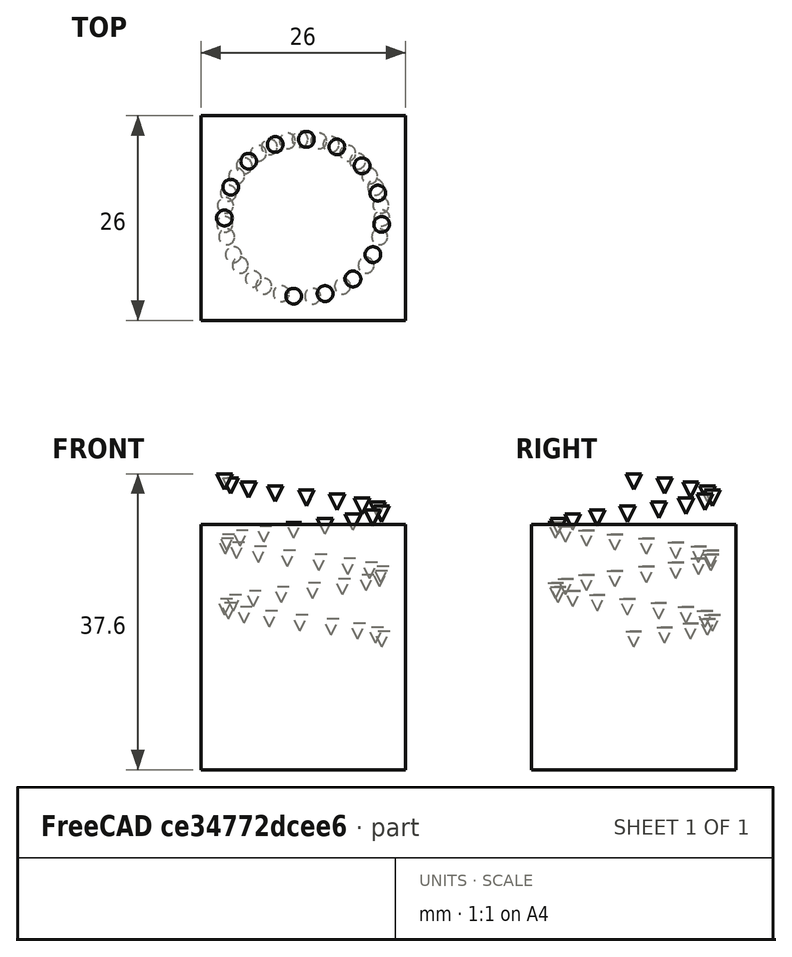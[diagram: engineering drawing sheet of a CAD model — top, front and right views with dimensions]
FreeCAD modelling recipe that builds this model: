
FCSTD DOCUMENT  (FreeCAD 1.0R39109 (Git))
Label: PathArray
License: All rights reserved
objects: App::DocumentObjectGroupPython×1251, Part::FeaturePython×2, App::Part×2, Part::Cone×1, Part::Helix×1
note: 4 computed .brp shape members not serialized (recipe doc carries the construction recipe); baked Part::Feature solids carry a one-line shape summary decoded from their .brp

FEATURE [App::DocumentObjectGroupPython] HALFPI  # scripted group (container) (typed FeaturePython)
  name = HALFPI
  value = pi/2.
FEATURE [App::DocumentObjectGroupPython] PI  # scripted group (container) (typed FeaturePython)
  name = PI
  value = 1.*pi
FEATURE [App::DocumentObjectGroupPython] TWOPI  # scripted group (container) (typed FeaturePython)
  name = TWOPI
  value = 2.*pi
FEATURE [App::DocumentObjectGroupPython] Constants  # scripted group (container) (typed FeaturePython)
  Group = -> [HALFPI,PI,TWOPI]
FEATURE [App::DocumentObjectGroupPython] Variables  # scripted group (container) (typed FeaturePython)
FEATURE [App::DocumentObjectGroupPython] Quantities  # scripted group (container) (typed FeaturePython)
FEATURE [App::DocumentObjectGroupPython] Isotopes  # scripted group (container) (typed FeaturePython)
FEATURE [App::DocumentObjectGroupPython] Elements  # scripted group (container) (typed FeaturePython)
FEATURE [App::DocumentObjectGroupPython] Matrix  # scripted group (container) (typed FeaturePython)
FEATURE [App::DocumentObjectGroupPython] Surfaces  # scripted group (container) (typed FeaturePython)
FEATURE [App::DocumentObjectGroupPython] Opticals  # scripted group (container) (typed FeaturePython)
  Group = -> [Matrix,Surfaces]
FEATURE [App::DocumentObjectGroupPython] G4Isotopes  # scripted group (container) (typed FeaturePython)
FEATURE [App::DocumentObjectGroupPython] H_element  # scripted group (container) (typed FeaturePython)
  Z = 1
  atom_value = 1.008
  formula = H
  name = H_element
FEATURE [App::DocumentObjectGroupPython] He_element  # scripted group (container) (typed FeaturePython)
  Z = 2
  atom_value = 4.0026
  formula = He
  name = He_element
FEATURE [App::DocumentObjectGroupPython] Li_element  # scripted group (container) (typed FeaturePython)
  Z = 3
  atom_value = 6.94
  formula = Li
  name = Li_element
FEATURE [App::DocumentObjectGroupPython] Be_element  # scripted group (container) (typed FeaturePython)
  Z = 4
  atom_value = 9.01218
  formula = Be
  name = Be_element
FEATURE [App::DocumentObjectGroupPython] B_element  # scripted group (container) (typed FeaturePython)
  Z = 5
  atom_value = 10.81
  formula = B
  name = B_element
FEATURE [App::DocumentObjectGroupPython] C_element  # scripted group (container) (typed FeaturePython)
  Z = 6
  atom_value = 12.011
  formula = C
  name = C_element
FEATURE [App::DocumentObjectGroupPython] N_element  # scripted group (container) (typed FeaturePython)
  Z = 7
  atom_value = 14.007
  formula = N
  name = N_element
FEATURE [App::DocumentObjectGroupPython] O_element  # scripted group (container) (typed FeaturePython)
  Z = 8
  atom_value = 15.999
  formula = O
  name = O_element
FEATURE [App::DocumentObjectGroupPython] F_element  # scripted group (container) (typed FeaturePython)
  Z = 9
  atom_value = 18.9984
  formula = F
  name = F_element
FEATURE [App::DocumentObjectGroupPython] Ne_element  # scripted group (container) (typed FeaturePython)
  Z = 10
  atom_value = 20.1797
  formula = Ne
  name = Ne_element
FEATURE [App::DocumentObjectGroupPython] Na_element  # scripted group (container) (typed FeaturePython)
  Z = 11
  atom_value = 22.9898
  formula = Na
  name = Na_element
FEATURE [App::DocumentObjectGroupPython] Mg_element  # scripted group (container) (typed FeaturePython)
  Z = 12
  atom_value = 24.305
  formula = Mg
  name = Mg_element
FEATURE [App::DocumentObjectGroupPython] Al_element  # scripted group (container) (typed FeaturePython)
  Z = 13
  atom_value = 26.9815
  formula = Al
  name = Al_element
FEATURE [App::DocumentObjectGroupPython] Si_element  # scripted group (container) (typed FeaturePython)
  Z = 14
  atom_value = 28.085
  formula = Si
  name = Si_element
FEATURE [App::DocumentObjectGroupPython] P_element  # scripted group (container) (typed FeaturePython)
  Z = 15
  atom_value = 30.9738
  formula = P
  name = P_element
FEATURE [App::DocumentObjectGroupPython] S_element  # scripted group (container) (typed FeaturePython)
  Z = 16
  atom_value = 32.06
  formula = S
  name = S_element
FEATURE [App::DocumentObjectGroupPython] Cl_element  # scripted group (container) (typed FeaturePython)
  Z = 17
  atom_value = 35.45
  formula = Cl
  name = Cl_element
FEATURE [App::DocumentObjectGroupPython] Ar_element  # scripted group (container) (typed FeaturePython)
  Z = 18
  atom_value = 39.95
  formula = Ar
  name = Ar_element
FEATURE [App::DocumentObjectGroupPython] K_element  # scripted group (container) (typed FeaturePython)
  Z = 19
  atom_value = 39.0983
  formula = K
  name = K_element
FEATURE [App::DocumentObjectGroupPython] Ca_element  # scripted group (container) (typed FeaturePython)
  Z = 20
  atom_value = 40.078
  formula = Ca
  name = Ca_element
FEATURE [App::DocumentObjectGroupPython] Sc_element  # scripted group (container) (typed FeaturePython)
  Z = 21
  atom_value = 44.9559
  formula = Sc
  name = Sc_element
FEATURE [App::DocumentObjectGroupPython] Ti_element  # scripted group (container) (typed FeaturePython)
  Z = 22
  atom_value = 47.867
  formula = Ti
  name = Ti_element
FEATURE [App::DocumentObjectGroupPython] V_element  # scripted group (container) (typed FeaturePython)
  Z = 23
  atom_value = 50.9415
  formula = V
  name = V_element
FEATURE [App::DocumentObjectGroupPython] Cr_element  # scripted group (container) (typed FeaturePython)
  Z = 24
  atom_value = 51.9961
  formula = Cr
  name = Cr_element
FEATURE [App::DocumentObjectGroupPython] Mn_element  # scripted group (container) (typed FeaturePython)
  Z = 25
  atom_value = 54.938
  formula = Mn
  name = Mn_element
FEATURE [App::DocumentObjectGroupPython] Fe_element  # scripted group (container) (typed FeaturePython)
  Z = 26
  atom_value = 55.845
  formula = Fe
  name = Fe_element
FEATURE [App::DocumentObjectGroupPython] Co_element  # scripted group (container) (typed FeaturePython)
  Z = 27
  atom_value = 58.9332
  formula = Co
  name = Co_element
FEATURE [App::DocumentObjectGroupPython] Ni_element  # scripted group (container) (typed FeaturePython)
  Z = 28
  atom_value = 58.6934
  formula = Ni
  name = Ni_element
FEATURE [App::DocumentObjectGroupPython] Cu_element  # scripted group (container) (typed FeaturePython)
  Z = 29
  atom_value = 63.546
  formula = Cu
  name = Cu_element
FEATURE [App::DocumentObjectGroupPython] Zn_element  # scripted group (container) (typed FeaturePython)
  Z = 30
  atom_value = 65.38
  formula = Zn
  name = Zn_element
FEATURE [App::DocumentObjectGroupPython] Ga_element  # scripted group (container) (typed FeaturePython)
  Z = 31
  atom_value = 69.723
  formula = Ga
  name = Ga_element
FEATURE [App::DocumentObjectGroupPython] Ge_element  # scripted group (container) (typed FeaturePython)
  Z = 32
  atom_value = 72.63
  formula = Ge
  name = Ge_element
FEATURE [App::DocumentObjectGroupPython] As_element  # scripted group (container) (typed FeaturePython)
  Z = 33
  atom_value = 74.9216
  formula = As
  name = As_element
FEATURE [App::DocumentObjectGroupPython] Se_element  # scripted group (container) (typed FeaturePython)
  Z = 34
  atom_value = 78.971
  formula = Se
  name = Se_element
FEATURE [App::DocumentObjectGroupPython] Br_element  # scripted group (container) (typed FeaturePython)
  Z = 35
  atom_value = 79.904
  formula = Br
  name = Br_element
FEATURE [App::DocumentObjectGroupPython] Kr_element  # scripted group (container) (typed FeaturePython)
  Z = 36
  atom_value = 83.798
  formula = Kr
  name = Kr_element
FEATURE [App::DocumentObjectGroupPython] Rb_element  # scripted group (container) (typed FeaturePython)
  Z = 37
  atom_value = 85.4678
  formula = Rb
  name = Rb_element
FEATURE [App::DocumentObjectGroupPython] Sr_element  # scripted group (container) (typed FeaturePython)
  Z = 38
  atom_value = 87.62
  formula = Sr
  name = Sr_element
FEATURE [App::DocumentObjectGroupPython] Y_element  # scripted group (container) (typed FeaturePython)
  Z = 39
  atom_value = 88.9058
  formula = Y
  name = Y_element
FEATURE [App::DocumentObjectGroupPython] Zr_element  # scripted group (container) (typed FeaturePython)
  Z = 40
  atom_value = 91.224
  formula = Zr
  name = Zr_element
FEATURE [App::DocumentObjectGroupPython] Nb_element  # scripted group (container) (typed FeaturePython)
  Z = 41
  atom_value = 92.9064
  formula = Nb
  name = Nb_element
FEATURE [App::DocumentObjectGroupPython] Mo_element  # scripted group (container) (typed FeaturePython)
  Z = 42
  atom_value = 95.95
  formula = Mo
  name = Mo_element
FEATURE [App::DocumentObjectGroupPython] Tc_element  # scripted group (container) (typed FeaturePython)
  Z = 43
  atom_value = 97
  formula = Tc
  name = Tc_element
FEATURE [App::DocumentObjectGroupPython] Ru_element  # scripted group (container) (typed FeaturePython)
  Z = 44
  atom_value = 101.07
  formula = Ru
  name = Ru_element
FEATURE [App::DocumentObjectGroupPython] Rh_element  # scripted group (container) (typed FeaturePython)
  Z = 45
  atom_value = 102.905
  formula = Rh
  name = Rh_element
FEATURE [App::DocumentObjectGroupPython] Pd_element  # scripted group (container) (typed FeaturePython)
  Z = 46
  atom_value = 106.42
  formula = Pd
  name = Pd_element
FEATURE [App::DocumentObjectGroupPython] Ag_element  # scripted group (container) (typed FeaturePython)
  Z = 47
  atom_value = 107.868
  formula = Ag
  name = Ag_element
FEATURE [App::DocumentObjectGroupPython] Cd_element  # scripted group (container) (typed FeaturePython)
  Z = 48
  atom_value = 112.414
  formula = Cd
  name = Cd_element
FEATURE [App::DocumentObjectGroupPython] In_element  # scripted group (container) (typed FeaturePython)
  Z = 49
  atom_value = 114.818
  formula = In
  name = In_element
FEATURE [App::DocumentObjectGroupPython] Sn_element  # scripted group (container) (typed FeaturePython)
  Z = 50
  atom_value = 118.71
  formula = Sn
  name = Sn_element
FEATURE [App::DocumentObjectGroupPython] Sb_element  # scripted group (container) (typed FeaturePython)
  Z = 51
  atom_value = 121.76
  formula = Sb
  name = Sb_element
FEATURE [App::DocumentObjectGroupPython] Te_element  # scripted group (container) (typed FeaturePython)
  Z = 52
  atom_value = 127.6
  formula = Te
  name = Te_element
FEATURE [App::DocumentObjectGroupPython] I_element  # scripted group (container) (typed FeaturePython)
  Z = 53
  atom_value = 126.904
  formula = I
  name = I_element
FEATURE [App::DocumentObjectGroupPython] Xe_element  # scripted group (container) (typed FeaturePython)
  Z = 54
  atom_value = 131.293
  formula = Xe
  name = Xe_element
FEATURE [App::DocumentObjectGroupPython] Cs_element  # scripted group (container) (typed FeaturePython)
  Z = 55
  atom_value = 132.905
  formula = Cs
  name = Cs_element
FEATURE [App::DocumentObjectGroupPython] Ba_element  # scripted group (container) (typed FeaturePython)
  Z = 56
  atom_value = 137.327
  formula = Ba
  name = Ba_element
FEATURE [App::DocumentObjectGroupPython] La_element  # scripted group (container) (typed FeaturePython)
  Z = 57
  atom_value = 138.905
  formula = La
  name = La_element
FEATURE [App::DocumentObjectGroupPython] Ce_element  # scripted group (container) (typed FeaturePython)
  Z = 58
  atom_value = 140.116
  formula = Ce
  name = Ce_element
FEATURE [App::DocumentObjectGroupPython] Pr_element  # scripted group (container) (typed FeaturePython)
  Z = 59
  atom_value = 140.908
  formula = Pr
  name = Pr_element
FEATURE [App::DocumentObjectGroupPython] Nd_element  # scripted group (container) (typed FeaturePython)
  Z = 60
  atom_value = 144.242
  formula = Nd
  name = Nd_element
FEATURE [App::DocumentObjectGroupPython] Pm_element  # scripted group (container) (typed FeaturePython)
  Z = 61
  atom_value = 145
  formula = Pm
  name = Pm_element
FEATURE [App::DocumentObjectGroupPython] Sm_element  # scripted group (container) (typed FeaturePython)
  Z = 62
  atom_value = 150.36
  formula = Sm
  name = Sm_element
FEATURE [App::DocumentObjectGroupPython] Eu_element  # scripted group (container) (typed FeaturePython)
  Z = 63
  atom_value = 151.964
  formula = Eu
  name = Eu_element
FEATURE [App::DocumentObjectGroupPython] Gd_element  # scripted group (container) (typed FeaturePython)
  Z = 64
  atom_value = 157.25
  formula = Gd
  name = Gd_element
FEATURE [App::DocumentObjectGroupPython] Tb_element  # scripted group (container) (typed FeaturePython)
  Z = 65
  atom_value = 158.925
  formula = Tb
  name = Tb_element
FEATURE [App::DocumentObjectGroupPython] Dy_element  # scripted group (container) (typed FeaturePython)
  Z = 66
  atom_value = 162.5
  formula = Dy
  name = Dy_element
FEATURE [App::DocumentObjectGroupPython] Ho_element  # scripted group (container) (typed FeaturePython)
  Z = 67
  atom_value = 164.93
  formula = Ho
  name = Ho_element
FEATURE [App::DocumentObjectGroupPython] Er_element  # scripted group (container) (typed FeaturePython)
  Z = 68
  atom_value = 167.259
  formula = Er
  name = Er_element
FEATURE [App::DocumentObjectGroupPython] Tm_element  # scripted group (container) (typed FeaturePython)
  Z = 69
  atom_value = 168.934
  formula = Tm
  name = Tm_element
FEATURE [App::DocumentObjectGroupPython] Yb_element  # scripted group (container) (typed FeaturePython)
  Z = 70
  atom_value = 173.045
  formula = Yb
  name = Yb_element
FEATURE [App::DocumentObjectGroupPython] Lu_element  # scripted group (container) (typed FeaturePython)
  Z = 71
  atom_value = 174.967
  formula = Lu
  name = Lu_element
FEATURE [App::DocumentObjectGroupPython] Hf_element  # scripted group (container) (typed FeaturePython)
  Z = 72
  atom_value = 178.49
  formula = Hf
  name = Hf_element
FEATURE [App::DocumentObjectGroupPython] Ta_element  # scripted group (container) (typed FeaturePython)
  Z = 73
  atom_value = 180.948
  formula = Ta
  name = Ta_element
FEATURE [App::DocumentObjectGroupPython] W_element  # scripted group (container) (typed FeaturePython)
  Z = 74
  atom_value = 183.84
  formula = W
  name = W_element
FEATURE [App::DocumentObjectGroupPython] Re_element  # scripted group (container) (typed FeaturePython)
  Z = 75
  atom_value = 186.207
  formula = Re
  name = Re_element
FEATURE [App::DocumentObjectGroupPython] Os_element  # scripted group (container) (typed FeaturePython)
  Z = 76
  atom_value = 190.23
  formula = Os
  name = Os_element
FEATURE [App::DocumentObjectGroupPython] Ir_element  # scripted group (container) (typed FeaturePython)
  Z = 77
  atom_value = 192.217
  formula = Ir
  name = Ir_element
FEATURE [App::DocumentObjectGroupPython] Pt_element  # scripted group (container) (typed FeaturePython)
  Z = 78
  atom_value = 195.084
  formula = Pt
  name = Pt_element
FEATURE [App::DocumentObjectGroupPython] Au_element  # scripted group (container) (typed FeaturePython)
  Z = 79
  atom_value = 196.967
  formula = Au
  name = Au_element
FEATURE [App::DocumentObjectGroupPython] Hg_element  # scripted group (container) (typed FeaturePython)
  Z = 80
  atom_value = 200.592
  formula = Hg
  name = Hg_element
FEATURE [App::DocumentObjectGroupPython] Tl_element  # scripted group (container) (typed FeaturePython)
  Z = 81
  atom_value = 204.38
  formula = Tl
  name = Tl_element
FEATURE [App::DocumentObjectGroupPython] Pb_element  # scripted group (container) (typed FeaturePython)
  Z = 82
  atom_value = 207.2
  formula = Pb
  name = Pb_element
FEATURE [App::DocumentObjectGroupPython] Bi_element  # scripted group (container) (typed FeaturePython)
  Z = 83
  atom_value = 208.98
  formula = Bi
  name = Bi_element
FEATURE [App::DocumentObjectGroupPython] Po_element  # scripted group (container) (typed FeaturePython)
  Z = 84
  atom_value = 209
  formula = Po
  name = Po_element
FEATURE [App::DocumentObjectGroupPython] At_element  # scripted group (container) (typed FeaturePython)
  Z = 85
  atom_value = 210
  formula = At
  name = At_element
FEATURE [App::DocumentObjectGroupPython] Rn_element  # scripted group (container) (typed FeaturePython)
  Z = 86
  atom_value = 222
  formula = Rn
  name = Rn_element
FEATURE [App::DocumentObjectGroupPython] Fr_element  # scripted group (container) (typed FeaturePython)
  Z = 87
  atom_value = 223
  formula = Fr
  name = Fr_element
FEATURE [App::DocumentObjectGroupPython] Ra_element  # scripted group (container) (typed FeaturePython)
  Z = 88
  atom_value = 226
  formula = Ra
  name = Ra_element
FEATURE [App::DocumentObjectGroupPython] Ac_element  # scripted group (container) (typed FeaturePython)
  Z = 89
  atom_value = 227
  formula = Ac
  name = Ac_element
FEATURE [App::DocumentObjectGroupPython] Th_element  # scripted group (container) (typed FeaturePython)
  Z = 90
  atom_value = 232.038
  formula = Th
  name = Th_element
FEATURE [App::DocumentObjectGroupPython] Pa_element  # scripted group (container) (typed FeaturePython)
  Z = 91
  atom_value = 231.036
  formula = Pa
  name = Pa_element
FEATURE [App::DocumentObjectGroupPython] U_element  # scripted group (container) (typed FeaturePython)
  Z = 92
  atom_value = 238.029
  formula = U
  name = U_element
FEATURE [App::DocumentObjectGroupPython] Np_element  # scripted group (container) (typed FeaturePython)
  Z = 93
  atom_value = 237
  formula = Np
  name = Np_element
FEATURE [App::DocumentObjectGroupPython] Pu_element  # scripted group (container) (typed FeaturePython)
  Z = 94
  atom_value = 244
  formula = Pu
  name = Pu_element
FEATURE [App::DocumentObjectGroupPython] Am_element  # scripted group (container) (typed FeaturePython)
  Z = 95
  atom_value = 243
  formula = Am
  name = Am_element
FEATURE [App::DocumentObjectGroupPython] Cm_element  # scripted group (container) (typed FeaturePython)
  Z = 96
  atom_value = 247
  formula = Cm
  name = Cm_element
FEATURE [App::DocumentObjectGroupPython] Bk_element  # scripted group (container) (typed FeaturePython)
  Z = 97
  atom_value = 247
  formula = Bk
  name = Bk_element
FEATURE [App::DocumentObjectGroupPython] Cf_element  # scripted group (container) (typed FeaturePython)
  Z = 98
  atom_value = 251
  formula = Cf
  name = Cf_element
FEATURE [App::DocumentObjectGroupPython] G4Elements  # scripted group (container) (typed FeaturePython)
  Group = -> [H_element,He_element,Li_element,Be_element,B_element,C_element,N_element,O_element,F_element,Ne_element,Na_element,Mg_element,Al_element,Si_element,P_element,S_element,Cl_element,Ar_element,K_element,Ca_element,Sc_element,Ti_element,V_element,Cr_element,Mn_element,Fe_element,Co_element,Ni_element,Cu_element,Zn_element,Ga_element,Ge_element,As_element,Se_element,Br_element,Kr_element,Rb_element,+61 more]
FEATURE [App::DocumentObjectGroupPython] H_element001  label="H_element : 0.101"  # scripted group (container) (typed FeaturePython)
  n = 0.101327
FEATURE [App::DocumentObjectGroupPython] C_element001  label="C_element : 0.775"  # scripted group (container) (typed FeaturePython)
  n = 0.7755
FEATURE [App::DocumentObjectGroupPython] N_element001  label="N_element : 0.035"  # scripted group (container) (typed FeaturePython)
  n = 0.035057
FEATURE [App::DocumentObjectGroupPython] O_element001  label="O_element : 0.052"  # scripted group (container) (typed FeaturePython)
  n = 0.0523159
FEATURE [App::DocumentObjectGroupPython] F_element001  label="F_element : 0.017"  # scripted group (container) (typed FeaturePython)
  n = 0.017422
FEATURE [App::DocumentObjectGroupPython] Ca_element001  label="Ca_element : 0.018"  # scripted group (container) (typed FeaturePython)
  n = 0.018378
FEATURE [App::DocumentObjectGroupPython] G4_A_150_TISSUE  label="G4_A-150_TISSUE"  # scripted group (container) (typed FeaturePython)
  Dunit = g/cm3
  Dvalue = 1.127
  Group = -> [H_element001,C_element001,N_element001,O_element001,F_element001,Ca_element001]
  conduct = 2
  density = 1
  expand = 3
  formula = G4_A-150_TISSUE
  name = G4_A-150_TISSUE
  specific = 4
FEATURE [App::DocumentObjectGroupPython] C_element002  label="C_element : 3"  # scripted group (container) (typed FeaturePython)
  n = 3
  ref = C_element
FEATURE [App::DocumentObjectGroupPython] H_element002  label="H_element : 6"  # scripted group (container) (typed FeaturePython)
  n = 6
  ref = H_element
FEATURE [App::DocumentObjectGroupPython] O_element002  label="O_element : 1"  # scripted group (container) (typed FeaturePython)
  n = 1
  ref = O_element
FEATURE [App::DocumentObjectGroupPython] G4_ACETONE  # scripted group (container) (typed FeaturePython)
  Dunit = g/cm3
  Dvalue = 0.7899
  Group = -> [C_element002,H_element002,O_element002]
  conduct = 2
  density = 1
  expand = 3
  formula = G4_ACETONE
  name = G4_ACETONE
  specific = 4
FEATURE [App::DocumentObjectGroupPython] C_element003  label="C_element : 2"  # scripted group (container) (typed FeaturePython)
  n = 2
  ref = C_element
FEATURE [App::DocumentObjectGroupPython] H_element003  label="H_element : 2"  # scripted group (container) (typed FeaturePython)
  n = 2
  ref = H_element
FEATURE [App::DocumentObjectGroupPython] G4_ACETYLENE  # scripted group (container) (typed FeaturePython)
  Dunit = g/cm3
  Dvalue = 0.0010967
  Group = -> [C_element003,H_element003]
  conduct = 2
  density = 1
  expand = 3
  formula = G4_ACETYLENE
  name = G4_ACETYLENE
  specific = 4
FEATURE [App::DocumentObjectGroupPython] C_element004  label="C_element : 5"  # scripted group (container) (typed FeaturePython)
  n = 5
  ref = C_element
FEATURE [App::DocumentObjectGroupPython] H_element004  label="H_element : 5"  # scripted group (container) (typed FeaturePython)
  n = 5
  ref = H_element
FEATURE [App::DocumentObjectGroupPython] N_element002  label="N_element : 5"  # scripted group (container) (typed FeaturePython)
  n = 5
  ref = N_element
FEATURE [App::DocumentObjectGroupPython] G4_ADENINE  # scripted group (container) (typed FeaturePython)
  Dunit = g/cm3
  Dvalue = 1.6
  Group = -> [C_element004,H_element004,N_element002]
  conduct = 2
  density = 1
  expand = 3
  formula = G4_ADENINE
  name = G4_ADENINE
  specific = 4
FEATURE [App::DocumentObjectGroupPython] H_element005  label="H_element : 0.114"  # scripted group (container) (typed FeaturePython)
  n = 0.114
FEATURE [App::DocumentObjectGroupPython] C_element005  label="C_element : 0.598"  # scripted group (container) (typed FeaturePython)
  n = 0.598
FEATURE [App::DocumentObjectGroupPython] N_element003  label="N_element : 0.007"  # scripted group (container) (typed FeaturePython)
  n = 0.007
FEATURE [App::DocumentObjectGroupPython] O_element003  label="O_element : 0.278"  # scripted group (container) (typed FeaturePython)
  n = 0.278
FEATURE [App::DocumentObjectGroupPython] Na_element001  label="Na_element : 0.001"  # scripted group (container) (typed FeaturePython)
  n = 0.001
FEATURE [App::DocumentObjectGroupPython] S_element001  label="S_element : 0.001"  # scripted group (container) (typed FeaturePython)
  n = 0.001
FEATURE [App::DocumentObjectGroupPython] Cl_element001  label="Cl_element : 0.001"  # scripted group (container) (typed FeaturePython)
  n = 0.001
FEATURE [App::DocumentObjectGroupPython] G4_ADIPOSE_TISSUE_ICRP  # scripted group (container) (typed FeaturePython)
  Dunit = g/cm3
  Dvalue = 0.95
  Group = -> [H_element005,C_element005,N_element003,O_element003,Na_element001,S_element001,Cl_element001]
  conduct = 2
  density = 1
  expand = 3
  formula = G4_ADIPOSE_TISSUE_ICRP
  name = G4_ADIPOSE_TISSUE_ICRP
  specific = 4
FEATURE [App::DocumentObjectGroupPython] C_element006  label="C_element : 0.000"  # scripted group (container) (typed FeaturePython)
  n = 0.000124
FEATURE [App::DocumentObjectGroupPython] N_element004  label="N_element : 0.755"  # scripted group (container) (typed FeaturePython)
  n = 0.755268
FEATURE [App::DocumentObjectGroupPython] O_element004  label="O_element : 0.232"  # scripted group (container) (typed FeaturePython)
  n = 0.231781
FEATURE [App::DocumentObjectGroupPython] Ar_element001  label="Ar_element : 0.013"  # scripted group (container) (typed FeaturePython)
  n = 0.012827
FEATURE [App::DocumentObjectGroupPython] G4_AIR  # scripted group (container) (typed FeaturePython)
  Dunit = g/cm3
  Dvalue = 0.00120479
  Group = -> [C_element006,N_element004,O_element004,Ar_element001]
  conduct = 2
  density = 1
  expand = 3
  formula = G4_AIR
  name = G4_AIR
  specific = 4
FEATURE [App::DocumentObjectGroupPython] C_element007  label="C_element : 006"  # scripted group (container) (typed FeaturePython)
  n = 3
  ref = C_element
FEATURE [App::DocumentObjectGroupPython] H_element006  label="H_element : 7"  # scripted group (container) (typed FeaturePython)
  n = 7
  ref = H_element
FEATURE [App::DocumentObjectGroupPython] N_element005  label="N_element : 1"  # scripted group (container) (typed FeaturePython)
  n = 1
  ref = N_element
FEATURE [App::DocumentObjectGroupPython] O_element005  label="O_element : 2"  # scripted group (container) (typed FeaturePython)
  n = 2
  ref = O_element
FEATURE [App::DocumentObjectGroupPython] G4_ALANINE  # scripted group (container) (typed FeaturePython)
  Dunit = g/cm3
  Dvalue = 1.42
  Group = -> [C_element007,H_element006,N_element005,O_element005]
  conduct = 2
  density = 1
  expand = 3
  formula = G4_ALANINE
  name = G4_ALANINE
  specific = 4
FEATURE [App::DocumentObjectGroupPython] Al_element001  label="Al_element : 2"  # scripted group (container) (typed FeaturePython)
  n = 2
  ref = Al_element
FEATURE [App::DocumentObjectGroupPython] O_element006  label="O_element : 3"  # scripted group (container) (typed FeaturePython)
  n = 3
  ref = O_element
FEATURE [App::DocumentObjectGroupPython] G4_ALUMINUM_OXIDE  # scripted group (container) (typed FeaturePython)
  Dunit = g/cm3
  Dvalue = 3.97
  Group = -> [Al_element001,O_element006]
  conduct = 2
  density = 1
  expand = 3
  formula = G4_ALUMINUM_OXIDE
  name = G4_ALUMINUM_OXIDE
  specific = 4
FEATURE [App::DocumentObjectGroupPython] H_element007  label="H_element : 0.106"  # scripted group (container) (typed FeaturePython)
  n = 0.10593
FEATURE [App::DocumentObjectGroupPython] C_element008  label="C_element : 0.789"  # scripted group (container) (typed FeaturePython)
  n = 0.788974
FEATURE [App::DocumentObjectGroupPython] O_element007  label="O_element : 0.105"  # scripted group (container) (typed FeaturePython)
  n = 0.105096
FEATURE [App::DocumentObjectGroupPython] G4_AMBER  # scripted group (container) (typed FeaturePython)
  Dunit = g/cm3
  Dvalue = 1.1
  Group = -> [H_element007,C_element008,O_element007]
  conduct = 2
  density = 1
  expand = 3
  formula = G4_AMBER
  name = G4_AMBER
  specific = 4
FEATURE [App::DocumentObjectGroupPython] N_element006  label="N_element : 006"  # scripted group (container) (typed FeaturePython)
  n = 1
  ref = N_element
FEATURE [App::DocumentObjectGroupPython] H_element008  label="H_element : 3"  # scripted group (container) (typed FeaturePython)
  n = 3
  ref = H_element
FEATURE [App::DocumentObjectGroupPython] G4_AMMONIA  # scripted group (container) (typed FeaturePython)
  Dunit = g/cm3
  Dvalue = 0.000826019
  Group = -> [N_element006,H_element008]
  conduct = 2
  density = 1
  expand = 3
  formula = G4_AMMONIA
  name = G4_AMMONIA
  specific = 4
FEATURE [App::DocumentObjectGroupPython] C_element009  label="C_element : 6"  # scripted group (container) (typed FeaturePython)
  n = 6
  ref = C_element
FEATURE [App::DocumentObjectGroupPython] H_element009  label="H_element : 008"  # scripted group (container) (typed FeaturePython)
  n = 7
  ref = H_element
FEATURE [App::DocumentObjectGroupPython] N_element007  label="N_element : 007"  # scripted group (container) (typed FeaturePython)
  n = 1
  ref = N_element
FEATURE [App::DocumentObjectGroupPython] G4_ANILINE  # scripted group (container) (typed FeaturePython)
  Dunit = g/cm3
  Dvalue = 1.0235
  Group = -> [C_element009,H_element009,N_element007]
  conduct = 2
  density = 1
  expand = 3
  formula = G4_ANILINE
  name = G4_ANILINE
  specific = 4
FEATURE [App::DocumentObjectGroupPython] C_element010  label="C_element : 14"  # scripted group (container) (typed FeaturePython)
  n = 14
  ref = C_element
FEATURE [App::DocumentObjectGroupPython] H_element010  label="H_element : 10"  # scripted group (container) (typed FeaturePython)
  n = 10
  ref = H_element
FEATURE [App::DocumentObjectGroupPython] G4_ANTHRACENE  # scripted group (container) (typed FeaturePython)
  Dunit = g/cm3
  Dvalue = 1.283
  Group = -> [C_element010,H_element010]
  conduct = 2
  density = 1
  expand = 3
  formula = G4_ANTHRACENE
  name = G4_ANTHRACENE
  specific = 4
FEATURE [App::DocumentObjectGroupPython] H_element011  label="H_element : 0.065"  # scripted group (container) (typed FeaturePython)
  n = 0.0654709
FEATURE [App::DocumentObjectGroupPython] C_element011  label="C_element : 0.537"  # scripted group (container) (typed FeaturePython)
  n = 0.536944
FEATURE [App::DocumentObjectGroupPython] N_element008  label="N_element : 0.021"  # scripted group (container) (typed FeaturePython)
  n = 0.0215
FEATURE [App::DocumentObjectGroupPython] O_element008  label="O_element : 0.032"  # scripted group (container) (typed FeaturePython)
  n = 0.032085
FEATURE [App::DocumentObjectGroupPython] F_element002  label="F_element : 0.167"  # scripted group (container) (typed FeaturePython)
  n = 0.167411
FEATURE [App::DocumentObjectGroupPython] Ca_element002  label="Ca_element : 0.177"  # scripted group (container) (typed FeaturePython)
  n = 0.176589
FEATURE [App::DocumentObjectGroupPython] G4_B_100_BONE  label="G4_B-100_BONE"  # scripted group (container) (typed FeaturePython)
  Dunit = g/cm3
  Dvalue = 1.45
  Group = -> [H_element011,C_element011,N_element008,O_element008,F_element002,Ca_element002]
  conduct = 2
  density = 1
  expand = 3
  formula = G4_B-100_BONE
  name = G4_B-100_BONE
  specific = 4
FEATURE [App::DocumentObjectGroupPython] H_element012  label="H_element : 0.057"  # scripted group (container) (typed FeaturePython)
  n = 0.057441
FEATURE [App::DocumentObjectGroupPython] C_element012  label="C_element : 0.790"  # scripted group (container) (typed FeaturePython)
  n = 0.774591
FEATURE [App::DocumentObjectGroupPython] O_element009  label="O_element : 0.168"  # scripted group (container) (typed FeaturePython)
  n = 0.167968
FEATURE [App::DocumentObjectGroupPython] G4_BAKELITE  # scripted group (container) (typed FeaturePython)
  Dunit = g/cm3
  Dvalue = 1.25
  Group = -> [H_element012,C_element012,O_element009]
  conduct = 2
  density = 1
  expand = 3
  formula = G4_BAKELITE
  name = G4_BAKELITE
  specific = 4
FEATURE [App::DocumentObjectGroupPython] Ba_element001  label="Ba_element : 1"  # scripted group (container) (typed FeaturePython)
  n = 1
  ref = Ba_element
FEATURE [App::DocumentObjectGroupPython] F_element003  label="F_element : 2"  # scripted group (container) (typed FeaturePython)
  n = 2
  ref = F_element
FEATURE [App::DocumentObjectGroupPython] G4_BARIUM_FLUORIDE  # scripted group (container) (typed FeaturePython)
  Dunit = g/cm3
  Dvalue = 4.89
  Group = -> [Ba_element001,F_element003]
  conduct = 2
  density = 1
  expand = 3
  formula = G4_BARIUM_FLUORIDE
  name = G4_BARIUM_FLUORIDE
  specific = 4
FEATURE [App::DocumentObjectGroupPython] Ba_element002  label="Ba_element : 002"  # scripted group (container) (typed FeaturePython)
  n = 1
  ref = Ba_element
FEATURE [App::DocumentObjectGroupPython] S_element002  label="S_element : 1"  # scripted group (container) (typed FeaturePython)
  n = 1
  ref = S_element
FEATURE [App::DocumentObjectGroupPython] O_element010  label="O_element : 4"  # scripted group (container) (typed FeaturePython)
  n = 4
  ref = O_element
FEATURE [App::DocumentObjectGroupPython] G4_BARIUM_SULFATE  # scripted group (container) (typed FeaturePython)
  Dunit = g/cm3
  Dvalue = 4.5
  Group = -> [Ba_element002,S_element002,O_element010]
  conduct = 2
  density = 1
  expand = 3
  formula = G4_BARIUM_SULFATE
  name = G4_BARIUM_SULFATE
  specific = 4
FEATURE [App::DocumentObjectGroupPython] C_element013  label="C_element : 007"  # scripted group (container) (typed FeaturePython)
  n = 6
  ref = C_element
FEATURE [App::DocumentObjectGroupPython] H_element013  label="H_element : 009"  # scripted group (container) (typed FeaturePython)
  n = 6
  ref = H_element
FEATURE [App::DocumentObjectGroupPython] G4_BENZENE  # scripted group (container) (typed FeaturePython)
  Dunit = g/cm3
  Dvalue = 0.87865
  Group = -> [C_element013,H_element013]
  conduct = 2
  density = 1
  expand = 3
  formula = G4_BENZENE
  name = G4_BENZENE
  specific = 4
FEATURE [App::DocumentObjectGroupPython] Be_element001  label="Be_element : 1"  # scripted group (container) (typed FeaturePython)
  n = 1
  ref = Be_element
FEATURE [App::DocumentObjectGroupPython] O_element011  label="O_element : 005"  # scripted group (container) (typed FeaturePython)
  n = 1
  ref = O_element
FEATURE [App::DocumentObjectGroupPython] G4_BERYLLIUM_OXIDE  # scripted group (container) (typed FeaturePython)
  Dunit = g/cm3
  Dvalue = 3.01
  Group = -> [Be_element001,O_element011]
  conduct = 2
  density = 1
  expand = 3
  formula = G4_BERYLLIUM_OXIDE
  name = G4_BERYLLIUM_OXIDE
  specific = 4
FEATURE [App::DocumentObjectGroupPython] Bi_element001  label="Bi_element : 4"  # scripted group (container) (typed FeaturePython)
  n = 4
  ref = Bi_element
FEATURE [App::DocumentObjectGroupPython] Ge_element001  label="Ge_element : 3"  # scripted group (container) (typed FeaturePython)
  n = 3
  ref = Ge_element
FEATURE [App::DocumentObjectGroupPython] O_element012  label="O_element : 12"  # scripted group (container) (typed FeaturePython)
  n = 12
  ref = O_element
FEATURE [App::DocumentObjectGroupPython] G4_BGO  # scripted group (container) (typed FeaturePython)
  Dunit = g/cm3
  Dvalue = 7.13
  Group = -> [Bi_element001,Ge_element001,O_element012]
  conduct = 2
  density = 1
  expand = 3
  formula = G4_BGO
  name = G4_BGO
  specific = 4
FEATURE [App::DocumentObjectGroupPython] H_element014  label="H_element : 0.102"  # scripted group (container) (typed FeaturePython)
  n = 0.102
FEATURE [App::DocumentObjectGroupPython] C_element014  label="C_element : 0.110"  # scripted group (container) (typed FeaturePython)
  n = 0.11
FEATURE [App::DocumentObjectGroupPython] N_element009  label="N_element : 0.033"  # scripted group (container) (typed FeaturePython)
  n = 0.033
FEATURE [App::DocumentObjectGroupPython] O_element013  label="O_element : 0.745"  # scripted group (container) (typed FeaturePython)
  n = 0.745
FEATURE [App::DocumentObjectGroupPython] Na_element002  label="Na_element : 0.002"  # scripted group (container) (typed FeaturePython)
  n = 0.001
FEATURE [App::DocumentObjectGroupPython] P_element001  label="P_element : 0.001"  # scripted group (container) (typed FeaturePython)
  n = 0.001
FEATURE [App::DocumentObjectGroupPython] S_element003  label="S_element : 0.002"  # scripted group (container) (typed FeaturePython)
  n = 0.002
FEATURE [App::DocumentObjectGroupPython] Cl_element002  label="Cl_element : 0.003"  # scripted group (container) (typed FeaturePython)
  n = 0.003
FEATURE [App::DocumentObjectGroupPython] K_element001  label="K_element : 0.002"  # scripted group (container) (typed FeaturePython)
  n = 0.002
FEATURE [App::DocumentObjectGroupPython] Fe_element001  label="Fe_element : 0.001"  # scripted group (container) (typed FeaturePython)
  n = 0.001
FEATURE [App::DocumentObjectGroupPython] G4_BLOOD_ICRP  # scripted group (container) (typed FeaturePython)
  Dunit = g/cm3
  Dvalue = 1.06
  Group = -> [H_element014,C_element014,N_element009,O_element013,Na_element002,P_element001,S_element003,Cl_element002,K_element001,Fe_element001]
  conduct = 2
  density = 1
  expand = 3
  formula = G4_BLOOD_ICRP
  name = G4_BLOOD_ICRP
  specific = 4
FEATURE [App::DocumentObjectGroupPython] H_element015  label="H_element : 0.064"  # scripted group (container) (typed FeaturePython)
  n = 0.064
FEATURE [App::DocumentObjectGroupPython] C_element015  label="C_element : 0.278"  # scripted group (container) (typed FeaturePython)
  n = 0.278
FEATURE [App::DocumentObjectGroupPython] N_element010  label="N_element : 0.027"  # scripted group (container) (typed FeaturePython)
  n = 0.027
FEATURE [App::DocumentObjectGroupPython] O_element014  label="O_element : 0.410"  # scripted group (container) (typed FeaturePython)
  n = 0.41
FEATURE [App::DocumentObjectGroupPython] Mg_element001  label="Mg_element : 0.002"  # scripted group (container) (typed FeaturePython)
  n = 0.002
FEATURE [App::DocumentObjectGroupPython] P_element002  label="P_element : 0.070"  # scripted group (container) (typed FeaturePython)
  n = 0.07
FEATURE [App::DocumentObjectGroupPython] S_element004  label="S_element : 0.003"  # scripted group (container) (typed FeaturePython)
  n = 0.002
FEATURE [App::DocumentObjectGroupPython] Ca_element003  label="Ca_element : 0.147"  # scripted group (container) (typed FeaturePython)
  n = 0.147
FEATURE [App::DocumentObjectGroupPython] G4_BONE_COMPACT_ICRU  # scripted group (container) (typed FeaturePython)
  Dunit = g/cm3
  Dvalue = 1.85
  Group = -> [H_element015,C_element015,N_element010,O_element014,Mg_element001,P_element002,S_element004,Ca_element003]
  conduct = 2
  density = 1
  expand = 3
  formula = G4_BONE_COMPACT_ICRU
  name = G4_BONE_COMPACT_ICRU
  specific = 4
FEATURE [App::DocumentObjectGroupPython] H_element016  label="H_element : 0.034"  # scripted group (container) (typed FeaturePython)
  n = 0.034
FEATURE [App::DocumentObjectGroupPython] C_element016  label="C_element : 0.155"  # scripted group (container) (typed FeaturePython)
  n = 0.155
FEATURE [App::DocumentObjectGroupPython] N_element011  label="N_element : 0.042"  # scripted group (container) (typed FeaturePython)
  n = 0.042
FEATURE [App::DocumentObjectGroupPython] O_element015  label="O_element : 0.435"  # scripted group (container) (typed FeaturePython)
  n = 0.435
FEATURE [App::DocumentObjectGroupPython] Na_element003  label="Na_element : 0.003"  # scripted group (container) (typed FeaturePython)
  n = 0.001
FEATURE [App::DocumentObjectGroupPython] Mg_element002  label="Mg_element : 0.003"  # scripted group (container) (typed FeaturePython)
  n = 0.002
FEATURE [App::DocumentObjectGroupPython] P_element003  label="P_element : 0.103"  # scripted group (container) (typed FeaturePython)
  n = 0.103
FEATURE [App::DocumentObjectGroupPython] S_element005  label="S_element : 0.004"  # scripted group (container) (typed FeaturePython)
  n = 0.003
FEATURE [App::DocumentObjectGroupPython] Ca_element004  label="Ca_element : 0.225"  # scripted group (container) (typed FeaturePython)
  n = 0.225
FEATURE [App::DocumentObjectGroupPython] G4_BONE_CORTICAL_ICRP  # scripted group (container) (typed FeaturePython)
  Dunit = g/cm3
  Dvalue = 1.92
  Group = -> [H_element016,C_element016,N_element011,O_element015,Na_element003,Mg_element002,P_element003,S_element005,Ca_element004]
  conduct = 2
  density = 1
  expand = 3
  formula = G4_BONE_CORTICAL_ICRP
  name = G4_BONE_CORTICAL_ICRP
  specific = 4
FEATURE [App::DocumentObjectGroupPython] B_element001  label="B_element : 4"  # scripted group (container) (typed FeaturePython)
  n = 4
  ref = B_element
FEATURE [App::DocumentObjectGroupPython] C_element017  label="C_element : 1"  # scripted group (container) (typed FeaturePython)
  n = 1
  ref = C_element
FEATURE [App::DocumentObjectGroupPython] G4_BORON_CARBIDE  # scripted group (container) (typed FeaturePython)
  Dunit = g/cm3
  Dvalue = 2.52
  Group = -> [B_element001,C_element017]
  conduct = 2
  density = 1
  expand = 3
  formula = G4_BORON_CARBIDE
  name = G4_BORON_CARBIDE
  specific = 4
FEATURE [App::DocumentObjectGroupPython] B_element002  label="B_element : 2"  # scripted group (container) (typed FeaturePython)
  n = 2
  ref = B_element
FEATURE [App::DocumentObjectGroupPython] O_element016  label="O_element : 006"  # scripted group (container) (typed FeaturePython)
  n = 3
  ref = O_element
FEATURE [App::DocumentObjectGroupPython] G4_BORON_OXIDE  # scripted group (container) (typed FeaturePython)
  Dunit = g/cm3
  Dvalue = 1.812
  Group = -> [B_element002,O_element016]
  conduct = 2
  density = 1
  expand = 3
  formula = G4_BORON_OXIDE
  name = G4_BORON_OXIDE
  specific = 4
FEATURE [App::DocumentObjectGroupPython] H_element017  label="H_element : 0.107"  # scripted group (container) (typed FeaturePython)
  n = 0.107
FEATURE [App::DocumentObjectGroupPython] C_element018  label="C_element : 0.145"  # scripted group (container) (typed FeaturePython)
  n = 0.145
FEATURE [App::DocumentObjectGroupPython] N_element012  label="N_element : 0.022"  # scripted group (container) (typed FeaturePython)
  n = 0.022
FEATURE [App::DocumentObjectGroupPython] O_element017  label="O_element : 0.712"  # scripted group (container) (typed FeaturePython)
  n = 0.712
FEATURE [App::DocumentObjectGroupPython] Na_element004  label="Na_element : 0.004"  # scripted group (container) (typed FeaturePython)
  n = 0.002
FEATURE [App::DocumentObjectGroupPython] P_element004  label="P_element : 0.004"  # scripted group (container) (typed FeaturePython)
  n = 0.004
FEATURE [App::DocumentObjectGroupPython] S_element006  label="S_element : 0.005"  # scripted group (container) (typed FeaturePython)
  n = 0.002
FEATURE [App::DocumentObjectGroupPython] Cl_element003  label="Cl_element : 0.004"  # scripted group (container) (typed FeaturePython)
  n = 0.003
FEATURE [App::DocumentObjectGroupPython] K_element002  label="K_element : 0.003"  # scripted group (container) (typed FeaturePython)
  n = 0.003
FEATURE [App::DocumentObjectGroupPython] G4_BRAIN_ICRP  # scripted group (container) (typed FeaturePython)
  Dunit = g/cm3
  Dvalue = 1.04
  Group = -> [H_element017,C_element018,N_element012,O_element017,Na_element004,P_element004,S_element006,Cl_element003,K_element002]
  conduct = 2
  density = 1
  expand = 3
  formula = G4_BRAIN_ICRP
  name = G4_BRAIN_ICRP
  specific = 4
FEATURE [App::DocumentObjectGroupPython] C_element019  label="C_element : 4"  # scripted group (container) (typed FeaturePython)
  n = 4
  ref = C_element
FEATURE [App::DocumentObjectGroupPython] H_element018  label="H_element : 010"  # scripted group (container) (typed FeaturePython)
  n = 10
  ref = H_element
FEATURE [App::DocumentObjectGroupPython] G4_BUTANE  # scripted group (container) (typed FeaturePython)
  Dunit = g/cm3
  Dvalue = 0.00249343
  Group = -> [C_element019,H_element018]
  conduct = 2
  density = 1
  expand = 3
  formula = G4_BUTANE
  name = G4_BUTANE
  specific = 4
FEATURE [App::DocumentObjectGroupPython] C_element020  label="C_element : 008"  # scripted group (container) (typed FeaturePython)
  n = 4
  ref = C_element
FEATURE [App::DocumentObjectGroupPython] H_element019  label="H_element : 011"  # scripted group (container) (typed FeaturePython)
  n = 10
  ref = H_element
FEATURE [App::DocumentObjectGroupPython] O_element018  label="O_element : 007"  # scripted group (container) (typed FeaturePython)
  n = 1
  ref = O_element
FEATURE [App::DocumentObjectGroupPython] G4_N_BUTYL_ALCOHOL  label="G4_N-BUTYL_ALCOHOL"  # scripted group (container) (typed FeaturePython)
  Dunit = g/cm3
  Dvalue = 0.8098
  Group = -> [C_element020,H_element019,O_element018]
  conduct = 2
  density = 1
  expand = 3
  formula = G4_N-BUTYL_ALCOHOL
  name = G4_N-BUTYL_ALCOHOL
  specific = 4
FEATURE [App::DocumentObjectGroupPython] H_element020  label="H_element : 0.025"  # scripted group (container) (typed FeaturePython)
  n = 0.02468
FEATURE [App::DocumentObjectGroupPython] C_element021  label="C_element : 0.502"  # scripted group (container) (typed FeaturePython)
  n = 0.501611
FEATURE [App::DocumentObjectGroupPython] O_element019  label="O_element : 0.005"  # scripted group (container) (typed FeaturePython)
  n = 0.004527
FEATURE [App::DocumentObjectGroupPython] F_element004  label="F_element : 0.465"  # scripted group (container) (typed FeaturePython)
  n = 0.465209
FEATURE [App::DocumentObjectGroupPython] Si_element001  label="Si_element : 0.004"  # scripted group (container) (typed FeaturePython)
  n = 0.003973
FEATURE [App::DocumentObjectGroupPython] G4_C_552  label="G4_C-552"  # scripted group (container) (typed FeaturePython)
  Dunit = g/cm3
  Dvalue = 1.76
  Group = -> [H_element020,C_element021,O_element019,F_element004,Si_element001]
  conduct = 2
  density = 1
  expand = 3
  formula = G4_C-552
  name = G4_C-552
  specific = 4
FEATURE [App::DocumentObjectGroupPython] Cd_element001  label="Cd_element : 1"  # scripted group (container) (typed FeaturePython)
  n = 1
  ref = Cd_element
FEATURE [App::DocumentObjectGroupPython] Te_element001  label="Te_element : 1"  # scripted group (container) (typed FeaturePython)
  n = 1
  ref = Te_element
FEATURE [App::DocumentObjectGroupPython] G4_CADMIUM_TELLURIDE  # scripted group (container) (typed FeaturePython)
  Dunit = g/cm3
  Dvalue = 6.2
  Group = -> [Cd_element001,Te_element001]
  conduct = 2
  density = 1
  expand = 3
  formula = G4_CADMIUM_TELLURIDE
  name = G4_CADMIUM_TELLURIDE
  specific = 4
FEATURE [App::DocumentObjectGroupPython] Cd_element002  label="Cd_element : 002"  # scripted group (container) (typed FeaturePython)
  n = 1
  ref = Cd_element
FEATURE [App::DocumentObjectGroupPython] W_element001  label="W_element : 1"  # scripted group (container) (typed FeaturePython)
  n = 1
  ref = W_element
FEATURE [App::DocumentObjectGroupPython] O_element020  label="O_element : 008"  # scripted group (container) (typed FeaturePython)
  n = 4
  ref = O_element
FEATURE [App::DocumentObjectGroupPython] G4_CADMIUM_TUNGSTATE  # scripted group (container) (typed FeaturePython)
  Dunit = g/cm3
  Dvalue = 7.9
  Group = -> [Cd_element002,W_element001,O_element020]
  conduct = 2
  density = 1
  expand = 3
  formula = G4_CADMIUM_TUNGSTATE
  name = G4_CADMIUM_TUNGSTATE
  specific = 4
FEATURE [App::DocumentObjectGroupPython] Ca_element005  label="Ca_element : 1"  # scripted group (container) (typed FeaturePython)
  n = 1
  ref = Ca_element
FEATURE [App::DocumentObjectGroupPython] C_element022  label="C_element : 009"  # scripted group (container) (typed FeaturePython)
  n = 1
  ref = C_element
FEATURE [App::DocumentObjectGroupPython] O_element021  label="O_element : 009"  # scripted group (container) (typed FeaturePython)
  n = 3
  ref = O_element
FEATURE [App::DocumentObjectGroupPython] G4_CALCIUM_CARBONATE  # scripted group (container) (typed FeaturePython)
  Dunit = g/cm3
  Dvalue = 2.8
  Group = -> [Ca_element005,C_element022,O_element021]
  conduct = 2
  density = 1
  expand = 3
  formula = G4_CALCIUM_CARBONATE
  name = G4_CALCIUM_CARBONATE
  specific = 4
FEATURE [App::DocumentObjectGroupPython] Ca_element006  label="Ca_element : 002"  # scripted group (container) (typed FeaturePython)
  n = 1
  ref = Ca_element
FEATURE [App::DocumentObjectGroupPython] F_element005  label="F_element : 003"  # scripted group (container) (typed FeaturePython)
  n = 2
  ref = F_element
FEATURE [App::DocumentObjectGroupPython] G4_CALCIUM_FLUORIDE  # scripted group (container) (typed FeaturePython)
  Dunit = g/cm3
  Dvalue = 3.18
  Group = -> [Ca_element006,F_element005]
  conduct = 2
  density = 1
  expand = 3
  formula = G4_CALCIUM_FLUORIDE
  name = G4_CALCIUM_FLUORIDE
  specific = 4
FEATURE [App::DocumentObjectGroupPython] Ca_element007  label="Ca_element : 003"  # scripted group (container) (typed FeaturePython)
  n = 1
  ref = Ca_element
FEATURE [App::DocumentObjectGroupPython] O_element022  label="O_element : 010"  # scripted group (container) (typed FeaturePython)
  n = 1
  ref = O_element
FEATURE [App::DocumentObjectGroupPython] G4_CALCIUM_OXIDE  # scripted group (container) (typed FeaturePython)
  Dunit = g/cm3
  Dvalue = 3.3
  Group = -> [Ca_element007,O_element022]
  conduct = 2
  density = 1
  expand = 3
  formula = G4_CALCIUM_OXIDE
  name = G4_CALCIUM_OXIDE
  specific = 4
FEATURE [App::DocumentObjectGroupPython] Ca_element008  label="Ca_element : 004"  # scripted group (container) (typed FeaturePython)
  n = 1
  ref = Ca_element
FEATURE [App::DocumentObjectGroupPython] S_element007  label="S_element : 002"  # scripted group (container) (typed FeaturePython)
  n = 1
  ref = S_element
FEATURE [App::DocumentObjectGroupPython] O_element023  label="O_element : 011"  # scripted group (container) (typed FeaturePython)
  n = 4
  ref = O_element
FEATURE [App::DocumentObjectGroupPython] G4_CALCIUM_SULFATE  # scripted group (container) (typed FeaturePython)
  Dunit = g/cm3
  Dvalue = 2.96
  Group = -> [Ca_element008,S_element007,O_element023]
  conduct = 2
  density = 1
  expand = 3
  formula = G4_CALCIUM_SULFATE
  name = G4_CALCIUM_SULFATE
  specific = 4
FEATURE [App::DocumentObjectGroupPython] Ca_element009  label="Ca_element : 005"  # scripted group (container) (typed FeaturePython)
  n = 1
  ref = Ca_element
FEATURE [App::DocumentObjectGroupPython] W_element002  label="W_element : 002"  # scripted group (container) (typed FeaturePython)
  n = 1
  ref = W_element
FEATURE [App::DocumentObjectGroupPython] O_element024  label="O_element : 012"  # scripted group (container) (typed FeaturePython)
  n = 4
  ref = O_element
FEATURE [App::DocumentObjectGroupPython] G4_CALCIUM_TUNGSTATE  # scripted group (container) (typed FeaturePython)
  Dunit = g/cm3
  Dvalue = 6.062
  Group = -> [Ca_element009,W_element002,O_element024]
  conduct = 2
  density = 1
  expand = 3
  formula = G4_CALCIUM_TUNGSTATE
  name = G4_CALCIUM_TUNGSTATE
  specific = 4
FEATURE [App::DocumentObjectGroupPython] C_element023  label="C_element : 010"  # scripted group (container) (typed FeaturePython)
  n = 1
  ref = C_element
FEATURE [App::DocumentObjectGroupPython] O_element025  label="O_element : 013"  # scripted group (container) (typed FeaturePython)
  n = 2
  ref = O_element
FEATURE [App::DocumentObjectGroupPython] G4_CARBON_DIOXIDE  # scripted group (container) (typed FeaturePython)
  Dunit = g/cm3
  Dvalue = 0.00184212
  Group = -> [C_element023,O_element025]
  conduct = 2
  density = 1
  expand = 3
  formula = G4_CARBON_DIOXIDE
  name = G4_CARBON_DIOXIDE
  specific = 4
FEATURE [App::DocumentObjectGroupPython] C_element024  label="C_element : 011"  # scripted group (container) (typed FeaturePython)
  n = 1
  ref = C_element
FEATURE [App::DocumentObjectGroupPython] Cl_element004  label="Cl_element : 4"  # scripted group (container) (typed FeaturePython)
  n = 4
  ref = Cl_element
FEATURE [App::DocumentObjectGroupPython] G4_CARBON_TETRACHLORIDE  # scripted group (container) (typed FeaturePython)
  Dunit = g/cm3
  Dvalue = 1.594
  Group = -> [C_element024,Cl_element004]
  conduct = 2
  density = 1
  expand = 3
  formula = G4_CARBON_TETRACHLORIDE
  name = G4_CARBON_TETRACHLORIDE
  specific = 4
FEATURE [App::DocumentObjectGroupPython] C_element025  label="C_element : 012"  # scripted group (container) (typed FeaturePython)
  n = 6
  ref = C_element
FEATURE [App::DocumentObjectGroupPython] H_element021  label="H_element : 012"  # scripted group (container) (typed FeaturePython)
  n = 10
  ref = H_element
FEATURE [App::DocumentObjectGroupPython] O_element026  label="O_element : 5"  # scripted group (container) (typed FeaturePython)
  n = 5
  ref = O_element
FEATURE [App::DocumentObjectGroupPython] G4_CELLULOSE_CELLOPHANE  # scripted group (container) (typed FeaturePython)
  Dunit = g/cm3
  Dvalue = 1.42
  Group = -> [C_element025,H_element021,O_element026]
  conduct = 2
  density = 1
  expand = 3
  formula = G4_CELLULOSE_CELLOPHANE
  name = G4_CELLULOSE_CELLOPHANE
  specific = 4
FEATURE [App::DocumentObjectGroupPython] H_element022  label="H_element : 0.067"  # scripted group (container) (typed FeaturePython)
  n = 0.067125
FEATURE [App::DocumentObjectGroupPython] C_element026  label="C_element : 0.545"  # scripted group (container) (typed FeaturePython)
  n = 0.545403
FEATURE [App::DocumentObjectGroupPython] O_element027  label="O_element : 0.387"  # scripted group (container) (typed FeaturePython)
  n = 0.387472
FEATURE [App::DocumentObjectGroupPython] G4_CELLULOSE_BUTYRATE  # scripted group (container) (typed FeaturePython)
  Dunit = g/cm3
  Dvalue = 1.2
  Group = -> [H_element022,C_element026,O_element027]
  conduct = 2
  density = 1
  expand = 3
  formula = G4_CELLULOSE_BUTYRATE
  name = G4_CELLULOSE_BUTYRATE
  specific = 4
FEATURE [App::DocumentObjectGroupPython] H_element023  label="H_element : 0.029"  # scripted group (container) (typed FeaturePython)
  n = 0.029216
FEATURE [App::DocumentObjectGroupPython] C_element027  label="C_element : 0.271"  # scripted group (container) (typed FeaturePython)
  n = 0.271296
FEATURE [App::DocumentObjectGroupPython] N_element013  label="N_element : 0.121"  # scripted group (container) (typed FeaturePython)
  n = 0.121276
FEATURE [App::DocumentObjectGroupPython] O_element028  label="O_element : 0.578"  # scripted group (container) (typed FeaturePython)
  n = 0.578212
FEATURE [App::DocumentObjectGroupPython] G4_CELLULOSE_NITRATE  # scripted group (container) (typed FeaturePython)
  Dunit = g/cm3
  Dvalue = 1.49
  Group = -> [H_element023,C_element027,N_element013,O_element028]
  conduct = 2
  density = 1
  expand = 3
  formula = G4_CELLULOSE_NITRATE
  name = G4_CELLULOSE_NITRATE
  specific = 4
FEATURE [App::DocumentObjectGroupPython] H_element024  label="H_element : 0.108"  # scripted group (container) (typed FeaturePython)
  n = 0.107596
FEATURE [App::DocumentObjectGroupPython] N_element014  label="N_element : 0.001"  # scripted group (container) (typed FeaturePython)
  n = 0.0008
FEATURE [App::DocumentObjectGroupPython] O_element029  label="O_element : 0.875"  # scripted group (container) (typed FeaturePython)
  n = 0.874976
FEATURE [App::DocumentObjectGroupPython] S_element008  label="S_element : 0.015"  # scripted group (container) (typed FeaturePython)
  n = 0.014627
FEATURE [App::DocumentObjectGroupPython] Ce_element001  label="Ce_element : 0.002"  # scripted group (container) (typed FeaturePython)
  n = 0.002001
FEATURE [App::DocumentObjectGroupPython] G4_CERIC_SULFATE  # scripted group (container) (typed FeaturePython)
  Dunit = g/cm3
  Dvalue = 1.03
  Group = -> [H_element024,N_element014,O_element029,S_element008,Ce_element001]
  conduct = 2
  density = 1
  expand = 3
  formula = G4_CERIC_SULFATE
  name = G4_CERIC_SULFATE
  specific = 4
FEATURE [App::DocumentObjectGroupPython] Cs_element001  label="Cs_element : 1"  # scripted group (container) (typed FeaturePython)
  n = 1
  ref = Cs_element
FEATURE [App::DocumentObjectGroupPython] F_element006  label="F_element : 1"  # scripted group (container) (typed FeaturePython)
  n = 1
  ref = F_element
FEATURE [App::DocumentObjectGroupPython] G4_CESIUM_FLUORIDE  # scripted group (container) (typed FeaturePython)
  Dunit = g/cm3
  Dvalue = 4.115
  Group = -> [Cs_element001,F_element006]
  conduct = 2
  density = 1
  expand = 3
  formula = G4_CESIUM_FLUORIDE
  name = G4_CESIUM_FLUORIDE
  specific = 4
FEATURE [App::DocumentObjectGroupPython] Cs_element002  label="Cs_element : 002"  # scripted group (container) (typed FeaturePython)
  n = 1
  ref = Cs_element
FEATURE [App::DocumentObjectGroupPython] I_element001  label="I_element : 1"  # scripted group (container) (typed FeaturePython)
  n = 1
  ref = I_element
FEATURE [App::DocumentObjectGroupPython] G4_CESIUM_IODIDE  # scripted group (container) (typed FeaturePython)
  Dunit = g/cm3
  Dvalue = 4.51
  Group = -> [Cs_element002,I_element001]
  conduct = 2
  density = 1
  expand = 3
  formula = G4_CESIUM_IODIDE
  name = G4_CESIUM_IODIDE
  specific = 4
FEATURE [App::DocumentObjectGroupPython] C_element028  label="C_element : 013"  # scripted group (container) (typed FeaturePython)
  n = 6
  ref = C_element
FEATURE [App::DocumentObjectGroupPython] H_element025  label="H_element : 013"  # scripted group (container) (typed FeaturePython)
  n = 5
  ref = H_element
FEATURE [App::DocumentObjectGroupPython] Cl_element005  label="Cl_element : 1"  # scripted group (container) (typed FeaturePython)
  n = 1
  ref = Cl_element
FEATURE [App::DocumentObjectGroupPython] G4_CHLOROBENZENE  # scripted group (container) (typed FeaturePython)
  Dunit = g/cm3
  Dvalue = 1.1058
  Group = -> [C_element028,H_element025,Cl_element005]
  conduct = 2
  density = 1
  expand = 3
  formula = G4_CHLOROBENZENE
  name = G4_CHLOROBENZENE
  specific = 4
FEATURE [App::DocumentObjectGroupPython] C_element029  label="C_element : 014"  # scripted group (container) (typed FeaturePython)
  n = 1
  ref = C_element
FEATURE [App::DocumentObjectGroupPython] H_element026  label="H_element : 1"  # scripted group (container) (typed FeaturePython)
  n = 1
  ref = H_element
FEATURE [App::DocumentObjectGroupPython] Cl_element006  label="Cl_element : 3"  # scripted group (container) (typed FeaturePython)
  n = 3
  ref = Cl_element
FEATURE [App::DocumentObjectGroupPython] G4_CHLOROFORM  # scripted group (container) (typed FeaturePython)
  Dunit = g/cm3
  Dvalue = 1.4832
  Group = -> [C_element029,H_element026,Cl_element006]
  conduct = 2
  density = 1
  expand = 3
  formula = G4_CHLOROFORM
  name = G4_CHLOROFORM
  specific = 4
FEATURE [App::DocumentObjectGroupPython] H_element027  label="H_element : 0.010"  # scripted group (container) (typed FeaturePython)
  n = 0.01
FEATURE [App::DocumentObjectGroupPython] C_element030  label="C_element : 0.001"  # scripted group (container) (typed FeaturePython)
  n = 0.001
FEATURE [App::DocumentObjectGroupPython] O_element030  label="O_element : 0.529"  # scripted group (container) (typed FeaturePython)
  n = 0.529107
FEATURE [App::DocumentObjectGroupPython] Na_element005  label="Na_element : 0.016"  # scripted group (container) (typed FeaturePython)
  n = 0.016
FEATURE [App::DocumentObjectGroupPython] Mg_element003  label="Mg_element : 0.004"  # scripted group (container) (typed FeaturePython)
  n = 0.002
FEATURE [App::DocumentObjectGroupPython] Al_element002  label="Al_element : 0.034"  # scripted group (container) (typed FeaturePython)
  n = 0.033872
FEATURE [App::DocumentObjectGroupPython] Si_element002  label="Si_element : 0.337"  # scripted group (container) (typed FeaturePython)
  n = 0.337021
FEATURE [App::DocumentObjectGroupPython] K_element003  label="K_element : 0.013"  # scripted group (container) (typed FeaturePython)
  n = 0.013
FEATURE [App::DocumentObjectGroupPython] Ca_element010  label="Ca_element : 0.044"  # scripted group (container) (typed FeaturePython)
  n = 0.044
FEATURE [App::DocumentObjectGroupPython] Fe_element002  label="Fe_element : 0.014"  # scripted group (container) (typed FeaturePython)
  n = 0.014
FEATURE [App::DocumentObjectGroupPython] G4_CONCRETE  # scripted group (container) (typed FeaturePython)
  Dunit = g/cm3
  Dvalue = 2.3
  Group = -> [H_element027,C_element030,O_element030,Na_element005,Mg_element003,Al_element002,Si_element002,K_element003,Ca_element010,Fe_element002]
  conduct = 2
  density = 1
  expand = 3
  formula = G4_CONCRETE
  name = G4_CONCRETE
  specific = 4
FEATURE [App::DocumentObjectGroupPython] C_element031  label="C_element : 015"  # scripted group (container) (typed FeaturePython)
  n = 6
  ref = C_element
FEATURE [App::DocumentObjectGroupPython] H_element028  label="H_element : 12"  # scripted group (container) (typed FeaturePython)
  n = 12
  ref = H_element
FEATURE [App::DocumentObjectGroupPython] G4_CYCLOHEXANE  # scripted group (container) (typed FeaturePython)
  Dunit = g/cm3
  Dvalue = 0.779
  Group = -> [C_element031,H_element028]
  conduct = 2
  density = 1
  expand = 3
  formula = G4_CYCLOHEXANE
  name = G4_CYCLOHEXANE
  specific = 4
FEATURE [App::DocumentObjectGroupPython] C_element032  label="C_element : 016"  # scripted group (container) (typed FeaturePython)
  n = 6
  ref = C_element
FEATURE [App::DocumentObjectGroupPython] H_element029  label="H_element : 4"  # scripted group (container) (typed FeaturePython)
  n = 4
  ref = H_element
FEATURE [App::DocumentObjectGroupPython] Cl_element007  label="Cl_element : 2"  # scripted group (container) (typed FeaturePython)
  n = 2
  ref = Cl_element
FEATURE [App::DocumentObjectGroupPython] G4_1_2_DICHLOROBENZENE  label="G4_1.2-DICHLOROBENZENE"  # scripted group (container) (typed FeaturePython)
  Dunit = g/cm3
  Dvalue = 1.3048
  Group = -> [C_element032,H_element029,Cl_element007]
  conduct = 2
  density = 1
  expand = 3
  formula = G4_1.2-DICHLOROBENZENE
  name = G4_1.2-DICHLOROBENZENE
  specific = 4
FEATURE [App::DocumentObjectGroupPython] C_element033  label="C_element : 017"  # scripted group (container) (typed FeaturePython)
  n = 4
  ref = C_element
FEATURE [App::DocumentObjectGroupPython] H_element030  label="H_element : 8"  # scripted group (container) (typed FeaturePython)
  n = 8
  ref = H_element
FEATURE [App::DocumentObjectGroupPython] O_element031  label="O_element : 014"  # scripted group (container) (typed FeaturePython)
  n = 1
  ref = O_element
FEATURE [App::DocumentObjectGroupPython] Cl_element008  label="Cl_element : 005"  # scripted group (container) (typed FeaturePython)
  n = 2
  ref = Cl_element
FEATURE [App::DocumentObjectGroupPython] G4_DICHLORODIETHYL_ETHER  # scripted group (container) (typed FeaturePython)
  Dunit = g/cm3
  Dvalue = 1.2199
  Group = -> [C_element033,H_element030,O_element031,Cl_element008]
  conduct = 2
  density = 1
  expand = 3
  formula = G4_DICHLORODIETHYL_ETHER
  name = G4_DICHLORODIETHYL_ETHER
  specific = 4
FEATURE [App::DocumentObjectGroupPython] C_element034  label="C_element : 018"  # scripted group (container) (typed FeaturePython)
  n = 2
  ref = C_element
FEATURE [App::DocumentObjectGroupPython] H_element031  label="H_element : 014"  # scripted group (container) (typed FeaturePython)
  n = 4
  ref = H_element
FEATURE [App::DocumentObjectGroupPython] Cl_element009  label="Cl_element : 006"  # scripted group (container) (typed FeaturePython)
  n = 2
  ref = Cl_element
FEATURE [App::DocumentObjectGroupPython] G4_1_2_DICHLOROETHANE  label="G4_1.2-DICHLOROETHANE"  # scripted group (container) (typed FeaturePython)
  Dunit = g/cm3
  Dvalue = 1.2351
  Group = -> [C_element034,H_element031,Cl_element009]
  conduct = 2
  density = 1
  expand = 3
  formula = G4_1.2-DICHLOROETHANE
  name = G4_1.2-DICHLOROETHANE
  specific = 4
FEATURE [App::DocumentObjectGroupPython] C_element035  label="C_element : 019"  # scripted group (container) (typed FeaturePython)
  n = 4
  ref = C_element
FEATURE [App::DocumentObjectGroupPython] H_element032  label="H_element : 015"  # scripted group (container) (typed FeaturePython)
  n = 10
  ref = H_element
FEATURE [App::DocumentObjectGroupPython] O_element032  label="O_element : 015"  # scripted group (container) (typed FeaturePython)
  n = 1
  ref = O_element
FEATURE [App::DocumentObjectGroupPython] G4_DIETHYL_ETHER  # scripted group (container) (typed FeaturePython)
  Dunit = g/cm3
  Dvalue = 0.71378
  Group = -> [C_element035,H_element032,O_element032]
  conduct = 2
  density = 1
  expand = 3
  formula = G4_DIETHYL_ETHER
  name = G4_DIETHYL_ETHER
  specific = 4
FEATURE [App::DocumentObjectGroupPython] C_element036  label="C_element : 020"  # scripted group (container) (typed FeaturePython)
  n = 3
  ref = C_element
FEATURE [App::DocumentObjectGroupPython] H_element033  label="H_element : 016"  # scripted group (container) (typed FeaturePython)
  n = 7
  ref = H_element
FEATURE [App::DocumentObjectGroupPython] N_element015  label="N_element : 008"  # scripted group (container) (typed FeaturePython)
  n = 1
  ref = N_element
FEATURE [App::DocumentObjectGroupPython] O_element033  label="O_element : 016"  # scripted group (container) (typed FeaturePython)
  n = 1
  ref = O_element
FEATURE [App::DocumentObjectGroupPython] G4_N_N_DIMETHYL_FORMAMIDE  label="G4_N.N-DIMETHYL_FORMAMIDE"  # scripted group (container) (typed FeaturePython)
  Dunit = g/cm3
  Dvalue = 0.9487
  Group = -> [C_element036,H_element033,N_element015,O_element033]
  conduct = 2
  density = 1
  expand = 3
  formula = G4_N.N-DIMETHYL_FORMAMIDE
  name = G4_N.N-DIMETHYL_FORMAMIDE
  specific = 4
FEATURE [App::DocumentObjectGroupPython] C_element037  label="C_element : 021"  # scripted group (container) (typed FeaturePython)
  n = 2
  ref = C_element
FEATURE [App::DocumentObjectGroupPython] H_element034  label="H_element : 017"  # scripted group (container) (typed FeaturePython)
  n = 6
  ref = H_element
FEATURE [App::DocumentObjectGroupPython] O_element034  label="O_element : 017"  # scripted group (container) (typed FeaturePython)
  n = 1
  ref = O_element
FEATURE [App::DocumentObjectGroupPython] S_element009  label="S_element : 003"  # scripted group (container) (typed FeaturePython)
  n = 1
  ref = S_element
FEATURE [App::DocumentObjectGroupPython] G4_DIMETHYL_SULFOXIDE  # scripted group (container) (typed FeaturePython)
  Dunit = g/cm3
  Dvalue = 1.1014
  Group = -> [C_element037,H_element034,O_element034,S_element009]
  conduct = 2
  density = 1
  expand = 3
  formula = G4_DIMETHYL_SULFOXIDE
  name = G4_DIMETHYL_SULFOXIDE
  specific = 4
FEATURE [App::DocumentObjectGroupPython] C_element038  label="C_element : 022"  # scripted group (container) (typed FeaturePython)
  n = 2
  ref = C_element
FEATURE [App::DocumentObjectGroupPython] H_element035  label="H_element : 018"  # scripted group (container) (typed FeaturePython)
  n = 6
  ref = H_element
FEATURE [App::DocumentObjectGroupPython] G4_ETHANE  # scripted group (container) (typed FeaturePython)
  Dunit = g/cm3
  Dvalue = 0.00125324
  Group = -> [C_element038,H_element035]
  conduct = 2
  density = 1
  expand = 3
  formula = G4_ETHANE
  name = G4_ETHANE
  specific = 4
FEATURE [App::DocumentObjectGroupPython] C_element039  label="C_element : 023"  # scripted group (container) (typed FeaturePython)
  n = 2
  ref = C_element
FEATURE [App::DocumentObjectGroupPython] H_element036  label="H_element : 019"  # scripted group (container) (typed FeaturePython)
  n = 6
  ref = H_element
FEATURE [App::DocumentObjectGroupPython] O_element035  label="O_element : 018"  # scripted group (container) (typed FeaturePython)
  n = 1
  ref = O_element
FEATURE [App::DocumentObjectGroupPython] G4_ETHYL_ALCOHOL  # scripted group (container) (typed FeaturePython)
  Dunit = g/cm3
  Dvalue = 0.7893
  Group = -> [C_element039,H_element036,O_element035]
  conduct = 2
  density = 1
  expand = 3
  formula = G4_ETHYL_ALCOHOL
  name = G4_ETHYL_ALCOHOL
  specific = 4
FEATURE [App::DocumentObjectGroupPython] H_element037  label="H_element : 0.090"  # scripted group (container) (typed FeaturePython)
  n = 0.090027
FEATURE [App::DocumentObjectGroupPython] C_element040  label="C_element : 0.585"  # scripted group (container) (typed FeaturePython)
  n = 0.585182
FEATURE [App::DocumentObjectGroupPython] O_element036  label="O_element : 0.325"  # scripted group (container) (typed FeaturePython)
  n = 0.324791
FEATURE [App::DocumentObjectGroupPython] G4_ETHYL_CELLULOSE  # scripted group (container) (typed FeaturePython)
  Dunit = g/cm3
  Dvalue = 1.13
  Group = -> [H_element037,C_element040,O_element036]
  conduct = 2
  density = 1
  expand = 3
  formula = G4_ETHYL_CELLULOSE
  name = G4_ETHYL_CELLULOSE
  specific = 4
FEATURE [App::DocumentObjectGroupPython] C_element041  label="C_element : 024"  # scripted group (container) (typed FeaturePython)
  n = 2
  ref = C_element
FEATURE [App::DocumentObjectGroupPython] H_element038  label="H_element : 020"  # scripted group (container) (typed FeaturePython)
  n = 4
  ref = H_element
FEATURE [App::DocumentObjectGroupPython] G4_ETHYLENE  # scripted group (container) (typed FeaturePython)
  Dunit = g/cm3
  Dvalue = 0.00117497
  Group = -> [C_element041,H_element038]
  conduct = 2
  density = 1
  expand = 3
  formula = G4_ETHYLENE
  name = G4_ETHYLENE
  specific = 4
FEATURE [App::DocumentObjectGroupPython] H_element039  label="H_element : 0.096"  # scripted group (container) (typed FeaturePython)
  n = 0.096
FEATURE [App::DocumentObjectGroupPython] C_element042  label="C_element : 0.195"  # scripted group (container) (typed FeaturePython)
  n = 0.195
FEATURE [App::DocumentObjectGroupPython] N_element016  label="N_element : 0.057"  # scripted group (container) (typed FeaturePython)
  n = 0.057
FEATURE [App::DocumentObjectGroupPython] O_element037  label="O_element : 0.646"  # scripted group (container) (typed FeaturePython)
  n = 0.646
FEATURE [App::DocumentObjectGroupPython] Na_element006  label="Na_element : 0.017"  # scripted group (container) (typed FeaturePython)
  n = 0.001
FEATURE [App::DocumentObjectGroupPython] P_element005  label="P_element : 0.104"  # scripted group (container) (typed FeaturePython)
  n = 0.001
FEATURE [App::DocumentObjectGroupPython] S_element010  label="S_element : 0.016"  # scripted group (container) (typed FeaturePython)
  n = 0.003
FEATURE [App::DocumentObjectGroupPython] Cl_element010  label="Cl_element : 0.005"  # scripted group (container) (typed FeaturePython)
  n = 0.001
FEATURE [App::DocumentObjectGroupPython] G4_EYE_LENS_ICRP  # scripted group (container) (typed FeaturePython)
  Dunit = g/cm3
  Dvalue = 1.07
  Group = -> [H_element039,C_element042,N_element016,O_element037,Na_element006,P_element005,S_element010,Cl_element010]
  conduct = 2
  density = 1
  expand = 3
  formula = G4_EYE_LENS_ICRP
  name = G4_EYE_LENS_ICRP
  specific = 4
FEATURE [App::DocumentObjectGroupPython] Fe_element003  label="Fe_element : 2"  # scripted group (container) (typed FeaturePython)
  n = 2
  ref = Fe_element
FEATURE [App::DocumentObjectGroupPython] O_element038  label="O_element : 019"  # scripted group (container) (typed FeaturePython)
  n = 3
  ref = O_element
FEATURE [App::DocumentObjectGroupPython] G4_FERRIC_OXIDE  # scripted group (container) (typed FeaturePython)
  Dunit = g/cm3
  Dvalue = 5.2
  Group = -> [Fe_element003,O_element038]
  conduct = 2
  density = 1
  expand = 3
  formula = G4_FERRIC_OXIDE
  name = G4_FERRIC_OXIDE
  specific = 4
FEATURE [App::DocumentObjectGroupPython] Fe_element004  label="Fe_element : 1"  # scripted group (container) (typed FeaturePython)
  n = 1
  ref = Fe_element
FEATURE [App::DocumentObjectGroupPython] B_element003  label="B_element : 1"  # scripted group (container) (typed FeaturePython)
  n = 1
  ref = B_element
FEATURE [App::DocumentObjectGroupPython] G4_FERROBORIDE  # scripted group (container) (typed FeaturePython)
  Dunit = g/cm3
  Dvalue = 7.15
  Group = -> [Fe_element004,B_element003]
  conduct = 2
  density = 1
  expand = 3
  formula = G4_FERROBORIDE
  name = G4_FERROBORIDE
  specific = 4
FEATURE [App::DocumentObjectGroupPython] Fe_element005  label="Fe_element : 003"  # scripted group (container) (typed FeaturePython)
  n = 1
  ref = Fe_element
FEATURE [App::DocumentObjectGroupPython] O_element039  label="O_element : 020"  # scripted group (container) (typed FeaturePython)
  n = 1
  ref = O_element
FEATURE [App::DocumentObjectGroupPython] G4_FERROUS_OXIDE  # scripted group (container) (typed FeaturePython)
  Dunit = g/cm3
  Dvalue = 5.7
  Group = -> [Fe_element005,O_element039]
  conduct = 2
  density = 1
  expand = 3
  formula = G4_FERROUS_OXIDE
  name = G4_FERROUS_OXIDE
  specific = 4
FEATURE [App::DocumentObjectGroupPython] H_element040  label="H_element : 0.115"  # scripted group (container) (typed FeaturePython)
  n = 0.108259
FEATURE [App::DocumentObjectGroupPython] N_element017  label="N_element : 0.000"  # scripted group (container) (typed FeaturePython)
  n = 2.7e-05
FEATURE [App::DocumentObjectGroupPython] O_element040  label="O_element : 0.879"  # scripted group (container) (typed FeaturePython)
  n = 0.878636
FEATURE [App::DocumentObjectGroupPython] Na_element007  label="Na_element : 0.000"  # scripted group (container) (typed FeaturePython)
  n = 2.2e-05
FEATURE [App::DocumentObjectGroupPython] S_element011  label="S_element : 0.013"  # scripted group (container) (typed FeaturePython)
  n = 0.012968
FEATURE [App::DocumentObjectGroupPython] Cl_element011  label="Cl_element : 0.000"  # scripted group (container) (typed FeaturePython)
  n = 3.4e-05
FEATURE [App::DocumentObjectGroupPython] Fe_element006  label="Fe_element : 0.000"  # scripted group (container) (typed FeaturePython)
  n = 5.4e-05
FEATURE [App::DocumentObjectGroupPython] G4_FERROUS_SULFATE  # scripted group (container) (typed FeaturePython)
  Dunit = g/cm3
  Dvalue = 1.024
  Group = -> [H_element040,N_element017,O_element040,Na_element007,S_element011,Cl_element011,Fe_element006]
  conduct = 2
  density = 1
  expand = 3
  formula = G4_FERROUS_SULFATE
  name = G4_FERROUS_SULFATE
  specific = 4
FEATURE [App::DocumentObjectGroupPython] C_element043  label="C_element : 0.099"  # scripted group (container) (typed FeaturePython)
  n = 0.099335
FEATURE [App::DocumentObjectGroupPython] F_element007  label="F_element : 0.314"  # scripted group (container) (typed FeaturePython)
  n = 0.314247
FEATURE [App::DocumentObjectGroupPython] Cl_element012  label="Cl_element : 0.586"  # scripted group (container) (typed FeaturePython)
  n = 0.586418
FEATURE [App::DocumentObjectGroupPython] G4_FREON_12  label="G4_FREON-12"  # scripted group (container) (typed FeaturePython)
  Dunit = g/cm3
  Dvalue = 1.12
  Group = -> [C_element043,F_element007,Cl_element012]
  conduct = 2
  density = 1
  expand = 3
  formula = G4_FREON-12
  name = G4_FREON-12
  specific = 4
FEATURE [App::DocumentObjectGroupPython] C_element044  label="C_element : 0.057"  # scripted group (container) (typed FeaturePython)
  n = 0.057245
FEATURE [App::DocumentObjectGroupPython] F_element008  label="F_element : 0.181"  # scripted group (container) (typed FeaturePython)
  n = 0.181096
FEATURE [App::DocumentObjectGroupPython] Br_element001  label="Br_element : 0.762"  # scripted group (container) (typed FeaturePython)
  n = 0.761659
FEATURE [App::DocumentObjectGroupPython] G4_FREON_12B2  label="G4_FREON-12B2"  # scripted group (container) (typed FeaturePython)
  Dunit = g/cm3
  Dvalue = 1.8
  Group = -> [C_element044,F_element008,Br_element001]
  conduct = 2
  density = 1
  expand = 3
  formula = G4_FREON-12B2
  name = G4_FREON-12B2
  specific = 4
FEATURE [App::DocumentObjectGroupPython] C_element045  label="C_element : 0.115"  # scripted group (container) (typed FeaturePython)
  n = 0.114983
FEATURE [App::DocumentObjectGroupPython] F_element009  label="F_element : 0.546"  # scripted group (container) (typed FeaturePython)
  n = 0.545621
FEATURE [App::DocumentObjectGroupPython] Cl_element013  label="Cl_element : 0.339"  # scripted group (container) (typed FeaturePython)
  n = 0.339396
FEATURE [App::DocumentObjectGroupPython] G4_FREON_13  label="G4_FREON-13"  # scripted group (container) (typed FeaturePython)
  Dunit = g/cm3
  Dvalue = 0.95
  Group = -> [C_element045,F_element009,Cl_element013]
  conduct = 2
  density = 1
  expand = 3
  formula = G4_FREON-13
  name = G4_FREON-13
  specific = 4
FEATURE [App::DocumentObjectGroupPython] C_element046  label="C_element : 025"  # scripted group (container) (typed FeaturePython)
  n = 1
  ref = C_element
FEATURE [App::DocumentObjectGroupPython] F_element010  label="F_element : 3"  # scripted group (container) (typed FeaturePython)
  n = 3
  ref = F_element
FEATURE [App::DocumentObjectGroupPython] Br_element002  label="Br_element : 1"  # scripted group (container) (typed FeaturePython)
  n = 1
  ref = Br_element
FEATURE [App::DocumentObjectGroupPython] G4_FREON_13B1  label="G4_FREON-13B1"  # scripted group (container) (typed FeaturePython)
  Dunit = g/cm3
  Dvalue = 1.5
  Group = -> [C_element046,F_element010,Br_element002]
  conduct = 2
  density = 1
  expand = 3
  formula = G4_FREON-13B1
  name = G4_FREON-13B1
  specific = 4
FEATURE [App::DocumentObjectGroupPython] C_element047  label="C_element : 0.061"  # scripted group (container) (typed FeaturePython)
  n = 0.061309
FEATURE [App::DocumentObjectGroupPython] F_element011  label="F_element : 0.291"  # scripted group (container) (typed FeaturePython)
  n = 0.290924
FEATURE [App::DocumentObjectGroupPython] I_element002  label="I_element : 0.648"  # scripted group (container) (typed FeaturePython)
  n = 0.647767
FEATURE [App::DocumentObjectGroupPython] G4_FREON_13I1  label="G4_FREON-13I1"  # scripted group (container) (typed FeaturePython)
  Dunit = g/cm3
  Dvalue = 1.8
  Group = -> [C_element047,F_element011,I_element002]
  conduct = 2
  density = 1
  expand = 3
  formula = G4_FREON-13I1
  name = G4_FREON-13I1
  specific = 4
FEATURE [App::DocumentObjectGroupPython] Gd_element001  label="Gd_element : 2"  # scripted group (container) (typed FeaturePython)
  n = 2
  ref = Gd_element
FEATURE [App::DocumentObjectGroupPython] O_element041  label="O_element : 021"  # scripted group (container) (typed FeaturePython)
  n = 2
  ref = O_element
FEATURE [App::DocumentObjectGroupPython] S_element012  label="S_element : 004"  # scripted group (container) (typed FeaturePython)
  n = 1
  ref = S_element
FEATURE [App::DocumentObjectGroupPython] G4_GADOLINIUM_OXYSULFIDE  # scripted group (container) (typed FeaturePython)
  Dunit = g/cm3
  Dvalue = 7.44
  Group = -> [Gd_element001,O_element041,S_element012]
  conduct = 2
  density = 1
  expand = 3
  formula = G4_GADOLINIUM_OXYSULFIDE
  name = G4_GADOLINIUM_OXYSULFIDE
  specific = 4
FEATURE [App::DocumentObjectGroupPython] Ga_element001  label="Ga_element : 1"  # scripted group (container) (typed FeaturePython)
  n = 1
  ref = Ga_element
FEATURE [App::DocumentObjectGroupPython] As_element001  label="As_element : 1"  # scripted group (container) (typed FeaturePython)
  n = 1
  ref = As_element
FEATURE [App::DocumentObjectGroupPython] G4_GALLIUM_ARSENIDE  # scripted group (container) (typed FeaturePython)
  Dunit = g/cm3
  Dvalue = 5.31
  Group = -> [Ga_element001,As_element001]
  conduct = 2
  density = 1
  expand = 3
  formula = G4_GALLIUM_ARSENIDE
  name = G4_GALLIUM_ARSENIDE
  specific = 4
FEATURE [App::DocumentObjectGroupPython] H_element041  label="H_element : 0.081"  # scripted group (container) (typed FeaturePython)
  n = 0.08118
FEATURE [App::DocumentObjectGroupPython] C_element048  label="C_element : 0.416"  # scripted group (container) (typed FeaturePython)
  n = 0.41606
FEATURE [App::DocumentObjectGroupPython] N_element018  label="N_element : 0.111"  # scripted group (container) (typed FeaturePython)
  n = 0.11124
FEATURE [App::DocumentObjectGroupPython] O_element042  label="O_element : 0.381"  # scripted group (container) (typed FeaturePython)
  n = 0.38064
FEATURE [App::DocumentObjectGroupPython] S_element013  label="S_element : 0.011"  # scripted group (container) (typed FeaturePython)
  n = 0.01088
FEATURE [App::DocumentObjectGroupPython] G4_GEL_PHOTO_EMULSION  # scripted group (container) (typed FeaturePython)
  Dunit = g/cm3
  Dvalue = 1.2914
  Group = -> [H_element041,C_element048,N_element018,O_element042,S_element013]
  conduct = 2
  density = 1
  expand = 3
  formula = G4_GEL_PHOTO_EMULSION
  name = G4_GEL_PHOTO_EMULSION
  specific = 4
FEATURE [App::DocumentObjectGroupPython] B_element004  label="B_element : 0.040"  # scripted group (container) (typed FeaturePython)
  n = 0.0400639
FEATURE [App::DocumentObjectGroupPython] O_element043  label="O_element : 0.540"  # scripted group (container) (typed FeaturePython)
  n = 0.539561
FEATURE [App::DocumentObjectGroupPython] Na_element008  label="Na_element : 0.028"  # scripted group (container) (typed FeaturePython)
  n = 0.0281909
FEATURE [App::DocumentObjectGroupPython] Al_element003  label="Al_element : 0.012"  # scripted group (container) (typed FeaturePython)
  n = 0.011644
FEATURE [App::DocumentObjectGroupPython] Si_element003  label="Si_element : 0.377"  # scripted group (container) (typed FeaturePython)
  n = 0.377219
FEATURE [App::DocumentObjectGroupPython] K_element004  label="K_element : 0.014"  # scripted group (container) (typed FeaturePython)
  n = 0.00332099
FEATURE [App::DocumentObjectGroupPython] G4_Pyrex_Glass  # scripted group (container) (typed FeaturePython)
  Dunit = g/cm3
  Dvalue = 2.23
  Group = -> [B_element004,O_element043,Na_element008,Al_element003,Si_element003,K_element004]
  conduct = 2
  density = 1
  expand = 3
  formula = G4_Pyrex_Glass
  name = G4_Pyrex_Glass
  specific = 4
FEATURE [App::DocumentObjectGroupPython] O_element044  label="O_element : 0.156"  # scripted group (container) (typed FeaturePython)
  n = 0.156453
FEATURE [App::DocumentObjectGroupPython] Si_element004  label="Si_element : 0.081"  # scripted group (container) (typed FeaturePython)
  n = 0.080866
FEATURE [App::DocumentObjectGroupPython] Ti_element001  label="Ti_element : 0.008"  # scripted group (container) (typed FeaturePython)
  n = 0.008092
FEATURE [App::DocumentObjectGroupPython] As_element002  label="As_element : 0.003"  # scripted group (container) (typed FeaturePython)
  n = 0.002651
FEATURE [App::DocumentObjectGroupPython] Pb_element001  label="Pb_element : 0.752"  # scripted group (container) (typed FeaturePython)
  n = 0.751938
FEATURE [App::DocumentObjectGroupPython] G4_GLASS_LEAD  # scripted group (container) (typed FeaturePython)
  Dunit = g/cm3
  Dvalue = 6.22
  Group = -> [O_element044,Si_element004,Ti_element001,As_element002,Pb_element001]
  conduct = 2
  density = 1
  expand = 3
  formula = G4_GLASS_LEAD
  name = G4_GLASS_LEAD
  specific = 4
FEATURE [App::DocumentObjectGroupPython] O_element045  label="O_element : 0.460"  # scripted group (container) (typed FeaturePython)
  n = 0.4598
FEATURE [App::DocumentObjectGroupPython] Na_element009  label="Na_element : 0.096"  # scripted group (container) (typed FeaturePython)
  n = 0.0964411
FEATURE [App::DocumentObjectGroupPython] Si_element005  label="Si_element : 0.378"  # scripted group (container) (typed FeaturePython)
  n = 0.336553
FEATURE [App::DocumentObjectGroupPython] Ca_element011  label="Ca_element : 0.107"  # scripted group (container) (typed FeaturePython)
  n = 0.107205
FEATURE [App::DocumentObjectGroupPython] G4_GLASS_PLATE  # scripted group (container) (typed FeaturePython)
  Dunit = g/cm3
  Dvalue = 2.4
  Group = -> [O_element045,Na_element009,Si_element005,Ca_element011]
  conduct = 2
  density = 1
  expand = 3
  formula = G4_GLASS_PLATE
  name = G4_GLASS_PLATE
  specific = 4
FEATURE [App::DocumentObjectGroupPython] C_element049  label="C_element : 026"  # scripted group (container) (typed FeaturePython)
  n = 5
  ref = C_element
FEATURE [App::DocumentObjectGroupPython] H_element042  label="H_element : 021"  # scripted group (container) (typed FeaturePython)
  n = 10
  ref = H_element
FEATURE [App::DocumentObjectGroupPython] N_element019  label="N_element : 2"  # scripted group (container) (typed FeaturePython)
  n = 2
  ref = N_element
FEATURE [App::DocumentObjectGroupPython] O_element046  label="O_element : 022"  # scripted group (container) (typed FeaturePython)
  n = 3
  ref = O_element
FEATURE [App::DocumentObjectGroupPython] G4_GLUTAMINE  # scripted group (container) (typed FeaturePython)
  Dunit = g/cm3
  Dvalue = 1.46
  Group = -> [C_element049,H_element042,N_element019,O_element046]
  conduct = 2
  density = 1
  expand = 3
  formula = G4_GLUTAMINE
  name = G4_GLUTAMINE
  specific = 4
FEATURE [App::DocumentObjectGroupPython] C_element050  label="C_element : 027"  # scripted group (container) (typed FeaturePython)
  n = 3
  ref = C_element
FEATURE [App::DocumentObjectGroupPython] H_element043  label="H_element : 022"  # scripted group (container) (typed FeaturePython)
  n = 8
  ref = H_element
FEATURE [App::DocumentObjectGroupPython] O_element047  label="O_element : 023"  # scripted group (container) (typed FeaturePython)
  n = 3
  ref = O_element
FEATURE [App::DocumentObjectGroupPython] G4_GLYCEROL  # scripted group (container) (typed FeaturePython)
  Dunit = g/cm3
  Dvalue = 1.2613
  Group = -> [C_element050,H_element043,O_element047]
  conduct = 2
  density = 1
  expand = 3
  formula = G4_GLYCEROL
  name = G4_GLYCEROL
  specific = 4
FEATURE [App::DocumentObjectGroupPython] C_element051  label="C_element : 028"  # scripted group (container) (typed FeaturePython)
  n = 5
  ref = C_element
FEATURE [App::DocumentObjectGroupPython] H_element044  label="H_element : 023"  # scripted group (container) (typed FeaturePython)
  n = 5
  ref = H_element
FEATURE [App::DocumentObjectGroupPython] N_element020  label="N_element : 009"  # scripted group (container) (typed FeaturePython)
  n = 5
  ref = N_element
FEATURE [App::DocumentObjectGroupPython] O_element048  label="O_element : 024"  # scripted group (container) (typed FeaturePython)
  n = 1
  ref = O_element
FEATURE [App::DocumentObjectGroupPython] G4_GUANINE  # scripted group (container) (typed FeaturePython)
  Dunit = g/cm3
  Dvalue = 2.2
  Group = -> [C_element051,H_element044,N_element020,O_element048]
  conduct = 2
  density = 1
  expand = 3
  formula = G4_GUANINE
  name = G4_GUANINE
  specific = 4
FEATURE [App::DocumentObjectGroupPython] Ca_element012  label="Ca_element : 006"  # scripted group (container) (typed FeaturePython)
  n = 1
  ref = Ca_element
FEATURE [App::DocumentObjectGroupPython] S_element014  label="S_element : 005"  # scripted group (container) (typed FeaturePython)
  n = 1
  ref = S_element
FEATURE [App::DocumentObjectGroupPython] O_element049  label="O_element : 6"  # scripted group (container) (typed FeaturePython)
  n = 6
  ref = O_element
FEATURE [App::DocumentObjectGroupPython] H_element045  label="H_element : 024"  # scripted group (container) (typed FeaturePython)
  n = 4
  ref = H_element
FEATURE [App::DocumentObjectGroupPython] G4_GYPSUM  # scripted group (container) (typed FeaturePython)
  Dunit = g/cm3
  Dvalue = 2.32
  Group = -> [Ca_element012,S_element014,O_element049,H_element045]
  conduct = 2
  density = 1
  expand = 3
  formula = G4_GYPSUM
  name = G4_GYPSUM
  specific = 4
FEATURE [App::DocumentObjectGroupPython] C_element052  label="C_element : 7"  # scripted group (container) (typed FeaturePython)
  n = 7
  ref = C_element
FEATURE [App::DocumentObjectGroupPython] H_element046  label="H_element : 16"  # scripted group (container) (typed FeaturePython)
  n = 16
  ref = H_element
FEATURE [App::DocumentObjectGroupPython] G4_N_HEPTANE  label="G4_N-HEPTANE"  # scripted group (container) (typed FeaturePython)
  Dunit = g/cm3
  Dvalue = 0.68376
  Group = -> [C_element052,H_element046]
  conduct = 2
  density = 1
  expand = 3
  formula = G4_N-HEPTANE
  name = G4_N-HEPTANE
  specific = 4
FEATURE [App::DocumentObjectGroupPython] C_element053  label="C_element : 029"  # scripted group (container) (typed FeaturePython)
  n = 6
  ref = C_element
FEATURE [App::DocumentObjectGroupPython] H_element047  label="H_element : 14"  # scripted group (container) (typed FeaturePython)
  n = 14
  ref = H_element
FEATURE [App::DocumentObjectGroupPython] G4_N_HEXANE  label="G4_N-HEXANE"  # scripted group (container) (typed FeaturePython)
  Dunit = g/cm3
  Dvalue = 0.6603
  Group = -> [C_element053,H_element047]
  conduct = 2
  density = 1
  expand = 3
  formula = G4_N-HEXANE
  name = G4_N-HEXANE
  specific = 4
FEATURE [App::DocumentObjectGroupPython] C_element054  label="C_element : 22"  # scripted group (container) (typed FeaturePython)
  n = 22
  ref = C_element
FEATURE [App::DocumentObjectGroupPython] H_element048  label="H_element : 025"  # scripted group (container) (typed FeaturePython)
  n = 10
  ref = H_element
FEATURE [App::DocumentObjectGroupPython] N_element021  label="N_element : 010"  # scripted group (container) (typed FeaturePython)
  n = 2
  ref = N_element
FEATURE [App::DocumentObjectGroupPython] O_element050  label="O_element : 025"  # scripted group (container) (typed FeaturePython)
  n = 5
  ref = O_element
FEATURE [App::DocumentObjectGroupPython] G4_KAPTON  # scripted group (container) (typed FeaturePython)
  Dunit = g/cm3
  Dvalue = 1.42
  Group = -> [C_element054,H_element048,N_element021,O_element050]
  conduct = 2
  density = 1
  expand = 3
  formula = G4_KAPTON
  name = G4_KAPTON
  specific = 4
FEATURE [App::DocumentObjectGroupPython] La_element001  label="La_element : 1"  # scripted group (container) (typed FeaturePython)
  n = 1
  ref = La_element
FEATURE [App::DocumentObjectGroupPython] Br_element003  label="Br_element : 002"  # scripted group (container) (typed FeaturePython)
  n = 1
  ref = Br_element
FEATURE [App::DocumentObjectGroupPython] O_element051  label="O_element : 026"  # scripted group (container) (typed FeaturePython)
  n = 1
  ref = O_element
FEATURE [App::DocumentObjectGroupPython] G4_LANTHANUM_OXYBROMIDE  # scripted group (container) (typed FeaturePython)
  Dunit = g/cm3
  Dvalue = 6.28
  Group = -> [La_element001,Br_element003,O_element051]
  conduct = 2
  density = 1
  expand = 3
  formula = G4_LANTHANUM_OXYBROMIDE
  name = G4_LANTHANUM_OXYBROMIDE
  specific = 4
FEATURE [App::DocumentObjectGroupPython] La_element002  label="La_element : 2"  # scripted group (container) (typed FeaturePython)
  n = 2
  ref = La_element
FEATURE [App::DocumentObjectGroupPython] O_element052  label="O_element : 027"  # scripted group (container) (typed FeaturePython)
  n = 2
  ref = O_element
FEATURE [App::DocumentObjectGroupPython] S_element015  label="S_element : 006"  # scripted group (container) (typed FeaturePython)
  n = 1
  ref = S_element
FEATURE [App::DocumentObjectGroupPython] G4_LANTHANUM_OXYSULFIDE  # scripted group (container) (typed FeaturePython)
  Dunit = g/cm3
  Dvalue = 5.86
  Group = -> [La_element002,O_element052,S_element015]
  conduct = 2
  density = 1
  expand = 3
  formula = G4_LANTHANUM_OXYSULFIDE
  name = G4_LANTHANUM_OXYSULFIDE
  specific = 4
FEATURE [App::DocumentObjectGroupPython] O_element053  label="O_element : 0.072"  # scripted group (container) (typed FeaturePython)
  n = 0.071682
FEATURE [App::DocumentObjectGroupPython] Pb_element002  label="Pb_element : 0.928"  # scripted group (container) (typed FeaturePython)
  n = 0.928318
FEATURE [App::DocumentObjectGroupPython] G4_LEAD_OXIDE  # scripted group (container) (typed FeaturePython)
  Dunit = g/cm3
  Dvalue = 9.53
  Group = -> [O_element053,Pb_element002]
  conduct = 2
  density = 1
  expand = 3
  formula = G4_LEAD_OXIDE
  name = G4_LEAD_OXIDE
  specific = 4
FEATURE [App::DocumentObjectGroupPython] Li_element001  label="Li_element : 1"  # scripted group (container) (typed FeaturePython)
  n = 1
  ref = Li_element
FEATURE [App::DocumentObjectGroupPython] N_element022  label="N_element : 011"  # scripted group (container) (typed FeaturePython)
  n = 1
  ref = N_element
FEATURE [App::DocumentObjectGroupPython] H_element049  label="H_element : 026"  # scripted group (container) (typed FeaturePython)
  n = 2
  ref = H_element
FEATURE [App::DocumentObjectGroupPython] G4_LITHIUM_AMIDE  # scripted group (container) (typed FeaturePython)
  Dunit = g/cm3
  Dvalue = 1.178
  Group = -> [Li_element001,N_element022,H_element049]
  conduct = 2
  density = 1
  expand = 3
  formula = G4_LITHIUM_AMIDE
  name = G4_LITHIUM_AMIDE
  specific = 4
FEATURE [App::DocumentObjectGroupPython] Li_element002  label="Li_element : 2"  # scripted group (container) (typed FeaturePython)
  n = 2
  ref = Li_element
FEATURE [App::DocumentObjectGroupPython] C_element055  label="C_element : 030"  # scripted group (container) (typed FeaturePython)
  n = 1
  ref = C_element
FEATURE [App::DocumentObjectGroupPython] O_element054  label="O_element : 028"  # scripted group (container) (typed FeaturePython)
  n = 3
  ref = O_element
FEATURE [App::DocumentObjectGroupPython] G4_LITHIUM_CARBONATE  # scripted group (container) (typed FeaturePython)
  Dunit = g/cm3
  Dvalue = 2.11
  Group = -> [Li_element002,C_element055,O_element054]
  conduct = 2
  density = 1
  expand = 3
  formula = G4_LITHIUM_CARBONATE
  name = G4_LITHIUM_CARBONATE
  specific = 4
FEATURE [App::DocumentObjectGroupPython] Li_element003  label="Li_element : 003"  # scripted group (container) (typed FeaturePython)
  n = 1
  ref = Li_element
FEATURE [App::DocumentObjectGroupPython] F_element012  label="F_element : 004"  # scripted group (container) (typed FeaturePython)
  n = 1
  ref = F_element
FEATURE [App::DocumentObjectGroupPython] G4_LITHIUM_FLUORIDE  # scripted group (container) (typed FeaturePython)
  Dunit = g/cm3
  Dvalue = 2.635
  Group = -> [Li_element003,F_element012]
  conduct = 2
  density = 1
  expand = 3
  formula = G4_LITHIUM_FLUORIDE
  name = G4_LITHIUM_FLUORIDE
  specific = 4
FEATURE [App::DocumentObjectGroupPython] Li_element004  label="Li_element : 004"  # scripted group (container) (typed FeaturePython)
  n = 1
  ref = Li_element
FEATURE [App::DocumentObjectGroupPython] H_element050  label="H_element : 027"  # scripted group (container) (typed FeaturePython)
  n = 1
  ref = H_element
FEATURE [App::DocumentObjectGroupPython] G4_LITHIUM_HYDRIDE  # scripted group (container) (typed FeaturePython)
  Dunit = g/cm3
  Dvalue = 0.82
  Group = -> [Li_element004,H_element050]
  conduct = 2
  density = 1
  expand = 3
  formula = G4_LITHIUM_HYDRIDE
  name = G4_LITHIUM_HYDRIDE
  specific = 4
FEATURE [App::DocumentObjectGroupPython] Li_element005  label="Li_element : 005"  # scripted group (container) (typed FeaturePython)
  n = 1
  ref = Li_element
FEATURE [App::DocumentObjectGroupPython] I_element003  label="I_element : 002"  # scripted group (container) (typed FeaturePython)
  n = 1
  ref = I_element
FEATURE [App::DocumentObjectGroupPython] G4_LITHIUM_IODIDE  # scripted group (container) (typed FeaturePython)
  Dunit = g/cm3
  Dvalue = 3.494
  Group = -> [Li_element005,I_element003]
  conduct = 2
  density = 1
  expand = 3
  formula = G4_LITHIUM_IODIDE
  name = G4_LITHIUM_IODIDE
  specific = 4
FEATURE [App::DocumentObjectGroupPython] Li_element006  label="Li_element : 006"  # scripted group (container) (typed FeaturePython)
  n = 2
  ref = Li_element
FEATURE [App::DocumentObjectGroupPython] O_element055  label="O_element : 029"  # scripted group (container) (typed FeaturePython)
  n = 1
  ref = O_element
FEATURE [App::DocumentObjectGroupPython] G4_LITHIUM_OXIDE  # scripted group (container) (typed FeaturePython)
  Dunit = g/cm3
  Dvalue = 2.013
  Group = -> [Li_element006,O_element055]
  conduct = 2
  density = 1
  expand = 3
  formula = G4_LITHIUM_OXIDE
  name = G4_LITHIUM_OXIDE
  specific = 4
FEATURE [App::DocumentObjectGroupPython] Li_element007  label="Li_element : 007"  # scripted group (container) (typed FeaturePython)
  n = 2
  ref = Li_element
FEATURE [App::DocumentObjectGroupPython] B_element005  label="B_element : 005"  # scripted group (container) (typed FeaturePython)
  n = 4
  ref = B_element
FEATURE [App::DocumentObjectGroupPython] O_element056  label="O_element : 7"  # scripted group (container) (typed FeaturePython)
  n = 7
  ref = O_element
FEATURE [App::DocumentObjectGroupPython] G4_LITHIUM_TETRABORATE  # scripted group (container) (typed FeaturePython)
  Dunit = g/cm3
  Dvalue = 2.44
  Group = -> [Li_element007,B_element005,O_element056]
  conduct = 2
  density = 1
  expand = 3
  formula = G4_LITHIUM_TETRABORATE
  name = G4_LITHIUM_TETRABORATE
  specific = 4
FEATURE [App::DocumentObjectGroupPython] H_element051  label="H_element : 0.105"  # scripted group (container) (typed FeaturePython)
  n = 0.105
FEATURE [App::DocumentObjectGroupPython] C_element056  label="C_element : 0.083"  # scripted group (container) (typed FeaturePython)
  n = 0.083
FEATURE [App::DocumentObjectGroupPython] N_element023  label="N_element : 0.023"  # scripted group (container) (typed FeaturePython)
  n = 0.023
FEATURE [App::DocumentObjectGroupPython] O_element057  label="O_element : 0.779"  # scripted group (container) (typed FeaturePython)
  n = 0.779
FEATURE [App::DocumentObjectGroupPython] Na_element010  label="Na_element : 0.097"  # scripted group (container) (typed FeaturePython)
  n = 0.002
FEATURE [App::DocumentObjectGroupPython] P_element006  label="P_element : 0.105"  # scripted group (container) (typed FeaturePython)
  n = 0.001
FEATURE [App::DocumentObjectGroupPython] S_element016  label="S_element : 0.017"  # scripted group (container) (typed FeaturePython)
  n = 0.002
FEATURE [App::DocumentObjectGroupPython] Cl_element014  label="Cl_element : 0.587"  # scripted group (container) (typed FeaturePython)
  n = 0.003
FEATURE [App::DocumentObjectGroupPython] K_element005  label="K_element : 0.015"  # scripted group (container) (typed FeaturePython)
  n = 0.002
FEATURE [App::DocumentObjectGroupPython] G4_LUNG_ICRP  # scripted group (container) (typed FeaturePython)
  Dunit = g/cm3
  Dvalue = 1.04
  Group = -> [H_element051,C_element056,N_element023,O_element057,Na_element010,P_element006,S_element016,Cl_element014,K_element005]
  conduct = 2
  density = 1
  expand = 3
  formula = G4_LUNG_ICRP
  name = G4_LUNG_ICRP
  specific = 4
FEATURE [App::DocumentObjectGroupPython] H_element052  label="H_element : 0.116"  # scripted group (container) (typed FeaturePython)
  n = 0.114318
FEATURE [App::DocumentObjectGroupPython] C_element057  label="C_element : 0.656"  # scripted group (container) (typed FeaturePython)
  n = 0.655824
FEATURE [App::DocumentObjectGroupPython] O_element058  label="O_element : 0.092"  # scripted group (container) (typed FeaturePython)
  n = 0.0921831
FEATURE [App::DocumentObjectGroupPython] Mg_element004  label="Mg_element : 0.135"  # scripted group (container) (typed FeaturePython)
  n = 0.134792
FEATURE [App::DocumentObjectGroupPython] Ca_element013  label="Ca_element : 0.003"  # scripted group (container) (typed FeaturePython)
  n = 0.002883
FEATURE [App::DocumentObjectGroupPython] G4_M3_WAX  # scripted group (container) (typed FeaturePython)
  Dunit = g/cm3
  Dvalue = 1.05
  Group = -> [H_element052,C_element057,O_element058,Mg_element004,Ca_element013]
  conduct = 2
  density = 1
  expand = 3
  formula = G4_M3_WAX
  name = G4_M3_WAX
  specific = 4
FEATURE [App::DocumentObjectGroupPython] Mg_element005  label="Mg_element : 1"  # scripted group (container) (typed FeaturePython)
  n = 1
  ref = Mg_element
FEATURE [App::DocumentObjectGroupPython] C_element058  label="C_element : 031"  # scripted group (container) (typed FeaturePython)
  n = 1
  ref = C_element
FEATURE [App::DocumentObjectGroupPython] O_element059  label="O_element : 030"  # scripted group (container) (typed FeaturePython)
  n = 3
  ref = O_element
FEATURE [App::DocumentObjectGroupPython] G4_MAGNESIUM_CARBONATE  # scripted group (container) (typed FeaturePython)
  Dunit = g/cm3
  Dvalue = 2.958
  Group = -> [Mg_element005,C_element058,O_element059]
  conduct = 2
  density = 1
  expand = 3
  formula = G4_MAGNESIUM_CARBONATE
  name = G4_MAGNESIUM_CARBONATE
  specific = 4
FEATURE [App::DocumentObjectGroupPython] Mg_element006  label="Mg_element : 002"  # scripted group (container) (typed FeaturePython)
  n = 1
  ref = Mg_element
FEATURE [App::DocumentObjectGroupPython] F_element013  label="F_element : 005"  # scripted group (container) (typed FeaturePython)
  n = 2
  ref = F_element
FEATURE [App::DocumentObjectGroupPython] G4_MAGNESIUM_FLUORIDE  # scripted group (container) (typed FeaturePython)
  Dunit = g/cm3
  Dvalue = 3
  Group = -> [Mg_element006,F_element013]
  conduct = 2
  density = 1
  expand = 3
  formula = G4_MAGNESIUM_FLUORIDE
  name = G4_MAGNESIUM_FLUORIDE
  specific = 4
FEATURE [App::DocumentObjectGroupPython] Mg_element007  label="Mg_element : 003"  # scripted group (container) (typed FeaturePython)
  n = 1
  ref = Mg_element
FEATURE [App::DocumentObjectGroupPython] O_element060  label="O_element : 031"  # scripted group (container) (typed FeaturePython)
  n = 1
  ref = O_element
FEATURE [App::DocumentObjectGroupPython] G4_MAGNESIUM_OXIDE  # scripted group (container) (typed FeaturePython)
  Dunit = g/cm3
  Dvalue = 3.58
  Group = -> [Mg_element007,O_element060]
  conduct = 2
  density = 1
  expand = 3
  formula = G4_MAGNESIUM_OXIDE
  name = G4_MAGNESIUM_OXIDE
  specific = 4
FEATURE [App::DocumentObjectGroupPython] Mg_element008  label="Mg_element : 004"  # scripted group (container) (typed FeaturePython)
  n = 1
  ref = Mg_element
FEATURE [App::DocumentObjectGroupPython] B_element006  label="B_element : 006"  # scripted group (container) (typed FeaturePython)
  n = 4
  ref = B_element
FEATURE [App::DocumentObjectGroupPython] O_element061  label="O_element : 032"  # scripted group (container) (typed FeaturePython)
  n = 7
  ref = O_element
FEATURE [App::DocumentObjectGroupPython] G4_MAGNESIUM_TETRABORATE  # scripted group (container) (typed FeaturePython)
  Dunit = g/cm3
  Dvalue = 2.53
  Group = -> [Mg_element008,B_element006,O_element061]
  conduct = 2
  density = 1
  expand = 3
  formula = G4_MAGNESIUM_TETRABORATE
  name = G4_MAGNESIUM_TETRABORATE
  specific = 4
FEATURE [App::DocumentObjectGroupPython] Hg_element001  label="Hg_element : 1"  # scripted group (container) (typed FeaturePython)
  n = 1
  ref = Hg_element
FEATURE [App::DocumentObjectGroupPython] I_element004  label="I_element : 2"  # scripted group (container) (typed FeaturePython)
  n = 2
  ref = I_element
FEATURE [App::DocumentObjectGroupPython] G4_MERCURIC_IODIDE  # scripted group (container) (typed FeaturePython)
  Dunit = g/cm3
  Dvalue = 6.36
  Group = -> [Hg_element001,I_element004]
  conduct = 2
  density = 1
  expand = 3
  formula = G4_MERCURIC_IODIDE
  name = G4_MERCURIC_IODIDE
  specific = 4
FEATURE [App::DocumentObjectGroupPython] C_element059  label="C_element : 032"  # scripted group (container) (typed FeaturePython)
  n = 1
  ref = C_element
FEATURE [App::DocumentObjectGroupPython] H_element053  label="H_element : 028"  # scripted group (container) (typed FeaturePython)
  n = 4
  ref = H_element
FEATURE [App::DocumentObjectGroupPython] G4_METHANE  # scripted group (container) (typed FeaturePython)
  Dunit = g/cm3
  Dvalue = 0.000667151
  Group = -> [C_element059,H_element053]
  conduct = 2
  density = 1
  expand = 3
  formula = G4_METHANE
  name = G4_METHANE
  specific = 4
FEATURE [App::DocumentObjectGroupPython] C_element060  label="C_element : 033"  # scripted group (container) (typed FeaturePython)
  n = 1
  ref = C_element
FEATURE [App::DocumentObjectGroupPython] H_element054  label="H_element : 029"  # scripted group (container) (typed FeaturePython)
  n = 4
  ref = H_element
FEATURE [App::DocumentObjectGroupPython] O_element062  label="O_element : 033"  # scripted group (container) (typed FeaturePython)
  n = 1
  ref = O_element
FEATURE [App::DocumentObjectGroupPython] G4_METHANOL  # scripted group (container) (typed FeaturePython)
  Dunit = g/cm3
  Dvalue = 0.7914
  Group = -> [C_element060,H_element054,O_element062]
  conduct = 2
  density = 1
  expand = 3
  formula = G4_METHANOL
  name = G4_METHANOL
  specific = 4
FEATURE [App::DocumentObjectGroupPython] H_element055  label="H_element : 0.134"  # scripted group (container) (typed FeaturePython)
  n = 0.13404
FEATURE [App::DocumentObjectGroupPython] C_element061  label="C_element : 0.778"  # scripted group (container) (typed FeaturePython)
  n = 0.77796
FEATURE [App::DocumentObjectGroupPython] O_element063  label="O_element : 0.035"  # scripted group (container) (typed FeaturePython)
  n = 0.03502
FEATURE [App::DocumentObjectGroupPython] Mg_element009  label="Mg_element : 0.039"  # scripted group (container) (typed FeaturePython)
  n = 0.038594
FEATURE [App::DocumentObjectGroupPython] Ti_element002  label="Ti_element : 0.014"  # scripted group (container) (typed FeaturePython)
  n = 0.014386
FEATURE [App::DocumentObjectGroupPython] G4_MIX_D_WAX  # scripted group (container) (typed FeaturePython)
  Dunit = g/cm3
  Dvalue = 0.99
  Group = -> [H_element055,C_element061,O_element063,Mg_element009,Ti_element002]
  conduct = 2
  density = 1
  expand = 3
  formula = G4_MIX_D_WAX
  name = G4_MIX_D_WAX
  specific = 4
FEATURE [App::DocumentObjectGroupPython] H_element056  label="H_element : 0.135"  # scripted group (container) (typed FeaturePython)
  n = 0.081192
FEATURE [App::DocumentObjectGroupPython] C_element062  label="C_element : 0.583"  # scripted group (container) (typed FeaturePython)
  n = 0.583442
FEATURE [App::DocumentObjectGroupPython] N_element024  label="N_element : 0.018"  # scripted group (container) (typed FeaturePython)
  n = 0.017798
FEATURE [App::DocumentObjectGroupPython] O_element064  label="O_element : 0.186"  # scripted group (container) (typed FeaturePython)
  n = 0.186381
FEATURE [App::DocumentObjectGroupPython] Mg_element010  label="Mg_element : 0.130"  # scripted group (container) (typed FeaturePython)
  n = 0.130287
FEATURE [App::DocumentObjectGroupPython] Cl_element015  label="Cl_element : 0.588"  # scripted group (container) (typed FeaturePython)
  n = 0.0009
FEATURE [App::DocumentObjectGroupPython] G4_MS20_TISSUE  # scripted group (container) (typed FeaturePython)
  Dunit = g/cm3
  Dvalue = 1
  Group = -> [H_element056,C_element062,N_element024,O_element064,Mg_element010,Cl_element015]
  conduct = 2
  density = 1
  expand = 3
  formula = G4_MS20_TISSUE
  name = G4_MS20_TISSUE
  specific = 4
FEATURE [App::DocumentObjectGroupPython] H_element057  label="H_element : 0.136"  # scripted group (container) (typed FeaturePython)
  n = 0.102
FEATURE [App::DocumentObjectGroupPython] C_element063  label="C_element : 0.143"  # scripted group (container) (typed FeaturePython)
  n = 0.143
FEATURE [App::DocumentObjectGroupPython] N_element025  label="N_element : 0.034"  # scripted group (container) (typed FeaturePython)
  n = 0.034
FEATURE [App::DocumentObjectGroupPython] O_element065  label="O_element : 0.710"  # scripted group (container) (typed FeaturePython)
  n = 0.71
FEATURE [App::DocumentObjectGroupPython] Na_element011  label="Na_element : 0.098"  # scripted group (container) (typed FeaturePython)
  n = 0.001
FEATURE [App::DocumentObjectGroupPython] P_element007  label="P_element : 0.002"  # scripted group (container) (typed FeaturePython)
  n = 0.002
FEATURE [App::DocumentObjectGroupPython] S_element017  label="S_element : 0.018"  # scripted group (container) (typed FeaturePython)
  n = 0.003
FEATURE [App::DocumentObjectGroupPython] Cl_element016  label="Cl_element : 0.589"  # scripted group (container) (typed FeaturePython)
  n = 0.001
FEATURE [App::DocumentObjectGroupPython] K_element006  label="K_element : 0.004"  # scripted group (container) (typed FeaturePython)
  n = 0.004
FEATURE [App::DocumentObjectGroupPython] G4_MUSCLE_SKELETAL_ICRP  # scripted group (container) (typed FeaturePython)
  Dunit = g/cm3
  Dvalue = 1.05
  Group = -> [H_element057,C_element063,N_element025,O_element065,Na_element011,P_element007,S_element017,Cl_element016,K_element006]
  conduct = 2
  density = 1
  expand = 3
  formula = G4_MUSCLE_SKELETAL_ICRP
  name = G4_MUSCLE_SKELETAL_ICRP
  specific = 4
FEATURE [App::DocumentObjectGroupPython] H_element058  label="H_element : 0.137"  # scripted group (container) (typed FeaturePython)
  n = 0.102102
FEATURE [App::DocumentObjectGroupPython] C_element064  label="C_element : 0.123"  # scripted group (container) (typed FeaturePython)
  n = 0.123123
FEATURE [App::DocumentObjectGroupPython] N_element026  label="N_element : 0.756"  # scripted group (container) (typed FeaturePython)
  n = 0.035035
FEATURE [App::DocumentObjectGroupPython] O_element066  label="O_element : 0.730"  # scripted group (container) (typed FeaturePython)
  n = 0.72973
FEATURE [App::DocumentObjectGroupPython] Na_element012  label="Na_element : 0.099"  # scripted group (container) (typed FeaturePython)
  n = 0.001001
FEATURE [App::DocumentObjectGroupPython] P_element008  label="P_element : 0.106"  # scripted group (container) (typed FeaturePython)
  n = 0.002002
FEATURE [App::DocumentObjectGroupPython] S_element018  label="S_element : 0.019"  # scripted group (container) (typed FeaturePython)
  n = 0.004004
FEATURE [App::DocumentObjectGroupPython] K_element007  label="K_element : 0.016"  # scripted group (container) (typed FeaturePython)
  n = 0.003003
FEATURE [App::DocumentObjectGroupPython] G4_MUSCLE_STRIATED_ICRU  # scripted group (container) (typed FeaturePython)
  Dunit = g/cm3
  Dvalue = 1.04
  Group = -> [H_element058,C_element064,N_element026,O_element066,Na_element012,P_element008,S_element018,K_element007]
  conduct = 2
  density = 1
  expand = 3
  formula = G4_MUSCLE_STRIATED_ICRU
  name = G4_MUSCLE_STRIATED_ICRU
  specific = 4
FEATURE [App::DocumentObjectGroupPython] H_element059  label="H_element : 0.098"  # scripted group (container) (typed FeaturePython)
  n = 0.0982341
FEATURE [App::DocumentObjectGroupPython] C_element065  label="C_element : 0.156"  # scripted group (container) (typed FeaturePython)
  n = 0.156214
FEATURE [App::DocumentObjectGroupPython] N_element027  label="N_element : 0.757"  # scripted group (container) (typed FeaturePython)
  n = 0.035451
FEATURE [App::DocumentObjectGroupPython] O_element067  label="O_element : 0.880"  # scripted group (container) (typed FeaturePython)
  n = 0.710101
FEATURE [App::DocumentObjectGroupPython] G4_MUSCLE_WITH_SUCROSE  # scripted group (container) (typed FeaturePython)
  Dunit = g/cm3
  Dvalue = 1.11
  Group = -> [H_element059,C_element065,N_element027,O_element067]
  conduct = 2
  density = 1
  expand = 3
  formula = G4_MUSCLE_WITH_SUCROSE
  name = G4_MUSCLE_WITH_SUCROSE
  specific = 4
FEATURE [App::DocumentObjectGroupPython] H_element060  label="H_element : 0.138"  # scripted group (container) (typed FeaturePython)
  n = 0.101969
FEATURE [App::DocumentObjectGroupPython] C_element066  label="C_element : 0.120"  # scripted group (container) (typed FeaturePython)
  n = 0.120058
FEATURE [App::DocumentObjectGroupPython] N_element028  label="N_element : 0.758"  # scripted group (container) (typed FeaturePython)
  n = 0.035451
FEATURE [App::DocumentObjectGroupPython] O_element068  label="O_element : 0.743"  # scripted group (container) (typed FeaturePython)
  n = 0.742522
FEATURE [App::DocumentObjectGroupPython] G4_MUSCLE_WITHOUT_SUCROSE  # scripted group (container) (typed FeaturePython)
  Dunit = g/cm3
  Dvalue = 1.07
  Group = -> [H_element060,C_element066,N_element028,O_element068]
  conduct = 2
  density = 1
  expand = 3
  formula = G4_MUSCLE_WITHOUT_SUCROSE
  name = G4_MUSCLE_WITHOUT_SUCROSE
  specific = 4
FEATURE [App::DocumentObjectGroupPython] C_element067  label="C_element : 10"  # scripted group (container) (typed FeaturePython)
  n = 10
  ref = C_element
FEATURE [App::DocumentObjectGroupPython] H_element061  label="H_element : 030"  # scripted group (container) (typed FeaturePython)
  n = 8
  ref = H_element
FEATURE [App::DocumentObjectGroupPython] G4_NAPHTHALENE  # scripted group (container) (typed FeaturePython)
  Dunit = g/cm3
  Dvalue = 1.145
  Group = -> [C_element067,H_element061]
  conduct = 2
  density = 1
  expand = 3
  formula = G4_NAPHTHALENE
  name = G4_NAPHTHALENE
  specific = 4
FEATURE [App::DocumentObjectGroupPython] C_element068  label="C_element : 034"  # scripted group (container) (typed FeaturePython)
  n = 6
  ref = C_element
FEATURE [App::DocumentObjectGroupPython] H_element062  label="H_element : 031"  # scripted group (container) (typed FeaturePython)
  n = 5
  ref = H_element
FEATURE [App::DocumentObjectGroupPython] N_element029  label="N_element : 012"  # scripted group (container) (typed FeaturePython)
  n = 1
  ref = N_element
FEATURE [App::DocumentObjectGroupPython] O_element069  label="O_element : 034"  # scripted group (container) (typed FeaturePython)
  n = 2
  ref = O_element
FEATURE [App::DocumentObjectGroupPython] G4_NITROBENZENE  # scripted group (container) (typed FeaturePython)
  Dunit = g/cm3
  Dvalue = 1.19867
  Group = -> [C_element068,H_element062,N_element029,O_element069]
  conduct = 2
  density = 1
  expand = 3
  formula = G4_NITROBENZENE
  name = G4_NITROBENZENE
  specific = 4
FEATURE [App::DocumentObjectGroupPython] N_element030  label="N_element : 013"  # scripted group (container) (typed FeaturePython)
  n = 2
  ref = N_element
FEATURE [App::DocumentObjectGroupPython] O_element070  label="O_element : 035"  # scripted group (container) (typed FeaturePython)
  n = 1
  ref = O_element
FEATURE [App::DocumentObjectGroupPython] G4_NITROUS_OXIDE  # scripted group (container) (typed FeaturePython)
  Dunit = g/cm3
  Dvalue = 0.00183094
  Group = -> [N_element030,O_element070]
  conduct = 2
  density = 1
  expand = 3
  formula = G4_NITROUS_OXIDE
  name = G4_NITROUS_OXIDE
  specific = 4
FEATURE [App::DocumentObjectGroupPython] H_element063  label="H_element : 0.104"  # scripted group (container) (typed FeaturePython)
  n = 0.103509
FEATURE [App::DocumentObjectGroupPython] C_element069  label="C_element : 0.648"  # scripted group (container) (typed FeaturePython)
  n = 0.648416
FEATURE [App::DocumentObjectGroupPython] N_element031  label="N_element : 0.100"  # scripted group (container) (typed FeaturePython)
  n = 0.0995361
FEATURE [App::DocumentObjectGroupPython] O_element071  label="O_element : 0.149"  # scripted group (container) (typed FeaturePython)
  n = 0.148539
FEATURE [App::DocumentObjectGroupPython] G4_NYLON_8062  label="G4_NYLON-8062"  # scripted group (container) (typed FeaturePython)
  Dunit = g/cm3
  Dvalue = 1.08
  Group = -> [H_element063,C_element069,N_element031,O_element071]
  conduct = 2
  density = 1
  expand = 3
  formula = G4_NYLON-8062
  name = G4_NYLON-8062
  specific = 4
FEATURE [App::DocumentObjectGroupPython] C_element070  label="C_element : 035"  # scripted group (container) (typed FeaturePython)
  n = 6
  ref = C_element
FEATURE [App::DocumentObjectGroupPython] H_element064  label="H_element : 11"  # scripted group (container) (typed FeaturePython)
  n = 11
  ref = H_element
FEATURE [App::DocumentObjectGroupPython] N_element032  label="N_element : 014"  # scripted group (container) (typed FeaturePython)
  n = 1
  ref = N_element
FEATURE [App::DocumentObjectGroupPython] O_element072  label="O_element : 036"  # scripted group (container) (typed FeaturePython)
  n = 1
  ref = O_element
FEATURE [App::DocumentObjectGroupPython] G4_NYLON_6_6  label="G4_NYLON-6-6"  # scripted group (container) (typed FeaturePython)
  Dunit = g/cm3
  Dvalue = 1.14
  Group = -> [C_element070,H_element064,N_element032,O_element072]
  conduct = 2
  density = 1
  expand = 3
  formula = G4_NYLON-6-6
  name = G4_NYLON-6-6
  specific = 4
FEATURE [App::DocumentObjectGroupPython] H_element065  label="H_element : 0.139"  # scripted group (container) (typed FeaturePython)
  n = 0.107062
FEATURE [App::DocumentObjectGroupPython] C_element071  label="C_element : 0.680"  # scripted group (container) (typed FeaturePython)
  n = 0.680449
FEATURE [App::DocumentObjectGroupPython] N_element033  label="N_element : 0.099"  # scripted group (container) (typed FeaturePython)
  n = 0.099189
FEATURE [App::DocumentObjectGroupPython] O_element073  label="O_element : 0.113"  # scripted group (container) (typed FeaturePython)
  n = 0.1133
FEATURE [App::DocumentObjectGroupPython] G4_NYLON_6_10  label="G4_NYLON-6-10"  # scripted group (container) (typed FeaturePython)
  Dunit = g/cm3
  Dvalue = 1.14
  Group = -> [H_element065,C_element071,N_element033,O_element073]
  conduct = 2
  density = 1
  expand = 3
  formula = G4_NYLON-6-10
  name = G4_NYLON-6-10
  specific = 4
FEATURE [App::DocumentObjectGroupPython] H_element066  label="H_element : 0.140"  # scripted group (container) (typed FeaturePython)
  n = 0.115476
FEATURE [App::DocumentObjectGroupPython] C_element072  label="C_element : 0.721"  # scripted group (container) (typed FeaturePython)
  n = 0.720818
FEATURE [App::DocumentObjectGroupPython] N_element034  label="N_element : 0.076"  # scripted group (container) (typed FeaturePython)
  n = 0.0764169
FEATURE [App::DocumentObjectGroupPython] O_element074  label="O_element : 0.087"  # scripted group (container) (typed FeaturePython)
  n = 0.0872889
FEATURE [App::DocumentObjectGroupPython] G4_NYLON_11_RILSAN  label="G4_NYLON-11_RILSAN"  # scripted group (container) (typed FeaturePython)
  Dunit = g/cm3
  Dvalue = 1.425
  Group = -> [H_element066,C_element072,N_element034,O_element074]
  conduct = 2
  density = 1
  expand = 3
  formula = G4_NYLON-11_RILSAN
  name = G4_NYLON-11_RILSAN
  specific = 4
FEATURE [App::DocumentObjectGroupPython] C_element073  label="C_element : 8"  # scripted group (container) (typed FeaturePython)
  n = 8
  ref = C_element
FEATURE [App::DocumentObjectGroupPython] H_element067  label="H_element : 18"  # scripted group (container) (typed FeaturePython)
  n = 18
  ref = H_element
FEATURE [App::DocumentObjectGroupPython] G4_OCTANE  # scripted group (container) (typed FeaturePython)
  Dunit = g/cm3
  Dvalue = 0.7026
  Group = -> [C_element073,H_element067]
  conduct = 2
  density = 1
  expand = 3
  formula = G4_OCTANE
  name = G4_OCTANE
  specific = 4
FEATURE [App::DocumentObjectGroupPython] C_element074  label="C_element : 25"  # scripted group (container) (typed FeaturePython)
  n = 25
  ref = C_element
FEATURE [App::DocumentObjectGroupPython] H_element068  label="H_element : 52"  # scripted group (container) (typed FeaturePython)
  n = 52
  ref = H_element
FEATURE [App::DocumentObjectGroupPython] G4_PARAFFIN  # scripted group (container) (typed FeaturePython)
  Dunit = g/cm3
  Dvalue = 0.93
  Group = -> [C_element074,H_element068]
  conduct = 2
  density = 1
  expand = 3
  formula = G4_PARAFFIN
  name = G4_PARAFFIN
  specific = 4
FEATURE [App::DocumentObjectGroupPython] C_element075  label="C_element : 036"  # scripted group (container) (typed FeaturePython)
  n = 5
  ref = C_element
FEATURE [App::DocumentObjectGroupPython] H_element069  label="H_element : 032"  # scripted group (container) (typed FeaturePython)
  n = 12
  ref = H_element
FEATURE [App::DocumentObjectGroupPython] G4_N_PENTANE  label="G4_N-PENTANE"  # scripted group (container) (typed FeaturePython)
  Dunit = g/cm3
  Dvalue = 0.6262
  Group = -> [C_element075,H_element069]
  conduct = 2
  density = 1
  expand = 3
  formula = G4_N-PENTANE
  name = G4_N-PENTANE
  specific = 4
FEATURE [App::DocumentObjectGroupPython] H_element070  label="H_element : 0.014"  # scripted group (container) (typed FeaturePython)
  n = 0.0141
FEATURE [App::DocumentObjectGroupPython] C_element076  label="C_element : 0.072"  # scripted group (container) (typed FeaturePython)
  n = 0.072261
FEATURE [App::DocumentObjectGroupPython] N_element035  label="N_element : 0.019"  # scripted group (container) (typed FeaturePython)
  n = 0.01932
FEATURE [App::DocumentObjectGroupPython] O_element075  label="O_element : 0.066"  # scripted group (container) (typed FeaturePython)
  n = 0.066101
FEATURE [App::DocumentObjectGroupPython] S_element019  label="S_element : 0.020"  # scripted group (container) (typed FeaturePython)
  n = 0.00189
FEATURE [App::DocumentObjectGroupPython] Br_element004  label="Br_element : 0.349"  # scripted group (container) (typed FeaturePython)
  n = 0.349103
FEATURE [App::DocumentObjectGroupPython] Ag_element001  label="Ag_element : 0.474"  # scripted group (container) (typed FeaturePython)
  n = 0.474105
FEATURE [App::DocumentObjectGroupPython] I_element005  label="I_element : 0.003"  # scripted group (container) (typed FeaturePython)
  n = 0.00312
FEATURE [App::DocumentObjectGroupPython] G4_PHOTO_EMULSION  # scripted group (container) (typed FeaturePython)
  Dunit = g/cm3
  Dvalue = 3.815
  Group = -> [H_element070,C_element076,N_element035,O_element075,S_element019,Br_element004,Ag_element001,I_element005]
  conduct = 2
  density = 1
  expand = 3
  formula = G4_PHOTO_EMULSION
  name = G4_PHOTO_EMULSION
  specific = 4
FEATURE [App::DocumentObjectGroupPython] C_element077  label="C_element : 9"  # scripted group (container) (typed FeaturePython)
  n = 9
  ref = C_element
FEATURE [App::DocumentObjectGroupPython] H_element071  label="H_element : 033"  # scripted group (container) (typed FeaturePython)
  n = 10
  ref = H_element
FEATURE [App::DocumentObjectGroupPython] G4_PLASTIC_SC_VINYLTOLUENE  # scripted group (container) (typed FeaturePython)
  Dunit = g/cm3
  Dvalue = 1.032
  Group = -> [C_element077,H_element071]
  conduct = 2
  density = 1
  expand = 3
  formula = G4_PLASTIC_SC_VINYLTOLUENE
  name = G4_PLASTIC_SC_VINYLTOLUENE
  specific = 4
FEATURE [App::DocumentObjectGroupPython] Pu_element001  label="Pu_element : 1"  # scripted group (container) (typed FeaturePython)
  n = 1
  ref = Pu_element
FEATURE [App::DocumentObjectGroupPython] O_element076  label="O_element : 037"  # scripted group (container) (typed FeaturePython)
  n = 2
  ref = O_element
FEATURE [App::DocumentObjectGroupPython] G4_PLUTONIUM_DIOXIDE  # scripted group (container) (typed FeaturePython)
  Dunit = g/cm3
  Dvalue = 11.46
  Group = -> [Pu_element001,O_element076]
  conduct = 2
  density = 1
  expand = 3
  formula = G4_PLUTONIUM_DIOXIDE
  name = G4_PLUTONIUM_DIOXIDE
  specific = 4
FEATURE [App::DocumentObjectGroupPython] C_element078  label="C_element : 037"  # scripted group (container) (typed FeaturePython)
  n = 3
  ref = C_element
FEATURE [App::DocumentObjectGroupPython] H_element072  label="H_element : 034"  # scripted group (container) (typed FeaturePython)
  n = 3
  ref = H_element
FEATURE [App::DocumentObjectGroupPython] N_element036  label="N_element : 015"  # scripted group (container) (typed FeaturePython)
  n = 1
  ref = N_element
FEATURE [App::DocumentObjectGroupPython] G4_POLYACRYLONITRILE  # scripted group (container) (typed FeaturePython)
  Dunit = g/cm3
  Dvalue = 1.17
  Group = -> [C_element078,H_element072,N_element036]
  conduct = 2
  density = 1
  expand = 3
  formula = G4_POLYACRYLONITRILE
  name = G4_POLYACRYLONITRILE
  specific = 4
FEATURE [App::DocumentObjectGroupPython] C_element079  label="C_element : 16"  # scripted group (container) (typed FeaturePython)
  n = 16
  ref = C_element
FEATURE [App::DocumentObjectGroupPython] H_element073  label="H_element : 035"  # scripted group (container) (typed FeaturePython)
  n = 14
  ref = H_element
FEATURE [App::DocumentObjectGroupPython] O_element077  label="O_element : 038"  # scripted group (container) (typed FeaturePython)
  n = 3
  ref = O_element
FEATURE [App::DocumentObjectGroupPython] G4_POLYCARBONATE  # scripted group (container) (typed FeaturePython)
  Dunit = g/cm3
  Dvalue = 1.2
  Group = -> [C_element079,H_element073,O_element077]
  conduct = 2
  density = 1
  expand = 3
  formula = G4_POLYCARBONATE
  name = G4_POLYCARBONATE
  specific = 4
FEATURE [App::DocumentObjectGroupPython] C_element080  label="C_element : 038"  # scripted group (container) (typed FeaturePython)
  n = 8
  ref = C_element
FEATURE [App::DocumentObjectGroupPython] H_element074  label="H_element : 036"  # scripted group (container) (typed FeaturePython)
  n = 7
  ref = H_element
FEATURE [App::DocumentObjectGroupPython] Cl_element017  label="Cl_element : 007"  # scripted group (container) (typed FeaturePython)
  n = 1
  ref = Cl_element
FEATURE [App::DocumentObjectGroupPython] G4_POLYCHLOROSTYRENE  # scripted group (container) (typed FeaturePython)
  Dunit = g/cm3
  Dvalue = 1.3
  Group = -> [C_element080,H_element074,Cl_element017]
  conduct = 2
  density = 1
  expand = 3
  formula = G4_POLYCHLOROSTYRENE
  name = G4_POLYCHLOROSTYRENE
  specific = 4
FEATURE [App::DocumentObjectGroupPython] C_element081  label="C_element : 039"  # scripted group (container) (typed FeaturePython)
  n = 1
  ref = C_element
FEATURE [App::DocumentObjectGroupPython] H_element075  label="H_element : 037"  # scripted group (container) (typed FeaturePython)
  n = 2
  ref = H_element
FEATURE [App::DocumentObjectGroupPython] G4_POLYETHYLENE  # scripted group (container) (typed FeaturePython)
  Dunit = g/cm3
  Dvalue = 0.94
  Group = -> [C_element081,H_element075]
  conduct = 2
  density = 1
  expand = 3
  formula = G4_POLYETHYLENE
  name = G4_POLYETHYLENE
  specific = 4
FEATURE [App::DocumentObjectGroupPython] C_element082  label="C_element : 040"  # scripted group (container) (typed FeaturePython)
  n = 10
  ref = C_element
FEATURE [App::DocumentObjectGroupPython] H_element076  label="H_element : 038"  # scripted group (container) (typed FeaturePython)
  n = 8
  ref = H_element
FEATURE [App::DocumentObjectGroupPython] O_element078  label="O_element : 039"  # scripted group (container) (typed FeaturePython)
  n = 4
  ref = O_element
FEATURE [App::DocumentObjectGroupPython] G4_MYLAR  # scripted group (container) (typed FeaturePython)
  Dunit = g/cm3
  Dvalue = 1.4
  Group = -> [C_element082,H_element076,O_element078]
  conduct = 2
  density = 1
  expand = 3
  formula = G4_MYLAR
  name = G4_MYLAR
  specific = 4
FEATURE [App::DocumentObjectGroupPython] C_element083  label="C_element : 041"  # scripted group (container) (typed FeaturePython)
  n = 5
  ref = C_element
FEATURE [App::DocumentObjectGroupPython] H_element077  label="H_element : 039"  # scripted group (container) (typed FeaturePython)
  n = 8
  ref = H_element
FEATURE [App::DocumentObjectGroupPython] O_element079  label="O_element : 040"  # scripted group (container) (typed FeaturePython)
  n = 2
  ref = O_element
FEATURE [App::DocumentObjectGroupPython] G4_PLEXIGLASS  # scripted group (container) (typed FeaturePython)
  Dunit = g/cm3
  Dvalue = 1.19
  Group = -> [C_element083,H_element077,O_element079]
  conduct = 2
  density = 1
  expand = 3
  formula = G4_PLEXIGLASS
  name = G4_PLEXIGLASS
  specific = 4
FEATURE [App::DocumentObjectGroupPython] C_element084  label="C_element : 042"  # scripted group (container) (typed FeaturePython)
  n = 1
  ref = C_element
FEATURE [App::DocumentObjectGroupPython] H_element078  label="H_element : 040"  # scripted group (container) (typed FeaturePython)
  n = 2
  ref = H_element
FEATURE [App::DocumentObjectGroupPython] O_element080  label="O_element : 041"  # scripted group (container) (typed FeaturePython)
  n = 1
  ref = O_element
FEATURE [App::DocumentObjectGroupPython] G4_POLYOXYMETHYLENE  # scripted group (container) (typed FeaturePython)
  Dunit = g/cm3
  Dvalue = 1.425
  Group = -> [C_element084,H_element078,O_element080]
  conduct = 2
  density = 1
  expand = 3
  formula = G4_POLYOXYMETHYLENE
  name = G4_POLYOXYMETHYLENE
  specific = 4
FEATURE [App::DocumentObjectGroupPython] C_element085  label="C_element : 043"  # scripted group (container) (typed FeaturePython)
  n = 2
  ref = C_element
FEATURE [App::DocumentObjectGroupPython] H_element079  label="H_element : 041"  # scripted group (container) (typed FeaturePython)
  n = 4
  ref = H_element
FEATURE [App::DocumentObjectGroupPython] G4_POLYPROPYLENE  # scripted group (container) (typed FeaturePython)
  Dunit = g/cm3
  Dvalue = 0.9
  Group = -> [C_element085,H_element079]
  conduct = 2
  density = 1
  expand = 3
  formula = G4_POLYPROPYLENE
  name = G4_POLYPROPYLENE
  specific = 4
FEATURE [App::DocumentObjectGroupPython] C_element086  label="C_element : 044"  # scripted group (container) (typed FeaturePython)
  n = 8
  ref = C_element
FEATURE [App::DocumentObjectGroupPython] H_element080  label="H_element : 042"  # scripted group (container) (typed FeaturePython)
  n = 8
  ref = H_element
FEATURE [App::DocumentObjectGroupPython] G4_POLYSTYRENE  # scripted group (container) (typed FeaturePython)
  Dunit = g/cm3
  Dvalue = 1.06
  Group = -> [C_element086,H_element080]
  conduct = 2
  density = 1
  expand = 3
  formula = G4_POLYSTYRENE
  name = G4_POLYSTYRENE
  specific = 4
FEATURE [App::DocumentObjectGroupPython] C_element087  label="C_element : 045"  # scripted group (container) (typed FeaturePython)
  n = 2
  ref = C_element
FEATURE [App::DocumentObjectGroupPython] F_element014  label="F_element : 4"  # scripted group (container) (typed FeaturePython)
  n = 4
  ref = F_element
FEATURE [App::DocumentObjectGroupPython] G4_TEFLON  # scripted group (container) (typed FeaturePython)
  Dunit = g/cm3
  Dvalue = 2.2
  Group = -> [C_element087,F_element014]
  conduct = 2
  density = 1
  expand = 3
  formula = G4_TEFLON
  name = G4_TEFLON
  specific = 4
FEATURE [App::DocumentObjectGroupPython] C_element088  label="C_element : 046"  # scripted group (container) (typed FeaturePython)
  n = 2
  ref = C_element
FEATURE [App::DocumentObjectGroupPython] F_element015  label="F_element : 006"  # scripted group (container) (typed FeaturePython)
  n = 3
  ref = F_element
FEATURE [App::DocumentObjectGroupPython] Cl_element018  label="Cl_element : 008"  # scripted group (container) (typed FeaturePython)
  n = 1
  ref = Cl_element
FEATURE [App::DocumentObjectGroupPython] G4_POLYTRIFLUOROCHLOROETHYLENE  # scripted group (container) (typed FeaturePython)
  Dunit = g/cm3
  Dvalue = 2.1
  Group = -> [C_element088,F_element015,Cl_element018]
  conduct = 2
  density = 1
  expand = 3
  formula = G4_POLYTRIFLUOROCHLOROETHYLENE
  name = G4_POLYTRIFLUOROCHLOROETHYLENE
  specific = 4
FEATURE [App::DocumentObjectGroupPython] C_element089  label="C_element : 047"  # scripted group (container) (typed FeaturePython)
  n = 4
  ref = C_element
FEATURE [App::DocumentObjectGroupPython] H_element081  label="H_element : 043"  # scripted group (container) (typed FeaturePython)
  n = 6
  ref = H_element
FEATURE [App::DocumentObjectGroupPython] O_element081  label="O_element : 042"  # scripted group (container) (typed FeaturePython)
  n = 2
  ref = O_element
FEATURE [App::DocumentObjectGroupPython] G4_POLYVINYL_ACETATE  # scripted group (container) (typed FeaturePython)
  Dunit = g/cm3
  Dvalue = 1.19
  Group = -> [C_element089,H_element081,O_element081]
  conduct = 2
  density = 1
  expand = 3
  formula = G4_POLYVINYL_ACETATE
  name = G4_POLYVINYL_ACETATE
  specific = 4
FEATURE [App::DocumentObjectGroupPython] C_element090  label="C_element : 048"  # scripted group (container) (typed FeaturePython)
  n = 2
  ref = C_element
FEATURE [App::DocumentObjectGroupPython] H_element082  label="H_element : 044"  # scripted group (container) (typed FeaturePython)
  n = 4
  ref = H_element
FEATURE [App::DocumentObjectGroupPython] O_element082  label="O_element : 043"  # scripted group (container) (typed FeaturePython)
  n = 1
  ref = O_element
FEATURE [App::DocumentObjectGroupPython] G4_POLYVINYL_ALCOHOL  # scripted group (container) (typed FeaturePython)
  Dunit = g/cm3
  Dvalue = 1.3
  Group = -> [C_element090,H_element082,O_element082]
  conduct = 2
  density = 1
  expand = 3
  formula = G4_POLYVINYL_ALCOHOL
  name = G4_POLYVINYL_ALCOHOL
  specific = 4
FEATURE [App::DocumentObjectGroupPython] C_element091  label="C_element : 049"  # scripted group (container) (typed FeaturePython)
  n = 8
  ref = C_element
FEATURE [App::DocumentObjectGroupPython] H_element083  label="H_element : 045"  # scripted group (container) (typed FeaturePython)
  n = 14
  ref = H_element
FEATURE [App::DocumentObjectGroupPython] O_element083  label="O_element : 044"  # scripted group (container) (typed FeaturePython)
  n = 2
  ref = O_element
FEATURE [App::DocumentObjectGroupPython] G4_POLYVINYL_BUTYRAL  # scripted group (container) (typed FeaturePython)
  Dunit = g/cm3
  Dvalue = 1.12
  Group = -> [C_element091,H_element083,O_element083]
  conduct = 2
  density = 1
  expand = 3
  formula = G4_POLYVINYL_BUTYRAL
  name = G4_POLYVINYL_BUTYRAL
  specific = 4
FEATURE [App::DocumentObjectGroupPython] C_element092  label="C_element : 050"  # scripted group (container) (typed FeaturePython)
  n = 2
  ref = C_element
FEATURE [App::DocumentObjectGroupPython] H_element084  label="H_element : 046"  # scripted group (container) (typed FeaturePython)
  n = 3
  ref = H_element
FEATURE [App::DocumentObjectGroupPython] Cl_element019  label="Cl_element : 009"  # scripted group (container) (typed FeaturePython)
  n = 1
  ref = Cl_element
FEATURE [App::DocumentObjectGroupPython] G4_POLYVINYL_CHLORIDE  # scripted group (container) (typed FeaturePython)
  Dunit = g/cm3
  Dvalue = 1.3
  Group = -> [C_element092,H_element084,Cl_element019]
  conduct = 2
  density = 1
  expand = 3
  formula = G4_POLYVINYL_CHLORIDE
  name = G4_POLYVINYL_CHLORIDE
  specific = 4
FEATURE [App::DocumentObjectGroupPython] C_element093  label="C_element : 051"  # scripted group (container) (typed FeaturePython)
  n = 2
  ref = C_element
FEATURE [App::DocumentObjectGroupPython] H_element085  label="H_element : 047"  # scripted group (container) (typed FeaturePython)
  n = 2
  ref = H_element
FEATURE [App::DocumentObjectGroupPython] Cl_element020  label="Cl_element : 010"  # scripted group (container) (typed FeaturePython)
  n = 2
  ref = Cl_element
FEATURE [App::DocumentObjectGroupPython] G4_POLYVINYLIDENE_CHLORIDE  # scripted group (container) (typed FeaturePython)
  Dunit = g/cm3
  Dvalue = 1.7
  Group = -> [C_element093,H_element085,Cl_element020]
  conduct = 2
  density = 1
  expand = 3
  formula = G4_POLYVINYLIDENE_CHLORIDE
  name = G4_POLYVINYLIDENE_CHLORIDE
  specific = 4
FEATURE [App::DocumentObjectGroupPython] C_element094  label="C_element : 052"  # scripted group (container) (typed FeaturePython)
  n = 2
  ref = C_element
FEATURE [App::DocumentObjectGroupPython] H_element086  label="H_element : 048"  # scripted group (container) (typed FeaturePython)
  n = 2
  ref = H_element
FEATURE [App::DocumentObjectGroupPython] F_element016  label="F_element : 007"  # scripted group (container) (typed FeaturePython)
  n = 2
  ref = F_element
FEATURE [App::DocumentObjectGroupPython] G4_POLYVINYLIDENE_FLUORIDE  # scripted group (container) (typed FeaturePython)
  Dunit = g/cm3
  Dvalue = 1.76
  Group = -> [C_element094,H_element086,F_element016]
  conduct = 2
  density = 1
  expand = 3
  formula = G4_POLYVINYLIDENE_FLUORIDE
  name = G4_POLYVINYLIDENE_FLUORIDE
  specific = 4
FEATURE [App::DocumentObjectGroupPython] C_element095  label="C_element : 053"  # scripted group (container) (typed FeaturePython)
  n = 6
  ref = C_element
FEATURE [App::DocumentObjectGroupPython] H_element087  label="H_element : 9"  # scripted group (container) (typed FeaturePython)
  n = 9
  ref = H_element
FEATURE [App::DocumentObjectGroupPython] N_element037  label="N_element : 016"  # scripted group (container) (typed FeaturePython)
  n = 1
  ref = N_element
FEATURE [App::DocumentObjectGroupPython] O_element084  label="O_element : 045"  # scripted group (container) (typed FeaturePython)
  n = 1
  ref = O_element
FEATURE [App::DocumentObjectGroupPython] G4_POLYVINYL_PYRROLIDONE  # scripted group (container) (typed FeaturePython)
  Dunit = g/cm3
  Dvalue = 1.25
  Group = -> [C_element095,H_element087,N_element037,O_element084]
  conduct = 2
  density = 1
  expand = 3
  formula = G4_POLYVINYL_PYRROLIDONE
  name = G4_POLYVINYL_PYRROLIDONE
  specific = 4
FEATURE [App::DocumentObjectGroupPython] K_element008  label="K_element : 1"  # scripted group (container) (typed FeaturePython)
  n = 1
  ref = K_element
FEATURE [App::DocumentObjectGroupPython] I_element006  label="I_element : 003"  # scripted group (container) (typed FeaturePython)
  n = 1
  ref = I_element
FEATURE [App::DocumentObjectGroupPython] G4_POTASSIUM_IODIDE  # scripted group (container) (typed FeaturePython)
  Dunit = g/cm3
  Dvalue = 3.13
  Group = -> [K_element008,I_element006]
  conduct = 2
  density = 1
  expand = 3
  formula = G4_POTASSIUM_IODIDE
  name = G4_POTASSIUM_IODIDE
  specific = 4
FEATURE [App::DocumentObjectGroupPython] K_element009  label="K_element : 2"  # scripted group (container) (typed FeaturePython)
  n = 2
  ref = K_element
FEATURE [App::DocumentObjectGroupPython] O_element085  label="O_element : 046"  # scripted group (container) (typed FeaturePython)
  n = 1
  ref = O_element
FEATURE [App::DocumentObjectGroupPython] G4_POTASSIUM_OXIDE  # scripted group (container) (typed FeaturePython)
  Dunit = g/cm3
  Dvalue = 2.32
  Group = -> [K_element009,O_element085]
  conduct = 2
  density = 1
  expand = 3
  formula = G4_POTASSIUM_OXIDE
  name = G4_POTASSIUM_OXIDE
  specific = 4
FEATURE [App::DocumentObjectGroupPython] C_element096  label="C_element : 054"  # scripted group (container) (typed FeaturePython)
  n = 3
  ref = C_element
FEATURE [App::DocumentObjectGroupPython] H_element088  label="H_element : 049"  # scripted group (container) (typed FeaturePython)
  n = 8
  ref = H_element
FEATURE [App::DocumentObjectGroupPython] G4_PROPANE  # scripted group (container) (typed FeaturePython)
  Dunit = g/cm3
  Dvalue = 0.00187939
  Group = -> [C_element096,H_element088]
  conduct = 2
  density = 1
  expand = 3
  formula = G4_PROPANE
  name = G4_PROPANE
  specific = 4
FEATURE [App::DocumentObjectGroupPython] C_element097  label="C_element : 055"  # scripted group (container) (typed FeaturePython)
  n = 3
  ref = C_element
FEATURE [App::DocumentObjectGroupPython] H_element089  label="H_element : 050"  # scripted group (container) (typed FeaturePython)
  n = 8
  ref = H_element
FEATURE [App::DocumentObjectGroupPython] G4_lPROPANE  # scripted group (container) (typed FeaturePython)
  Dunit = g/cm3
  Dvalue = 0.43
  Group = -> [C_element097,H_element089]
  conduct = 2
  density = 1
  expand = 3
  formula = G4_lPROPANE
  name = G4_lPROPANE
  specific = 4
FEATURE [App::DocumentObjectGroupPython] C_element098  label="C_element : 056"  # scripted group (container) (typed FeaturePython)
  n = 3
  ref = C_element
FEATURE [App::DocumentObjectGroupPython] H_element090  label="H_element : 051"  # scripted group (container) (typed FeaturePython)
  n = 8
  ref = H_element
FEATURE [App::DocumentObjectGroupPython] O_element086  label="O_element : 047"  # scripted group (container) (typed FeaturePython)
  n = 1
  ref = O_element
FEATURE [App::DocumentObjectGroupPython] G4_N_PROPYL_ALCOHOL  label="G4_N-PROPYL_ALCOHOL"  # scripted group (container) (typed FeaturePython)
  Dunit = g/cm3
  Dvalue = 0.8035
  Group = -> [C_element098,H_element090,O_element086]
  conduct = 2
  density = 1
  expand = 3
  formula = G4_N-PROPYL_ALCOHOL
  name = G4_N-PROPYL_ALCOHOL
  specific = 4
FEATURE [App::DocumentObjectGroupPython] C_element099  label="C_element : 057"  # scripted group (container) (typed FeaturePython)
  n = 5
  ref = C_element
FEATURE [App::DocumentObjectGroupPython] H_element091  label="H_element : 052"  # scripted group (container) (typed FeaturePython)
  n = 5
  ref = H_element
FEATURE [App::DocumentObjectGroupPython] N_element038  label="N_element : 017"  # scripted group (container) (typed FeaturePython)
  n = 1
  ref = N_element
FEATURE [App::DocumentObjectGroupPython] G4_PYRIDINE  # scripted group (container) (typed FeaturePython)
  Dunit = g/cm3
  Dvalue = 0.9819
  Group = -> [C_element099,H_element091,N_element038]
  conduct = 2
  density = 1
  expand = 3
  formula = G4_PYRIDINE
  name = G4_PYRIDINE
  specific = 4
FEATURE [App::DocumentObjectGroupPython] H_element092  label="H_element : 0.144"  # scripted group (container) (typed FeaturePython)
  n = 0.143711
FEATURE [App::DocumentObjectGroupPython] C_element100  label="C_element : 0.856"  # scripted group (container) (typed FeaturePython)
  n = 0.856289
FEATURE [App::DocumentObjectGroupPython] G4_RUBBER_BUTYL  # scripted group (container) (typed FeaturePython)
  Dunit = g/cm3
  Dvalue = 0.92
  Group = -> [H_element092,C_element100]
  conduct = 2
  density = 1
  expand = 3
  formula = G4_RUBBER_BUTYL
  name = G4_RUBBER_BUTYL
  specific = 4
FEATURE [App::DocumentObjectGroupPython] H_element093  label="H_element : 0.118"  # scripted group (container) (typed FeaturePython)
  n = 0.118371
FEATURE [App::DocumentObjectGroupPython] C_element101  label="C_element : 0.882"  # scripted group (container) (typed FeaturePython)
  n = 0.881629
FEATURE [App::DocumentObjectGroupPython] G4_RUBBER_NATURAL  # scripted group (container) (typed FeaturePython)
  Dunit = g/cm3
  Dvalue = 0.92
  Group = -> [H_element093,C_element101]
  conduct = 2
  density = 1
  expand = 3
  formula = G4_RUBBER_NATURAL
  name = G4_RUBBER_NATURAL
  specific = 4
FEATURE [App::DocumentObjectGroupPython] H_element094  label="H_element : 0.145"  # scripted group (container) (typed FeaturePython)
  n = 0.05692
FEATURE [App::DocumentObjectGroupPython] C_element102  label="C_element : 0.543"  # scripted group (container) (typed FeaturePython)
  n = 0.542646
FEATURE [App::DocumentObjectGroupPython] Cl_element021  label="Cl_element : 0.400"  # scripted group (container) (typed FeaturePython)
  n = 0.400434
FEATURE [App::DocumentObjectGroupPython] G4_RUBBER_NEOPRENE  # scripted group (container) (typed FeaturePython)
  Dunit = g/cm3
  Dvalue = 1.23
  Group = -> [H_element094,C_element102,Cl_element021]
  conduct = 2
  density = 1
  expand = 3
  formula = G4_RUBBER_NEOPRENE
  name = G4_RUBBER_NEOPRENE
  specific = 4
FEATURE [App::DocumentObjectGroupPython] Si_element006  label="Si_element : 1"  # scripted group (container) (typed FeaturePython)
  n = 1
  ref = Si_element
FEATURE [App::DocumentObjectGroupPython] O_element087  label="O_element : 048"  # scripted group (container) (typed FeaturePython)
  n = 2
  ref = O_element
FEATURE [App::DocumentObjectGroupPython] G4_SILICON_DIOXIDE  # scripted group (container) (typed FeaturePython)
  Dunit = g/cm3
  Dvalue = 2.32
  Group = -> [Si_element006,O_element087]
  conduct = 2
  density = 1
  expand = 3
  formula = G4_SILICON_DIOXIDE
  name = G4_SILICON_DIOXIDE
  specific = 4
FEATURE [App::DocumentObjectGroupPython] Ag_element002  label="Ag_element : 1"  # scripted group (container) (typed FeaturePython)
  n = 1
  ref = Ag_element
FEATURE [App::DocumentObjectGroupPython] Br_element005  label="Br_element : 003"  # scripted group (container) (typed FeaturePython)
  n = 1
  ref = Br_element
FEATURE [App::DocumentObjectGroupPython] G4_SILVER_BROMIDE  # scripted group (container) (typed FeaturePython)
  Dunit = g/cm3
  Dvalue = 6.473
  Group = -> [Ag_element002,Br_element005]
  conduct = 2
  density = 1
  expand = 3
  formula = G4_SILVER_BROMIDE
  name = G4_SILVER_BROMIDE
  specific = 4
FEATURE [App::DocumentObjectGroupPython] Ag_element003  label="Ag_element : 002"  # scripted group (container) (typed FeaturePython)
  n = 1
  ref = Ag_element
FEATURE [App::DocumentObjectGroupPython] Cl_element022  label="Cl_element : 011"  # scripted group (container) (typed FeaturePython)
  n = 1
  ref = Cl_element
FEATURE [App::DocumentObjectGroupPython] G4_SILVER_CHLORIDE  # scripted group (container) (typed FeaturePython)
  Dunit = g/cm3
  Dvalue = 5.56
  Group = -> [Ag_element003,Cl_element022]
  conduct = 2
  density = 1
  expand = 3
  formula = G4_SILVER_CHLORIDE
  name = G4_SILVER_CHLORIDE
  specific = 4
FEATURE [App::DocumentObjectGroupPython] Br_element006  label="Br_element : 0.423"  # scripted group (container) (typed FeaturePython)
  n = 0.422895
FEATURE [App::DocumentObjectGroupPython] Ag_element004  label="Ag_element : 0.574"  # scripted group (container) (typed FeaturePython)
  n = 0.573748
FEATURE [App::DocumentObjectGroupPython] I_element007  label="I_element : 0.649"  # scripted group (container) (typed FeaturePython)
  n = 0.003357
FEATURE [App::DocumentObjectGroupPython] G4_SILVER_HALIDES  # scripted group (container) (typed FeaturePython)
  Dunit = g/cm3
  Dvalue = 6.47
  Group = -> [Br_element006,Ag_element004,I_element007]
  conduct = 2
  density = 1
  expand = 3
  formula = G4_SILVER_HALIDES
  name = G4_SILVER_HALIDES
  specific = 4
FEATURE [App::DocumentObjectGroupPython] Ag_element005  label="Ag_element : 003"  # scripted group (container) (typed FeaturePython)
  n = 1
  ref = Ag_element
FEATURE [App::DocumentObjectGroupPython] I_element008  label="I_element : 004"  # scripted group (container) (typed FeaturePython)
  n = 1
  ref = I_element
FEATURE [App::DocumentObjectGroupPython] G4_SILVER_IODIDE  # scripted group (container) (typed FeaturePython)
  Dunit = g/cm3
  Dvalue = 6.01
  Group = -> [Ag_element005,I_element008]
  conduct = 2
  density = 1
  expand = 3
  formula = G4_SILVER_IODIDE
  name = G4_SILVER_IODIDE
  specific = 4
FEATURE [App::DocumentObjectGroupPython] H_element095  label="H_element : 0.100"  # scripted group (container) (typed FeaturePython)
  n = 0.1
FEATURE [App::DocumentObjectGroupPython] C_element103  label="C_element : 0.204"  # scripted group (container) (typed FeaturePython)
  n = 0.204
FEATURE [App::DocumentObjectGroupPython] N_element039  label="N_element : 0.759"  # scripted group (container) (typed FeaturePython)
  n = 0.042
FEATURE [App::DocumentObjectGroupPython] O_element088  label="O_element : 0.645"  # scripted group (container) (typed FeaturePython)
  n = 0.645
FEATURE [App::DocumentObjectGroupPython] Na_element013  label="Na_element : 0.100"  # scripted group (container) (typed FeaturePython)
  n = 0.002
FEATURE [App::DocumentObjectGroupPython] P_element009  label="P_element : 0.107"  # scripted group (container) (typed FeaturePython)
  n = 0.001
FEATURE [App::DocumentObjectGroupPython] S_element020  label="S_element : 0.021"  # scripted group (container) (typed FeaturePython)
  n = 0.002
FEATURE [App::DocumentObjectGroupPython] Cl_element023  label="Cl_element : 0.590"  # scripted group (container) (typed FeaturePython)
  n = 0.003
FEATURE [App::DocumentObjectGroupPython] K_element010  label="K_element : 0.001"  # scripted group (container) (typed FeaturePython)
  n = 0.001
FEATURE [App::DocumentObjectGroupPython] G4_SKIN_ICRP  # scripted group (container) (typed FeaturePython)
  Dunit = g/cm3
  Dvalue = 1.09
  Group = -> [H_element095,C_element103,N_element039,O_element088,Na_element013,P_element009,S_element020,Cl_element023,K_element010]
  conduct = 2
  density = 1
  expand = 3
  formula = G4_SKIN_ICRP
  name = G4_SKIN_ICRP
  specific = 4
FEATURE [App::DocumentObjectGroupPython] Na_element014  label="Na_element : 2"  # scripted group (container) (typed FeaturePython)
  n = 2
  ref = Na_element
FEATURE [App::DocumentObjectGroupPython] C_element104  label="C_element : 058"  # scripted group (container) (typed FeaturePython)
  n = 1
  ref = C_element
FEATURE [App::DocumentObjectGroupPython] O_element089  label="O_element : 049"  # scripted group (container) (typed FeaturePython)
  n = 3
  ref = O_element
FEATURE [App::DocumentObjectGroupPython] G4_SODIUM_CARBONATE  # scripted group (container) (typed FeaturePython)
  Dunit = g/cm3
  Dvalue = 2.532
  Group = -> [Na_element014,C_element104,O_element089]
  conduct = 2
  density = 1
  expand = 3
  formula = G4_SODIUM_CARBONATE
  name = G4_SODIUM_CARBONATE
  specific = 4
FEATURE [App::DocumentObjectGroupPython] Na_element015  label="Na_element : 1"  # scripted group (container) (typed FeaturePython)
  n = 1
  ref = Na_element
FEATURE [App::DocumentObjectGroupPython] I_element009  label="I_element : 005"  # scripted group (container) (typed FeaturePython)
  n = 1
  ref = I_element
FEATURE [App::DocumentObjectGroupPython] G4_SODIUM_IODIDE  # scripted group (container) (typed FeaturePython)
  Dunit = g/cm3
  Dvalue = 3.667
  Group = -> [Na_element015,I_element009]
  conduct = 2
  density = 1
  expand = 3
  formula = G4_SODIUM_IODIDE
  name = G4_SODIUM_IODIDE
  specific = 4
FEATURE [App::DocumentObjectGroupPython] Na_element016  label="Na_element : 003"  # scripted group (container) (typed FeaturePython)
  n = 2
  ref = Na_element
FEATURE [App::DocumentObjectGroupPython] O_element090  label="O_element : 050"  # scripted group (container) (typed FeaturePython)
  n = 1
  ref = O_element
FEATURE [App::DocumentObjectGroupPython] G4_SODIUM_MONOXIDE  # scripted group (container) (typed FeaturePython)
  Dunit = g/cm3
  Dvalue = 2.27
  Group = -> [Na_element016,O_element090]
  conduct = 2
  density = 1
  expand = 3
  formula = G4_SODIUM_MONOXIDE
  name = G4_SODIUM_MONOXIDE
  specific = 4
FEATURE [App::DocumentObjectGroupPython] Na_element017  label="Na_element : 004"  # scripted group (container) (typed FeaturePython)
  n = 1
  ref = Na_element
FEATURE [App::DocumentObjectGroupPython] N_element040  label="N_element : 018"  # scripted group (container) (typed FeaturePython)
  n = 1
  ref = N_element
FEATURE [App::DocumentObjectGroupPython] O_element091  label="O_element : 051"  # scripted group (container) (typed FeaturePython)
  n = 3
  ref = O_element
FEATURE [App::DocumentObjectGroupPython] G4_SODIUM_NITRATE  # scripted group (container) (typed FeaturePython)
  Dunit = g/cm3
  Dvalue = 2.261
  Group = -> [Na_element017,N_element040,O_element091]
  conduct = 2
  density = 1
  expand = 3
  formula = G4_SODIUM_NITRATE
  name = G4_SODIUM_NITRATE
  specific = 4
FEATURE [App::DocumentObjectGroupPython] C_element105  label="C_element : 059"  # scripted group (container) (typed FeaturePython)
  n = 14
  ref = C_element
FEATURE [App::DocumentObjectGroupPython] H_element096  label="H_element : 053"  # scripted group (container) (typed FeaturePython)
  n = 12
  ref = H_element
FEATURE [App::DocumentObjectGroupPython] G4_STILBENE  # scripted group (container) (typed FeaturePython)
  Dunit = g/cm3
  Dvalue = 0.9707
  Group = -> [C_element105,H_element096]
  conduct = 2
  density = 1
  expand = 3
  formula = G4_STILBENE
  name = G4_STILBENE
  specific = 4
FEATURE [App::DocumentObjectGroupPython] C_element106  label="C_element : 12"  # scripted group (container) (typed FeaturePython)
  n = 12
  ref = C_element
FEATURE [App::DocumentObjectGroupPython] H_element097  label="H_element : 22"  # scripted group (container) (typed FeaturePython)
  n = 22
  ref = H_element
FEATURE [App::DocumentObjectGroupPython] O_element092  label="O_element : 11"  # scripted group (container) (typed FeaturePython)
  n = 11
  ref = O_element
FEATURE [App::DocumentObjectGroupPython] G4_SUCROSE  # scripted group (container) (typed FeaturePython)
  Dunit = g/cm3
  Dvalue = 1.5805
  Group = -> [C_element106,H_element097,O_element092]
  conduct = 2
  density = 1
  expand = 3
  formula = G4_SUCROSE
  name = G4_SUCROSE
  specific = 4
FEATURE [App::DocumentObjectGroupPython] C_element107  label="C_element : 18"  # scripted group (container) (typed FeaturePython)
  n = 18
  ref = C_element
FEATURE [App::DocumentObjectGroupPython] H_element098  label="H_element : 054"  # scripted group (container) (typed FeaturePython)
  n = 14
  ref = H_element
FEATURE [App::DocumentObjectGroupPython] G4_TERPHENYL  # scripted group (container) (typed FeaturePython)
  Dunit = g/cm3
  Dvalue = 1.24
  Group = -> [C_element107,H_element098]
  conduct = 2
  density = 1
  expand = 3
  formula = G4_TERPHENYL
  name = G4_TERPHENYL
  specific = 4
FEATURE [App::DocumentObjectGroupPython] H_element099  label="H_element : 0.146"  # scripted group (container) (typed FeaturePython)
  n = 0.106
FEATURE [App::DocumentObjectGroupPython] C_element108  label="C_element : 0.883"  # scripted group (container) (typed FeaturePython)
  n = 0.099
FEATURE [App::DocumentObjectGroupPython] N_element041  label="N_element : 0.020"  # scripted group (container) (typed FeaturePython)
  n = 0.02
FEATURE [App::DocumentObjectGroupPython] O_element093  label="O_element : 0.766"  # scripted group (container) (typed FeaturePython)
  n = 0.766
FEATURE [App::DocumentObjectGroupPython] Na_element018  label="Na_element : 0.101"  # scripted group (container) (typed FeaturePython)
  n = 0.002
FEATURE [App::DocumentObjectGroupPython] P_element010  label="P_element : 0.108"  # scripted group (container) (typed FeaturePython)
  n = 0.001
FEATURE [App::DocumentObjectGroupPython] S_element021  label="S_element : 0.022"  # scripted group (container) (typed FeaturePython)
  n = 0.002
FEATURE [App::DocumentObjectGroupPython] Cl_element024  label="Cl_element : 0.002"  # scripted group (container) (typed FeaturePython)
  n = 0.002
FEATURE [App::DocumentObjectGroupPython] K_element011  label="K_element : 0.017"  # scripted group (container) (typed FeaturePython)
  n = 0.002
FEATURE [App::DocumentObjectGroupPython] G4_TESTIS_ICRP  # scripted group (container) (typed FeaturePython)
  Dunit = g/cm3
  Dvalue = 1.04
  Group = -> [H_element099,C_element108,N_element041,O_element093,Na_element018,P_element010,S_element021,Cl_element024,K_element011]
  conduct = 2
  density = 1
  expand = 3
  formula = G4_TESTIS_ICRP
  name = G4_TESTIS_ICRP
  specific = 4
FEATURE [App::DocumentObjectGroupPython] C_element109  label="C_element : 060"  # scripted group (container) (typed FeaturePython)
  n = 2
  ref = C_element
FEATURE [App::DocumentObjectGroupPython] Cl_element025  label="Cl_element : 012"  # scripted group (container) (typed FeaturePython)
  n = 4
  ref = Cl_element
FEATURE [App::DocumentObjectGroupPython] G4_TETRACHLOROETHYLENE  # scripted group (container) (typed FeaturePython)
  Dunit = g/cm3
  Dvalue = 1.625
  Group = -> [C_element109,Cl_element025]
  conduct = 2
  density = 1
  expand = 3
  formula = G4_TETRACHLOROETHYLENE
  name = G4_TETRACHLOROETHYLENE
  specific = 4
FEATURE [App::DocumentObjectGroupPython] Tl_element001  label="Tl_element : 1"  # scripted group (container) (typed FeaturePython)
  n = 1
  ref = Tl_element
FEATURE [App::DocumentObjectGroupPython] Cl_element026  label="Cl_element : 013"  # scripted group (container) (typed FeaturePython)
  n = 1
  ref = Cl_element
FEATURE [App::DocumentObjectGroupPython] G4_THALLIUM_CHLORIDE  # scripted group (container) (typed FeaturePython)
  Dunit = g/cm3
  Dvalue = 7.004
  Group = -> [Tl_element001,Cl_element026]
  conduct = 2
  density = 1
  expand = 3
  formula = G4_THALLIUM_CHLORIDE
  name = G4_THALLIUM_CHLORIDE
  specific = 4
FEATURE [App::DocumentObjectGroupPython] H_element100  label="H_element : 0.147"  # scripted group (container) (typed FeaturePython)
  n = 0.105
FEATURE [App::DocumentObjectGroupPython] C_element110  label="C_element : 0.256"  # scripted group (container) (typed FeaturePython)
  n = 0.256
FEATURE [App::DocumentObjectGroupPython] N_element042  label="N_element : 0.760"  # scripted group (container) (typed FeaturePython)
  n = 0.027
FEATURE [App::DocumentObjectGroupPython] O_element094  label="O_element : 0.602"  # scripted group (container) (typed FeaturePython)
  n = 0.602
FEATURE [App::DocumentObjectGroupPython] Na_element019  label="Na_element : 0.102"  # scripted group (container) (typed FeaturePython)
  n = 0.001
FEATURE [App::DocumentObjectGroupPython] P_element011  label="P_element : 0.109"  # scripted group (container) (typed FeaturePython)
  n = 0.002
FEATURE [App::DocumentObjectGroupPython] S_element022  label="S_element : 0.023"  # scripted group (container) (typed FeaturePython)
  n = 0.003
FEATURE [App::DocumentObjectGroupPython] Cl_element027  label="Cl_element : 0.591"  # scripted group (container) (typed FeaturePython)
  n = 0.002
FEATURE [App::DocumentObjectGroupPython] K_element012  label="K_element : 0.018"  # scripted group (container) (typed FeaturePython)
  n = 0.002
FEATURE [App::DocumentObjectGroupPython] G4_TISSUE_SOFT_ICRP  # scripted group (container) (typed FeaturePython)
  Dunit = g/cm3
  Dvalue = 1.03
  Group = -> [H_element100,C_element110,N_element042,O_element094,Na_element019,P_element011,S_element022,Cl_element027,K_element012]
  conduct = 2
  density = 1
  expand = 3
  formula = G4_TISSUE_SOFT_ICRP
  name = G4_TISSUE_SOFT_ICRP
  specific = 4
FEATURE [App::DocumentObjectGroupPython] H_element101  label="H_element : 0.148"  # scripted group (container) (typed FeaturePython)
  n = 0.101
FEATURE [App::DocumentObjectGroupPython] C_element111  label="C_element : 0.111"  # scripted group (container) (typed FeaturePython)
  n = 0.111
FEATURE [App::DocumentObjectGroupPython] N_element043  label="N_element : 0.026"  # scripted group (container) (typed FeaturePython)
  n = 0.026
FEATURE [App::DocumentObjectGroupPython] O_element095  label="O_element : 0.762"  # scripted group (container) (typed FeaturePython)
  n = 0.762
FEATURE [App::DocumentObjectGroupPython] G4_TISSUE_SOFT_ICRU_4  label="G4_TISSUE_SOFT_ICRU-4"  # scripted group (container) (typed FeaturePython)
  Dunit = g/cm3
  Dvalue = 1
  Group = -> [H_element101,C_element111,N_element043,O_element095]
  conduct = 2
  density = 1
  expand = 3
  formula = G4_TISSUE_SOFT_ICRU-4
  name = G4_TISSUE_SOFT_ICRU-4
  specific = 4
FEATURE [App::DocumentObjectGroupPython] H_element102  label="H_element : 0.149"  # scripted group (container) (typed FeaturePython)
  n = 0.101869
FEATURE [App::DocumentObjectGroupPython] C_element112  label="C_element : 0.456"  # scripted group (container) (typed FeaturePython)
  n = 0.456179
FEATURE [App::DocumentObjectGroupPython] N_element044  label="N_element : 0.761"  # scripted group (container) (typed FeaturePython)
  n = 0.035172
FEATURE [App::DocumentObjectGroupPython] O_element096  label="O_element : 0.407"  # scripted group (container) (typed FeaturePython)
  n = 0.40678
FEATURE [App::DocumentObjectGroupPython] G4_TISSUE_METHANE  label="G4_TISSUE-METHANE"  # scripted group (container) (typed FeaturePython)
  Dunit = g/cm3
  Dvalue = 0.00106409
  Group = -> [H_element102,C_element112,N_element044,O_element096]
  conduct = 2
  density = 1
  expand = 3
  formula = G4_TISSUE-METHANE
  name = G4_TISSUE-METHANE
  specific = 4
FEATURE [App::DocumentObjectGroupPython] H_element103  label="H_element : 0.103"  # scripted group (container) (typed FeaturePython)
  n = 0.102672
FEATURE [App::DocumentObjectGroupPython] C_element113  label="C_element : 0.569"  # scripted group (container) (typed FeaturePython)
  n = 0.56894
FEATURE [App::DocumentObjectGroupPython] N_element045  label="N_element : 0.762"  # scripted group (container) (typed FeaturePython)
  n = 0.035022
FEATURE [App::DocumentObjectGroupPython] O_element097  label="O_element : 0.293"  # scripted group (container) (typed FeaturePython)
  n = 0.293366
FEATURE [App::DocumentObjectGroupPython] G4_TISSUE_PROPANE  label="G4_TISSUE-PROPANE"  # scripted group (container) (typed FeaturePython)
  Dunit = g/cm3
  Dvalue = 0.00182628
  Group = -> [H_element103,C_element113,N_element045,O_element097]
  conduct = 2
  density = 1
  expand = 3
  formula = G4_TISSUE-PROPANE
  name = G4_TISSUE-PROPANE
  specific = 4
FEATURE [App::DocumentObjectGroupPython] Ti_element003  label="Ti_element : 1"  # scripted group (container) (typed FeaturePython)
  n = 1
  ref = Ti_element
FEATURE [App::DocumentObjectGroupPython] O_element098  label="O_element : 052"  # scripted group (container) (typed FeaturePython)
  n = 2
  ref = O_element
FEATURE [App::DocumentObjectGroupPython] G4_TITANIUM_DIOXIDE  # scripted group (container) (typed FeaturePython)
  Dunit = g/cm3
  Dvalue = 4.26
  Group = -> [Ti_element003,O_element098]
  conduct = 2
  density = 1
  expand = 3
  formula = G4_TITANIUM_DIOXIDE
  name = G4_TITANIUM_DIOXIDE
  specific = 4
FEATURE [App::DocumentObjectGroupPython] C_element114  label="C_element : 061"  # scripted group (container) (typed FeaturePython)
  n = 7
  ref = C_element
FEATURE [App::DocumentObjectGroupPython] H_element104  label="H_element : 055"  # scripted group (container) (typed FeaturePython)
  n = 8
  ref = H_element
FEATURE [App::DocumentObjectGroupPython] G4_TOLUENE  # scripted group (container) (typed FeaturePython)
  Dunit = g/cm3
  Dvalue = 0.8669
  Group = -> [C_element114,H_element104]
  conduct = 2
  density = 1
  expand = 3
  formula = G4_TOLUENE
  name = G4_TOLUENE
  specific = 4
FEATURE [App::DocumentObjectGroupPython] C_element115  label="C_element : 062"  # scripted group (container) (typed FeaturePython)
  n = 2
  ref = C_element
FEATURE [App::DocumentObjectGroupPython] H_element105  label="H_element : 056"  # scripted group (container) (typed FeaturePython)
  n = 1
  ref = H_element
FEATURE [App::DocumentObjectGroupPython] Cl_element028  label="Cl_element : 014"  # scripted group (container) (typed FeaturePython)
  n = 3
  ref = Cl_element
FEATURE [App::DocumentObjectGroupPython] G4_TRICHLOROETHYLENE  # scripted group (container) (typed FeaturePython)
  Dunit = g/cm3
  Dvalue = 1.46
  Group = -> [C_element115,H_element105,Cl_element028]
  conduct = 2
  density = 1
  expand = 3
  formula = G4_TRICHLOROETHYLENE
  name = G4_TRICHLOROETHYLENE
  specific = 4
FEATURE [App::DocumentObjectGroupPython] C_element116  label="C_element : 063"  # scripted group (container) (typed FeaturePython)
  n = 6
  ref = C_element
FEATURE [App::DocumentObjectGroupPython] H_element106  label="H_element : 15"  # scripted group (container) (typed FeaturePython)
  n = 15
  ref = H_element
FEATURE [App::DocumentObjectGroupPython] O_element099  label="O_element : 053"  # scripted group (container) (typed FeaturePython)
  n = 4
  ref = O_element
FEATURE [App::DocumentObjectGroupPython] P_element012  label="P_element : 1"  # scripted group (container) (typed FeaturePython)
  n = 1
  ref = P_element
FEATURE [App::DocumentObjectGroupPython] G4_TRIETHYL_PHOSPHATE  # scripted group (container) (typed FeaturePython)
  Dunit = g/cm3
  Dvalue = 1.07
  Group = -> [C_element116,H_element106,O_element099,P_element012]
  conduct = 2
  density = 1
  expand = 3
  formula = G4_TRIETHYL_PHOSPHATE
  name = G4_TRIETHYL_PHOSPHATE
  specific = 4
FEATURE [App::DocumentObjectGroupPython] W_element003  label="W_element : 003"  # scripted group (container) (typed FeaturePython)
  n = 1
  ref = W_element
FEATURE [App::DocumentObjectGroupPython] F_element017  label="F_element : 6"  # scripted group (container) (typed FeaturePython)
  n = 6
  ref = F_element
FEATURE [App::DocumentObjectGroupPython] G4_TUNGSTEN_HEXAFLUORIDE  # scripted group (container) (typed FeaturePython)
  Dunit = g/cm3
  Dvalue = 2.4
  Group = -> [W_element003,F_element017]
  conduct = 2
  density = 1
  expand = 3
  formula = G4_TUNGSTEN_HEXAFLUORIDE
  name = G4_TUNGSTEN_HEXAFLUORIDE
  specific = 4
FEATURE [App::DocumentObjectGroupPython] U_element001  label="U_element : 1"  # scripted group (container) (typed FeaturePython)
  n = 1
  ref = U_element
FEATURE [App::DocumentObjectGroupPython] C_element117  label="C_element : 064"  # scripted group (container) (typed FeaturePython)
  n = 2
  ref = C_element
FEATURE [App::DocumentObjectGroupPython] G4_URANIUM_DICARBIDE  # scripted group (container) (typed FeaturePython)
  Dunit = g/cm3
  Dvalue = 11.28
  Group = -> [U_element001,C_element117]
  conduct = 2
  density = 1
  expand = 3
  formula = G4_URANIUM_DICARBIDE
  name = G4_URANIUM_DICARBIDE
  specific = 4
FEATURE [App::DocumentObjectGroupPython] U_element002  label="U_element : 002"  # scripted group (container) (typed FeaturePython)
  n = 1
  ref = U_element
FEATURE [App::DocumentObjectGroupPython] C_element118  label="C_element : 065"  # scripted group (container) (typed FeaturePython)
  n = 1
  ref = C_element
FEATURE [App::DocumentObjectGroupPython] G4_URANIUM_MONOCARBIDE  # scripted group (container) (typed FeaturePython)
  Dunit = g/cm3
  Dvalue = 13.63
  Group = -> [U_element002,C_element118]
  conduct = 2
  density = 1
  expand = 3
  formula = G4_URANIUM_MONOCARBIDE
  name = G4_URANIUM_MONOCARBIDE
  specific = 4
FEATURE [App::DocumentObjectGroupPython] U_element003  label="U_element : 003"  # scripted group (container) (typed FeaturePython)
  n = 1
  ref = U_element
FEATURE [App::DocumentObjectGroupPython] O_element100  label="O_element : 054"  # scripted group (container) (typed FeaturePython)
  n = 2
  ref = O_element
FEATURE [App::DocumentObjectGroupPython] G4_URANIUM_OXIDE  # scripted group (container) (typed FeaturePython)
  Dunit = g/cm3
  Dvalue = 10.96
  Group = -> [U_element003,O_element100]
  conduct = 2
  density = 1
  expand = 3
  formula = G4_URANIUM_OXIDE
  name = G4_URANIUM_OXIDE
  specific = 4
FEATURE [App::DocumentObjectGroupPython] C_element119  label="C_element : 066"  # scripted group (container) (typed FeaturePython)
  n = 1
  ref = C_element
FEATURE [App::DocumentObjectGroupPython] H_element107  label="H_element : 057"  # scripted group (container) (typed FeaturePython)
  n = 4
  ref = H_element
FEATURE [App::DocumentObjectGroupPython] N_element046  label="N_element : 019"  # scripted group (container) (typed FeaturePython)
  n = 2
  ref = N_element
FEATURE [App::DocumentObjectGroupPython] O_element101  label="O_element : 055"  # scripted group (container) (typed FeaturePython)
  n = 1
  ref = O_element
FEATURE [App::DocumentObjectGroupPython] G4_UREA  # scripted group (container) (typed FeaturePython)
  Dunit = g/cm3
  Dvalue = 1.323
  Group = -> [C_element119,H_element107,N_element046,O_element101]
  conduct = 2
  density = 1
  expand = 3
  formula = G4_UREA
  name = G4_UREA
  specific = 4
FEATURE [App::DocumentObjectGroupPython] C_element120  label="C_element : 067"  # scripted group (container) (typed FeaturePython)
  n = 5
  ref = C_element
FEATURE [App::DocumentObjectGroupPython] H_element108  label="H_element : 058"  # scripted group (container) (typed FeaturePython)
  n = 11
  ref = H_element
FEATURE [App::DocumentObjectGroupPython] N_element047  label="N_element : 020"  # scripted group (container) (typed FeaturePython)
  n = 1
  ref = N_element
FEATURE [App::DocumentObjectGroupPython] O_element102  label="O_element : 056"  # scripted group (container) (typed FeaturePython)
  n = 2
  ref = O_element
FEATURE [App::DocumentObjectGroupPython] G4_VALINE  # scripted group (container) (typed FeaturePython)
  Dunit = g/cm3
  Dvalue = 1.23
  Group = -> [C_element120,H_element108,N_element047,O_element102]
  conduct = 2
  density = 1
  expand = 3
  formula = G4_VALINE
  name = G4_VALINE
  specific = 4
FEATURE [App::DocumentObjectGroupPython] H_element109  label="H_element : 0.009"  # scripted group (container) (typed FeaturePython)
  n = 0.009417
FEATURE [App::DocumentObjectGroupPython] C_element121  label="C_element : 0.281"  # scripted group (container) (typed FeaturePython)
  n = 0.280555
FEATURE [App::DocumentObjectGroupPython] F_element018  label="F_element : 0.710"  # scripted group (container) (typed FeaturePython)
  n = 0.710028
FEATURE [App::DocumentObjectGroupPython] G4_VITON  # scripted group (container) (typed FeaturePython)
  Dunit = g/cm3
  Dvalue = 1.8
  Group = -> [H_element109,C_element121,F_element018]
  conduct = 2
  density = 1
  expand = 3
  formula = G4_VITON
  name = G4_VITON
  specific = 4
FEATURE [App::DocumentObjectGroupPython] H_element110  label="H_element : 059"  # scripted group (container) (typed FeaturePython)
  n = 2
  ref = H_element
FEATURE [App::DocumentObjectGroupPython] O_element103  label="O_element : 057"  # scripted group (container) (typed FeaturePython)
  n = 1
  ref = O_element
FEATURE [App::DocumentObjectGroupPython] G4_WATER  # scripted group (container) (typed FeaturePython)
  Dunit = g/cm3
  Dvalue = 1
  Group = -> [H_element110,O_element103]
  conduct = 2
  density = 1
  expand = 3
  formula = G4_WATER
  name = G4_WATER
  specific = 4
FEATURE [App::DocumentObjectGroupPython] H_element111  label="H_element : 060"  # scripted group (container) (typed FeaturePython)
  n = 2
  ref = H_element
FEATURE [App::DocumentObjectGroupPython] O_element104  label="O_element : 058"  # scripted group (container) (typed FeaturePython)
  n = 1
  ref = O_element
FEATURE [App::DocumentObjectGroupPython] G4_WATER_VAPOR  # scripted group (container) (typed FeaturePython)
  Dunit = g/cm3
  Dvalue = 0.000756182
  Group = -> [H_element111,O_element104]
  conduct = 2
  density = 1
  expand = 3
  formula = G4_WATER_VAPOR
  name = G4_WATER_VAPOR
  specific = 4
FEATURE [App::DocumentObjectGroupPython] C_element122  label="C_element : 068"  # scripted group (container) (typed FeaturePython)
  n = 8
  ref = C_element
FEATURE [App::DocumentObjectGroupPython] H_element112  label="H_element : 061"  # scripted group (container) (typed FeaturePython)
  n = 10
  ref = H_element
FEATURE [App::DocumentObjectGroupPython] G4_XYLENE  # scripted group (container) (typed FeaturePython)
  Dunit = g/cm3
  Dvalue = 0.87
  Group = -> [C_element122,H_element112]
  conduct = 2
  density = 1
  expand = 3
  formula = G4_XYLENE
  name = G4_XYLENE
  specific = 4
FEATURE [App::DocumentObjectGroupPython] C_element123  label="C_element : 069"  # scripted group (container) (typed FeaturePython)
  n = 1
  ref = C_element
FEATURE [App::DocumentObjectGroupPython] G4_GRAPHITE  # scripted group (container) (typed FeaturePython)
  Dunit = g/cm3
  Dvalue = 2.21
  Group = -> [C_element123]
  conduct = 2
  density = 1
  expand = 3
  formula = G4_GRAPHITE
  name = G4_GRAPHITE
  specific = 4
FEATURE [App::DocumentObjectGroupPython] NIST  # scripted group (container) (typed FeaturePython)
  Group = -> [G4_A_150_TISSUE,G4_ACETONE,G4_ACETYLENE,G4_ADENINE,G4_ADIPOSE_TISSUE_ICRP,G4_AIR,G4_ALANINE,G4_ALUMINUM_OXIDE,G4_AMBER,G4_AMMONIA,G4_ANILINE,G4_ANTHRACENE,G4_B_100_BONE,G4_BAKELITE,G4_BARIUM_FLUORIDE,G4_BARIUM_SULFATE,G4_BENZENE,G4_BERYLLIUM_OXIDE,G4_BGO,G4_BLOOD_ICRP,G4_BONE_COMPACT_ICRU,G4_BONE_CORTICAL_ICRP,G4_BORON_CARBIDE,G4_BORON_OXIDE,G4_BRAIN_ICRP,G4_BUTANE,G4_N_BUTYL_ALCOHOL,G4_C_552,+152 more]
FEATURE [App::DocumentObjectGroupPython] H_element113  label="H_element : 062"  # scripted group (container) (typed FeaturePython)
  n = 1
  ref = H_element
FEATURE [App::DocumentObjectGroupPython] G4_H  # scripted group (container) (typed FeaturePython)
  Dunit = g/cm3
  Dvalue = 8.3748e-05
  Group = -> [H_element113]
  conduct = 2
  density = 1
  expand = 3
  formula = H
  name = G4_H
  specific = 4
FEATURE [App::DocumentObjectGroupPython] He_element001  label="He_element : 1"  # scripted group (container) (typed FeaturePython)
  n = 1
  ref = He_element
FEATURE [App::DocumentObjectGroupPython] G4_He  # scripted group (container) (typed FeaturePython)
  Dunit = g/cm3
  Dvalue = 0.000166322
  Group = -> [He_element001]
  conduct = 2
  density = 1
  expand = 3
  formula = He
  name = G4_He
  specific = 4
FEATURE [App::DocumentObjectGroupPython] Li_element008  label="Li_element : 008"  # scripted group (container) (typed FeaturePython)
  n = 1
  ref = Li_element
FEATURE [App::DocumentObjectGroupPython] G4_Li  # scripted group (container) (typed FeaturePython)
  Dunit = g/cm3
  Dvalue = 0.534
  Group = -> [Li_element008]
  conduct = 2
  density = 1
  expand = 3
  formula = Li
  name = G4_Li
  specific = 4
FEATURE [App::DocumentObjectGroupPython] Be_element002  label="Be_element : 002"  # scripted group (container) (typed FeaturePython)
  n = 1
  ref = Be_element
FEATURE [App::DocumentObjectGroupPython] G4_Be  # scripted group (container) (typed FeaturePython)
  Dunit = g/cm3
  Dvalue = 1.848
  Group = -> [Be_element002]
  conduct = 2
  density = 1
  expand = 3
  formula = Be
  name = G4_Be
  specific = 4
FEATURE [App::DocumentObjectGroupPython] B_element007  label="B_element : 007"  # scripted group (container) (typed FeaturePython)
  n = 1
  ref = B_element
FEATURE [App::DocumentObjectGroupPython] G4_B  # scripted group (container) (typed FeaturePython)
  Dunit = g/cm3
  Dvalue = 2.37
  Group = -> [B_element007]
  conduct = 2
  density = 1
  expand = 3
  formula = B
  name = G4_B
  specific = 4
FEATURE [App::DocumentObjectGroupPython] C_element124  label="C_element : 070"  # scripted group (container) (typed FeaturePython)
  n = 1
  ref = C_element
FEATURE [App::DocumentObjectGroupPython] G4_C  # scripted group (container) (typed FeaturePython)
  Dunit = g/cm3
  Dvalue = 2
  Group = -> [C_element124]
  conduct = 2
  density = 1
  expand = 3
  formula = C
  name = G4_C
  specific = 4
FEATURE [App::DocumentObjectGroupPython] N_element048  label="N_element : 021"  # scripted group (container) (typed FeaturePython)
  n = 1
  ref = N_element
FEATURE [App::DocumentObjectGroupPython] G4_N  # scripted group (container) (typed FeaturePython)
  Dunit = g/cm3
  Dvalue = 0.0011652
  Group = -> [N_element048]
  conduct = 2
  density = 1
  expand = 3
  formula = N
  name = G4_N
  specific = 4
FEATURE [App::DocumentObjectGroupPython] O_element105  label="O_element : 059"  # scripted group (container) (typed FeaturePython)
  n = 1
  ref = O_element
FEATURE [App::DocumentObjectGroupPython] G4_O  # scripted group (container) (typed FeaturePython)
  Dunit = g/cm3
  Dvalue = 0.00133151
  Group = -> [O_element105]
  conduct = 2
  density = 1
  expand = 3
  formula = O
  name = G4_O
  specific = 4
FEATURE [App::DocumentObjectGroupPython] F_element019  label="F_element : 008"  # scripted group (container) (typed FeaturePython)
  n = 1
  ref = F_element
FEATURE [App::DocumentObjectGroupPython] G4_F  # scripted group (container) (typed FeaturePython)
  Dunit = g/cm3
  Dvalue = 0.00158029
  Group = -> [F_element019]
  conduct = 2
  density = 1
  expand = 3
  formula = F
  name = G4_F
  specific = 4
FEATURE [App::DocumentObjectGroupPython] Ne_element001  label="Ne_element : 1"  # scripted group (container) (typed FeaturePython)
  n = 1
  ref = Ne_element
FEATURE [App::DocumentObjectGroupPython] G4_Ne  # scripted group (container) (typed FeaturePython)
  Dunit = g/cm3
  Dvalue = 0.000838505
  Group = -> [Ne_element001]
  conduct = 2
  density = 1
  expand = 3
  formula = Ne
  name = G4_Ne
  specific = 4
FEATURE [App::DocumentObjectGroupPython] Na_element020  label="Na_element : 005"  # scripted group (container) (typed FeaturePython)
  n = 1
  ref = Na_element
FEATURE [App::DocumentObjectGroupPython] G4_Na  # scripted group (container) (typed FeaturePython)
  Dunit = g/cm3
  Dvalue = 0.971
  Group = -> [Na_element020]
  conduct = 2
  density = 1
  expand = 3
  formula = Na
  name = G4_Na
  specific = 4
FEATURE [App::DocumentObjectGroupPython] Mg_element011  label="Mg_element : 005"  # scripted group (container) (typed FeaturePython)
  n = 1
  ref = Mg_element
FEATURE [App::DocumentObjectGroupPython] G4_Mg  # scripted group (container) (typed FeaturePython)
  Dunit = g/cm3
  Dvalue = 1.74
  Group = -> [Mg_element011]
  conduct = 2
  density = 1
  expand = 3
  formula = Mg
  name = G4_Mg
  specific = 4
FEATURE [App::DocumentObjectGroupPython] Al_element004  label="Al_element : 1"  # scripted group (container) (typed FeaturePython)
  n = 1
  ref = Al_element
FEATURE [App::DocumentObjectGroupPython] G4_Al  # scripted group (container) (typed FeaturePython)
  Dunit = g/cm3
  Dvalue = 2.699
  Group = -> [Al_element004]
  conduct = 2
  density = 1
  expand = 3
  formula = Al
  name = G4_Al
  specific = 4
FEATURE [App::DocumentObjectGroupPython] Si_element007  label="Si_element : 002"  # scripted group (container) (typed FeaturePython)
  n = 1
  ref = Si_element
FEATURE [App::DocumentObjectGroupPython] G4_Si  # scripted group (container) (typed FeaturePython)
  Dunit = g/cm3
  Dvalue = 2.33
  Group = -> [Si_element007]
  conduct = 2
  density = 1
  expand = 3
  formula = Si
  name = G4_Si
  specific = 4
FEATURE [App::DocumentObjectGroupPython] P_element013  label="P_element : 002"  # scripted group (container) (typed FeaturePython)
  n = 1
  ref = P_element
FEATURE [App::DocumentObjectGroupPython] G4_P  # scripted group (container) (typed FeaturePython)
  Dunit = g/cm3
  Dvalue = 2.2
  Group = -> [P_element013]
  conduct = 2
  density = 1
  expand = 3
  formula = P
  name = G4_P
  specific = 4
FEATURE [App::DocumentObjectGroupPython] S_element023  label="S_element : 007"  # scripted group (container) (typed FeaturePython)
  n = 1
  ref = S_element
FEATURE [App::DocumentObjectGroupPython] G4_S  # scripted group (container) (typed FeaturePython)
  Dunit = g/cm3
  Dvalue = 2
  Group = -> [S_element023]
  conduct = 2
  density = 1
  expand = 3
  formula = S
  name = G4_S
  specific = 4
FEATURE [App::DocumentObjectGroupPython] Cl_element029  label="Cl_element : 015"  # scripted group (container) (typed FeaturePython)
  n = 1
  ref = Cl_element
FEATURE [App::DocumentObjectGroupPython] G4_Cl  # scripted group (container) (typed FeaturePython)
  Dunit = g/cm3
  Dvalue = 0.00299473
  Group = -> [Cl_element029]
  conduct = 2
  density = 1
  expand = 3
  formula = Cl
  name = G4_Cl
  specific = 4
FEATURE [App::DocumentObjectGroupPython] Ar_element002  label="Ar_element : 1"  # scripted group (container) (typed FeaturePython)
  n = 1
  ref = Ar_element
FEATURE [App::DocumentObjectGroupPython] G4_Ar  # scripted group (container) (typed FeaturePython)
  Dunit = g/cm3
  Dvalue = 0.00166201
  Group = -> [Ar_element002]
  conduct = 2
  density = 1
  expand = 3
  formula = Ar
  name = G4_Ar
  specific = 4
FEATURE [App::DocumentObjectGroupPython] K_element013  label="K_element : 003"  # scripted group (container) (typed FeaturePython)
  n = 1
  ref = K_element
FEATURE [App::DocumentObjectGroupPython] G4_K  # scripted group (container) (typed FeaturePython)
  Dunit = g/cm3
  Dvalue = 0.862
  Group = -> [K_element013]
  conduct = 2
  density = 1
  expand = 3
  formula = K
  name = G4_K
  specific = 4
FEATURE [App::DocumentObjectGroupPython] Ca_element014  label="Ca_element : 007"  # scripted group (container) (typed FeaturePython)
  n = 1
  ref = Ca_element
FEATURE [App::DocumentObjectGroupPython] G4_Ca  # scripted group (container) (typed FeaturePython)
  Dunit = g/cm3
  Dvalue = 1.55
  Group = -> [Ca_element014]
  conduct = 2
  density = 1
  expand = 3
  formula = Ca
  name = G4_Ca
  specific = 4
FEATURE [App::DocumentObjectGroupPython] Sc_element001  label="Sc_element : 1"  # scripted group (container) (typed FeaturePython)
  n = 1
  ref = Sc_element
FEATURE [App::DocumentObjectGroupPython] G4_Sc  # scripted group (container) (typed FeaturePython)
  Dunit = g/cm3
  Dvalue = 2.989
  Group = -> [Sc_element001]
  conduct = 2
  density = 1
  expand = 3
  formula = Sc
  name = G4_Sc
  specific = 4
FEATURE [App::DocumentObjectGroupPython] Ti_element004  label="Ti_element : 002"  # scripted group (container) (typed FeaturePython)
  n = 1
  ref = Ti_element
FEATURE [App::DocumentObjectGroupPython] G4_Ti  # scripted group (container) (typed FeaturePython)
  Dunit = g/cm3
  Dvalue = 4.54
  Group = -> [Ti_element004]
  conduct = 2
  density = 1
  expand = 3
  formula = Ti
  name = G4_Ti
  specific = 4
FEATURE [App::DocumentObjectGroupPython] V_element001  label="V_element : 1"  # scripted group (container) (typed FeaturePython)
  n = 1
  ref = V_element
FEATURE [App::DocumentObjectGroupPython] G4_V  # scripted group (container) (typed FeaturePython)
  Dunit = g/cm3
  Dvalue = 6.11
  Group = -> [V_element001]
  conduct = 2
  density = 1
  expand = 3
  formula = V
  name = G4_V
  specific = 4
FEATURE [App::DocumentObjectGroupPython] Cr_element001  label="Cr_element : 1"  # scripted group (container) (typed FeaturePython)
  n = 1
  ref = Cr_element
FEATURE [App::DocumentObjectGroupPython] G4_Cr  # scripted group (container) (typed FeaturePython)
  Dunit = g/cm3
  Dvalue = 7.18
  Group = -> [Cr_element001]
  conduct = 2
  density = 1
  expand = 3
  formula = Cr
  name = G4_Cr
  specific = 4
FEATURE [App::DocumentObjectGroupPython] Mn_element001  label="Mn_element : 1"  # scripted group (container) (typed FeaturePython)
  n = 1
  ref = Mn_element
FEATURE [App::DocumentObjectGroupPython] G4_Mn  # scripted group (container) (typed FeaturePython)
  Dunit = g/cm3
  Dvalue = 7.44
  Group = -> [Mn_element001]
  conduct = 2
  density = 1
  expand = 3
  formula = Mn
  name = G4_Mn
  specific = 4
FEATURE [App::DocumentObjectGroupPython] Fe_element007  label="Fe_element : 004"  # scripted group (container) (typed FeaturePython)
  n = 1
  ref = Fe_element
FEATURE [App::DocumentObjectGroupPython] G4_Fe  # scripted group (container) (typed FeaturePython)
  Dunit = g/cm3
  Dvalue = 7.874
  Group = -> [Fe_element007]
  conduct = 2
  density = 1
  expand = 3
  formula = Fe
  name = G4_Fe
  specific = 4
FEATURE [App::DocumentObjectGroupPython] Co_element001  label="Co_element : 1"  # scripted group (container) (typed FeaturePython)
  n = 1
  ref = Co_element
FEATURE [App::DocumentObjectGroupPython] G4_Co  # scripted group (container) (typed FeaturePython)
  Dunit = g/cm3
  Dvalue = 8.9
  Group = -> [Co_element001]
  conduct = 2
  density = 1
  expand = 3
  formula = Co
  name = G4_Co
  specific = 4
FEATURE [App::DocumentObjectGroupPython] Ni_element001  label="Ni_element : 1"  # scripted group (container) (typed FeaturePython)
  n = 1
  ref = Ni_element
FEATURE [App::DocumentObjectGroupPython] G4_Ni  # scripted group (container) (typed FeaturePython)
  Dunit = g/cm3
  Dvalue = 8.902
  Group = -> [Ni_element001]
  conduct = 2
  density = 1
  expand = 3
  formula = Ni
  name = G4_Ni
  specific = 4
FEATURE [App::DocumentObjectGroupPython] Cu_element001  label="Cu_element : 1"  # scripted group (container) (typed FeaturePython)
  n = 1
  ref = Cu_element
FEATURE [App::DocumentObjectGroupPython] G4_Cu  # scripted group (container) (typed FeaturePython)
  Dunit = g/cm3
  Dvalue = 8.96
  Group = -> [Cu_element001]
  conduct = 2
  density = 1
  expand = 3
  formula = Cu
  name = G4_Cu
  specific = 4
FEATURE [App::DocumentObjectGroupPython] Zn_element001  label="Zn_element : 1"  # scripted group (container) (typed FeaturePython)
  n = 1
  ref = Zn_element
FEATURE [App::DocumentObjectGroupPython] G4_Zn  # scripted group (container) (typed FeaturePython)
  Dunit = g/cm3
  Dvalue = 7.133
  Group = -> [Zn_element001]
  conduct = 2
  density = 1
  expand = 3
  formula = Zn
  name = G4_Zn
  specific = 4
FEATURE [App::DocumentObjectGroupPython] Ga_element002  label="Ga_element : 002"  # scripted group (container) (typed FeaturePython)
  n = 1
  ref = Ga_element
FEATURE [App::DocumentObjectGroupPython] G4_Ga  # scripted group (container) (typed FeaturePython)
  Dunit = g/cm3
  Dvalue = 5.904
  Group = -> [Ga_element002]
  conduct = 2
  density = 1
  expand = 3
  formula = Ga
  name = G4_Ga
  specific = 4
FEATURE [App::DocumentObjectGroupPython] Ge_element002  label="Ge_element : 1"  # scripted group (container) (typed FeaturePython)
  n = 1
  ref = Ge_element
FEATURE [App::DocumentObjectGroupPython] G4_Ge  # scripted group (container) (typed FeaturePython)
  Dunit = g/cm3
  Dvalue = 5.323
  Group = -> [Ge_element002]
  conduct = 2
  density = 1
  expand = 3
  formula = Ge
  name = G4_Ge
  specific = 4
FEATURE [App::DocumentObjectGroupPython] As_element003  label="As_element : 002"  # scripted group (container) (typed FeaturePython)
  n = 1
  ref = As_element
FEATURE [App::DocumentObjectGroupPython] G4_As  # scripted group (container) (typed FeaturePython)
  Dunit = g/cm3
  Dvalue = 5.73
  Group = -> [As_element003]
  conduct = 2
  density = 1
  expand = 3
  formula = As
  name = G4_As
  specific = 4
FEATURE [App::DocumentObjectGroupPython] Se_element001  label="Se_element : 1"  # scripted group (container) (typed FeaturePython)
  n = 1
  ref = Se_element
FEATURE [App::DocumentObjectGroupPython] G4_Se  # scripted group (container) (typed FeaturePython)
  Dunit = g/cm3
  Dvalue = 4.5
  Group = -> [Se_element001]
  conduct = 2
  density = 1
  expand = 3
  formula = Se
  name = G4_Se
  specific = 4
FEATURE [App::DocumentObjectGroupPython] Br_element007  label="Br_element : 004"  # scripted group (container) (typed FeaturePython)
  n = 1
  ref = Br_element
FEATURE [App::DocumentObjectGroupPython] G4_Br  # scripted group (container) (typed FeaturePython)
  Dunit = g/cm3
  Dvalue = 0.0070721
  Group = -> [Br_element007]
  conduct = 2
  density = 1
  expand = 3
  formula = Br
  name = G4_Br
  specific = 4
FEATURE [App::DocumentObjectGroupPython] Kr_element001  label="Kr_element : 1"  # scripted group (container) (typed FeaturePython)
  n = 1
  ref = Kr_element
FEATURE [App::DocumentObjectGroupPython] G4_Kr  # scripted group (container) (typed FeaturePython)
  Dunit = g/cm3
  Dvalue = 0.00347832
  Group = -> [Kr_element001]
  conduct = 2
  density = 1
  expand = 3
  formula = Kr
  name = G4_Kr
  specific = 4
FEATURE [App::DocumentObjectGroupPython] Rb_element001  label="Rb_element : 1"  # scripted group (container) (typed FeaturePython)
  n = 1
  ref = Rb_element
FEATURE [App::DocumentObjectGroupPython] G4_Rb  # scripted group (container) (typed FeaturePython)
  Dunit = g/cm3
  Dvalue = 1.532
  Group = -> [Rb_element001]
  conduct = 2
  density = 1
  expand = 3
  formula = Rb
  name = G4_Rb
  specific = 4
FEATURE [App::DocumentObjectGroupPython] Sr_element001  label="Sr_element : 1"  # scripted group (container) (typed FeaturePython)
  n = 1
  ref = Sr_element
FEATURE [App::DocumentObjectGroupPython] G4_Sr  # scripted group (container) (typed FeaturePython)
  Dunit = g/cm3
  Dvalue = 2.54
  Group = -> [Sr_element001]
  conduct = 2
  density = 1
  expand = 3
  formula = Sr
  name = G4_Sr
  specific = 4
FEATURE [App::DocumentObjectGroupPython] Y_element001  label="Y_element : 1"  # scripted group (container) (typed FeaturePython)
  n = 1
  ref = Y_element
FEATURE [App::DocumentObjectGroupPython] G4_Y  # scripted group (container) (typed FeaturePython)
  Dunit = g/cm3
  Dvalue = 4.469
  Group = -> [Y_element001]
  conduct = 2
  density = 1
  expand = 3
  formula = Y
  name = G4_Y
  specific = 4
FEATURE [App::DocumentObjectGroupPython] Zr_element001  label="Zr_element : 1"  # scripted group (container) (typed FeaturePython)
  n = 1
  ref = Zr_element
FEATURE [App::DocumentObjectGroupPython] G4_Zr  # scripted group (container) (typed FeaturePython)
  Dunit = g/cm3
  Dvalue = 6.506
  Group = -> [Zr_element001]
  conduct = 2
  density = 1
  expand = 3
  formula = Zr
  name = G4_Zr
  specific = 4
FEATURE [App::DocumentObjectGroupPython] Nb_element001  label="Nb_element : 1"  # scripted group (container) (typed FeaturePython)
  n = 1
  ref = Nb_element
FEATURE [App::DocumentObjectGroupPython] G4_Nb  # scripted group (container) (typed FeaturePython)
  Dunit = g/cm3
  Dvalue = 8.57
  Group = -> [Nb_element001]
  conduct = 2
  density = 1
  expand = 3
  formula = Nb
  name = G4_Nb
  specific = 4
FEATURE [App::DocumentObjectGroupPython] Mo_element001  label="Mo_element : 1"  # scripted group (container) (typed FeaturePython)
  n = 1
  ref = Mo_element
FEATURE [App::DocumentObjectGroupPython] G4_Mo  # scripted group (container) (typed FeaturePython)
  Dunit = g/cm3
  Dvalue = 10.22
  Group = -> [Mo_element001]
  conduct = 2
  density = 1
  expand = 3
  formula = Mo
  name = G4_Mo
  specific = 4
FEATURE [App::DocumentObjectGroupPython] Tc_element001  label="Tc_element : 1"  # scripted group (container) (typed FeaturePython)
  n = 1
  ref = Tc_element
FEATURE [App::DocumentObjectGroupPython] G4_Tc  # scripted group (container) (typed FeaturePython)
  Dunit = g/cm3
  Dvalue = 11.5
  Group = -> [Tc_element001]
  conduct = 2
  density = 1
  expand = 3
  formula = Tc
  name = G4_Tc
  specific = 4
FEATURE [App::DocumentObjectGroupPython] Ru_element001  label="Ru_element : 1"  # scripted group (container) (typed FeaturePython)
  n = 1
  ref = Ru_element
FEATURE [App::DocumentObjectGroupPython] G4_Ru  # scripted group (container) (typed FeaturePython)
  Dunit = g/cm3
  Dvalue = 12.41
  Group = -> [Ru_element001]
  conduct = 2
  density = 1
  expand = 3
  formula = Ru
  name = G4_Ru
  specific = 4
FEATURE [App::DocumentObjectGroupPython] Rh_element001  label="Rh_element : 1"  # scripted group (container) (typed FeaturePython)
  n = 1
  ref = Rh_element
FEATURE [App::DocumentObjectGroupPython] G4_Rh  # scripted group (container) (typed FeaturePython)
  Dunit = g/cm3
  Dvalue = 12.41
  Group = -> [Rh_element001]
  conduct = 2
  density = 1
  expand = 3
  formula = Rh
  name = G4_Rh
  specific = 4
FEATURE [App::DocumentObjectGroupPython] Pd_element001  label="Pd_element : 1"  # scripted group (container) (typed FeaturePython)
  n = 1
  ref = Pd_element
FEATURE [App::DocumentObjectGroupPython] G4_Pd  # scripted group (container) (typed FeaturePython)
  Dunit = g/cm3
  Dvalue = 12.02
  Group = -> [Pd_element001]
  conduct = 2
  density = 1
  expand = 3
  formula = Pd
  name = G4_Pd
  specific = 4
FEATURE [App::DocumentObjectGroupPython] Ag_element006  label="Ag_element : 004"  # scripted group (container) (typed FeaturePython)
  n = 1
  ref = Ag_element
FEATURE [App::DocumentObjectGroupPython] G4_Ag  # scripted group (container) (typed FeaturePython)
  Dunit = g/cm3
  Dvalue = 10.5
  Group = -> [Ag_element006]
  conduct = 2
  density = 1
  expand = 3
  formula = Ag
  name = G4_Ag
  specific = 4
FEATURE [App::DocumentObjectGroupPython] Cd_element003  label="Cd_element : 003"  # scripted group (container) (typed FeaturePython)
  n = 1
  ref = Cd_element
FEATURE [App::DocumentObjectGroupPython] G4_Cd  # scripted group (container) (typed FeaturePython)
  Dunit = g/cm3
  Dvalue = 8.65
  Group = -> [Cd_element003]
  conduct = 2
  density = 1
  expand = 3
  formula = Cd
  name = G4_Cd
  specific = 4
FEATURE [App::DocumentObjectGroupPython] In_element001  label="In_element : 1"  # scripted group (container) (typed FeaturePython)
  n = 1
  ref = In_element
FEATURE [App::DocumentObjectGroupPython] G4_In  # scripted group (container) (typed FeaturePython)
  Dunit = g/cm3
  Dvalue = 7.31
  Group = -> [In_element001]
  conduct = 2
  density = 1
  expand = 3
  formula = In
  name = G4_In
  specific = 4
FEATURE [App::DocumentObjectGroupPython] Sn_element001  label="Sn_element : 1"  # scripted group (container) (typed FeaturePython)
  n = 1
  ref = Sn_element
FEATURE [App::DocumentObjectGroupPython] G4_Sn  # scripted group (container) (typed FeaturePython)
  Dunit = g/cm3
  Dvalue = 7.31
  Group = -> [Sn_element001]
  conduct = 2
  density = 1
  expand = 3
  formula = Sn
  name = G4_Sn
  specific = 4
FEATURE [App::DocumentObjectGroupPython] Sb_element001  label="Sb_element : 1"  # scripted group (container) (typed FeaturePython)
  n = 1
  ref = Sb_element
FEATURE [App::DocumentObjectGroupPython] G4_Sb  # scripted group (container) (typed FeaturePython)
  Dunit = g/cm3
  Dvalue = 6.691
  Group = -> [Sb_element001]
  conduct = 2
  density = 1
  expand = 3
  formula = Sb
  name = G4_Sb
  specific = 4
FEATURE [App::DocumentObjectGroupPython] Te_element002  label="Te_element : 002"  # scripted group (container) (typed FeaturePython)
  n = 1
  ref = Te_element
FEATURE [App::DocumentObjectGroupPython] G4_Te  # scripted group (container) (typed FeaturePython)
  Dunit = g/cm3
  Dvalue = 6.24
  Group = -> [Te_element002]
  conduct = 2
  density = 1
  expand = 3
  formula = Te
  name = G4_Te
  specific = 4
FEATURE [App::DocumentObjectGroupPython] I_element010  label="I_element : 006"  # scripted group (container) (typed FeaturePython)
  n = 1
  ref = I_element
FEATURE [App::DocumentObjectGroupPython] G4_I  # scripted group (container) (typed FeaturePython)
  Dunit = g/cm3
  Dvalue = 4.93
  Group = -> [I_element010]
  conduct = 2
  density = 1
  expand = 3
  formula = I
  name = G4_I
  specific = 4
FEATURE [App::DocumentObjectGroupPython] Xe_element001  label="Xe_element : 1"  # scripted group (container) (typed FeaturePython)
  n = 1
  ref = Xe_element
FEATURE [App::DocumentObjectGroupPython] G4_Xe  # scripted group (container) (typed FeaturePython)
  Dunit = g/cm3
  Dvalue = 0.00548536
  Group = -> [Xe_element001]
  conduct = 2
  density = 1
  expand = 3
  formula = Xe
  name = G4_Xe
  specific = 4
FEATURE [App::DocumentObjectGroupPython] Cs_element003  label="Cs_element : 003"  # scripted group (container) (typed FeaturePython)
  n = 1
  ref = Cs_element
FEATURE [App::DocumentObjectGroupPython] G4_Cs  # scripted group (container) (typed FeaturePython)
  Dunit = g/cm3
  Dvalue = 1.873
  Group = -> [Cs_element003]
  conduct = 2
  density = 1
  expand = 3
  formula = Cs
  name = G4_Cs
  specific = 4
FEATURE [App::DocumentObjectGroupPython] Ba_element003  label="Ba_element : 003"  # scripted group (container) (typed FeaturePython)
  n = 1
  ref = Ba_element
FEATURE [App::DocumentObjectGroupPython] G4_Ba  # scripted group (container) (typed FeaturePython)
  Dunit = g/cm3
  Dvalue = 3.5
  Group = -> [Ba_element003]
  conduct = 2
  density = 1
  expand = 3
  formula = Ba
  name = G4_Ba
  specific = 4
FEATURE [App::DocumentObjectGroupPython] La_element003  label="La_element : 003"  # scripted group (container) (typed FeaturePython)
  n = 1
  ref = La_element
FEATURE [App::DocumentObjectGroupPython] G4_La  # scripted group (container) (typed FeaturePython)
  Dunit = g/cm3
  Dvalue = 6.154
  Group = -> [La_element003]
  conduct = 2
  density = 1
  expand = 3
  formula = La
  name = G4_La
  specific = 4
FEATURE [App::DocumentObjectGroupPython] Ce_element002  label="Ce_element : 1"  # scripted group (container) (typed FeaturePython)
  n = 1
  ref = Ce_element
FEATURE [App::DocumentObjectGroupPython] G4_Ce  # scripted group (container) (typed FeaturePython)
  Dunit = g/cm3
  Dvalue = 6.657
  Group = -> [Ce_element002]
  conduct = 2
  density = 1
  expand = 3
  formula = Ce
  name = G4_Ce
  specific = 4
FEATURE [App::DocumentObjectGroupPython] Pr_element001  label="Pr_element : 1"  # scripted group (container) (typed FeaturePython)
  n = 1
  ref = Pr_element
FEATURE [App::DocumentObjectGroupPython] G4_Pr  # scripted group (container) (typed FeaturePython)
  Dunit = g/cm3
  Dvalue = 6.71
  Group = -> [Pr_element001]
  conduct = 2
  density = 1
  expand = 3
  formula = Pr
  name = G4_Pr
  specific = 4
FEATURE [App::DocumentObjectGroupPython] Nd_element001  label="Nd_element : 1"  # scripted group (container) (typed FeaturePython)
  n = 1
  ref = Nd_element
FEATURE [App::DocumentObjectGroupPython] G4_Nd  # scripted group (container) (typed FeaturePython)
  Dunit = g/cm3
  Dvalue = 6.9
  Group = -> [Nd_element001]
  conduct = 2
  density = 1
  expand = 3
  formula = Nd
  name = G4_Nd
  specific = 4
FEATURE [App::DocumentObjectGroupPython] Pm_element001  label="Pm_element : 1"  # scripted group (container) (typed FeaturePython)
  n = 1
  ref = Pm_element
FEATURE [App::DocumentObjectGroupPython] G4_Pm  # scripted group (container) (typed FeaturePython)
  Dunit = g/cm3
  Dvalue = 7.22
  Group = -> [Pm_element001]
  conduct = 2
  density = 1
  expand = 3
  formula = Pm
  name = G4_Pm
  specific = 4
FEATURE [App::DocumentObjectGroupPython] Sm_element001  label="Sm_element : 1"  # scripted group (container) (typed FeaturePython)
  n = 1
  ref = Sm_element
FEATURE [App::DocumentObjectGroupPython] G4_Sm  # scripted group (container) (typed FeaturePython)
  Dunit = g/cm3
  Dvalue = 7.46
  Group = -> [Sm_element001]
  conduct = 2
  density = 1
  expand = 3
  formula = Sm
  name = G4_Sm
  specific = 4
FEATURE [App::DocumentObjectGroupPython] Eu_element001  label="Eu_element : 1"  # scripted group (container) (typed FeaturePython)
  n = 1
  ref = Eu_element
FEATURE [App::DocumentObjectGroupPython] G4_Eu  # scripted group (container) (typed FeaturePython)
  Dunit = g/cm3
  Dvalue = 5.243
  Group = -> [Eu_element001]
  conduct = 2
  density = 1
  expand = 3
  formula = Eu
  name = G4_Eu
  specific = 4
FEATURE [App::DocumentObjectGroupPython] Gd_element002  label="Gd_element : 1"  # scripted group (container) (typed FeaturePython)
  n = 1
  ref = Gd_element
FEATURE [App::DocumentObjectGroupPython] G4_Gd  # scripted group (container) (typed FeaturePython)
  Dunit = g/cm3
  Dvalue = 7.9004
  Group = -> [Gd_element002]
  conduct = 2
  density = 1
  expand = 3
  formula = Gd
  name = G4_Gd
  specific = 4
FEATURE [App::DocumentObjectGroupPython] Tb_element001  label="Tb_element : 1"  # scripted group (container) (typed FeaturePython)
  n = 1
  ref = Tb_element
FEATURE [App::DocumentObjectGroupPython] G4_Tb  # scripted group (container) (typed FeaturePython)
  Dunit = g/cm3
  Dvalue = 8.229
  Group = -> [Tb_element001]
  conduct = 2
  density = 1
  expand = 3
  formula = Tb
  name = G4_Tb
  specific = 4
FEATURE [App::DocumentObjectGroupPython] Dy_element001  label="Dy_element : 1"  # scripted group (container) (typed FeaturePython)
  n = 1
  ref = Dy_element
FEATURE [App::DocumentObjectGroupPython] G4_Dy  # scripted group (container) (typed FeaturePython)
  Dunit = g/cm3
  Dvalue = 8.55
  Group = -> [Dy_element001]
  conduct = 2
  density = 1
  expand = 3
  formula = Dy
  name = G4_Dy
  specific = 4
FEATURE [App::DocumentObjectGroupPython] Ho_element001  label="Ho_element : 1"  # scripted group (container) (typed FeaturePython)
  n = 1
  ref = Ho_element
FEATURE [App::DocumentObjectGroupPython] G4_Ho  # scripted group (container) (typed FeaturePython)
  Dunit = g/cm3
  Dvalue = 8.795
  Group = -> [Ho_element001]
  conduct = 2
  density = 1
  expand = 3
  formula = Ho
  name = G4_Ho
  specific = 4
FEATURE [App::DocumentObjectGroupPython] Er_element001  label="Er_element : 1"  # scripted group (container) (typed FeaturePython)
  n = 1
  ref = Er_element
FEATURE [App::DocumentObjectGroupPython] G4_Er  # scripted group (container) (typed FeaturePython)
  Dunit = g/cm3
  Dvalue = 9.066
  Group = -> [Er_element001]
  conduct = 2
  density = 1
  expand = 3
  formula = Er
  name = G4_Er
  specific = 4
FEATURE [App::DocumentObjectGroupPython] Tm_element001  label="Tm_element : 1"  # scripted group (container) (typed FeaturePython)
  n = 1
  ref = Tm_element
FEATURE [App::DocumentObjectGroupPython] G4_Tm  # scripted group (container) (typed FeaturePython)
  Dunit = g/cm3
  Dvalue = 9.321
  Group = -> [Tm_element001]
  conduct = 2
  density = 1
  expand = 3
  formula = Tm
  name = G4_Tm
  specific = 4
FEATURE [App::DocumentObjectGroupPython] Yb_element001  label="Yb_element : 1"  # scripted group (container) (typed FeaturePython)
  n = 1
  ref = Yb_element
FEATURE [App::DocumentObjectGroupPython] G4_Yb  # scripted group (container) (typed FeaturePython)
  Dunit = g/cm3
  Dvalue = 6.73
  Group = -> [Yb_element001]
  conduct = 2
  density = 1
  expand = 3
  formula = Yb
  name = G4_Yb
  specific = 4
FEATURE [App::DocumentObjectGroupPython] Lu_element001  label="Lu_element : 1"  # scripted group (container) (typed FeaturePython)
  n = 1
  ref = Lu_element
FEATURE [App::DocumentObjectGroupPython] G4_Lu  # scripted group (container) (typed FeaturePython)
  Dunit = g/cm3
  Dvalue = 9.84
  Group = -> [Lu_element001]
  conduct = 2
  density = 1
  expand = 3
  formula = Lu
  name = G4_Lu
  specific = 4
FEATURE [App::DocumentObjectGroupPython] Hf_element001  label="Hf_element : 1"  # scripted group (container) (typed FeaturePython)
  n = 1
  ref = Hf_element
FEATURE [App::DocumentObjectGroupPython] G4_Hf  # scripted group (container) (typed FeaturePython)
  Dunit = g/cm3
  Dvalue = 13.31
  Group = -> [Hf_element001]
  conduct = 2
  density = 1
  expand = 3
  formula = Hf
  name = G4_Hf
  specific = 4
FEATURE [App::DocumentObjectGroupPython] Ta_element001  label="Ta_element : 1"  # scripted group (container) (typed FeaturePython)
  n = 1
  ref = Ta_element
FEATURE [App::DocumentObjectGroupPython] G4_Ta  # scripted group (container) (typed FeaturePython)
  Dunit = g/cm3
  Dvalue = 16.654
  Group = -> [Ta_element001]
  conduct = 2
  density = 1
  expand = 3
  formula = Ta
  name = G4_Ta
  specific = 4
FEATURE [App::DocumentObjectGroupPython] W_element004  label="W_element : 004"  # scripted group (container) (typed FeaturePython)
  n = 1
  ref = W_element
FEATURE [App::DocumentObjectGroupPython] G4_W  # scripted group (container) (typed FeaturePython)
  Dunit = g/cm3
  Dvalue = 19.3
  Group = -> [W_element004]
  conduct = 2
  density = 1
  expand = 3
  formula = W
  name = G4_W
  specific = 4
FEATURE [App::DocumentObjectGroupPython] Re_element001  label="Re_element : 1"  # scripted group (container) (typed FeaturePython)
  n = 1
  ref = Re_element
FEATURE [App::DocumentObjectGroupPython] G4_Re  # scripted group (container) (typed FeaturePython)
  Dunit = g/cm3
  Dvalue = 21.02
  Group = -> [Re_element001]
  conduct = 2
  density = 1
  expand = 3
  formula = Re
  name = G4_Re
  specific = 4
FEATURE [App::DocumentObjectGroupPython] Os_element001  label="Os_element : 1"  # scripted group (container) (typed FeaturePython)
  n = 1
  ref = Os_element
FEATURE [App::DocumentObjectGroupPython] G4_Os  # scripted group (container) (typed FeaturePython)
  Dunit = g/cm3
  Dvalue = 22.57
  Group = -> [Os_element001]
  conduct = 2
  density = 1
  expand = 3
  formula = Os
  name = G4_Os
  specific = 4
FEATURE [App::DocumentObjectGroupPython] Ir_element001  label="Ir_element : 1"  # scripted group (container) (typed FeaturePython)
  n = 1
  ref = Ir_element
FEATURE [App::DocumentObjectGroupPython] G4_Ir  # scripted group (container) (typed FeaturePython)
  Dunit = g/cm3
  Dvalue = 22.42
  Group = -> [Ir_element001]
  conduct = 2
  density = 1
  expand = 3
  formula = Ir
  name = G4_Ir
  specific = 4
FEATURE [App::DocumentObjectGroupPython] Pt_element001  label="Pt_element : 1"  # scripted group (container) (typed FeaturePython)
  n = 1
  ref = Pt_element
FEATURE [App::DocumentObjectGroupPython] G4_Pt  # scripted group (container) (typed FeaturePython)
  Dunit = g/cm3
  Dvalue = 21.45
  Group = -> [Pt_element001]
  conduct = 2
  density = 1
  expand = 3
  formula = Pt
  name = G4_Pt
  specific = 4
FEATURE [App::DocumentObjectGroupPython] Au_element001  label="Au_element : 1"  # scripted group (container) (typed FeaturePython)
  n = 1
  ref = Au_element
FEATURE [App::DocumentObjectGroupPython] G4_Au  # scripted group (container) (typed FeaturePython)
  Dunit = g/cm3
  Dvalue = 19.32
  Group = -> [Au_element001]
  conduct = 2
  density = 1
  expand = 3
  formula = Au
  name = G4_Au
  specific = 4
FEATURE [App::DocumentObjectGroupPython] Hg_element002  label="Hg_element : 002"  # scripted group (container) (typed FeaturePython)
  n = 1
  ref = Hg_element
FEATURE [App::DocumentObjectGroupPython] G4_Hg  # scripted group (container) (typed FeaturePython)
  Dunit = g/cm3
  Dvalue = 13.546
  Group = -> [Hg_element002]
  conduct = 2
  density = 1
  expand = 3
  formula = Hg
  name = G4_Hg
  specific = 4
FEATURE [App::DocumentObjectGroupPython] Tl_element002  label="Tl_element : 002"  # scripted group (container) (typed FeaturePython)
  n = 1
  ref = Tl_element
FEATURE [App::DocumentObjectGroupPython] G4_Tl  # scripted group (container) (typed FeaturePython)
  Dunit = g/cm3
  Dvalue = 11.72
  Group = -> [Tl_element002]
  conduct = 2
  density = 1
  expand = 3
  formula = Tl
  name = G4_Tl
  specific = 4
FEATURE [App::DocumentObjectGroupPython] Pb_element003  label="Pb_element : 1"  # scripted group (container) (typed FeaturePython)
  n = 1
  ref = Pb_element
FEATURE [App::DocumentObjectGroupPython] G4_Pb  # scripted group (container) (typed FeaturePython)
  Dunit = g/cm3
  Dvalue = 11.35
  Group = -> [Pb_element003]
  conduct = 2
  density = 1
  expand = 3
  formula = Pb
  name = G4_Pb
  specific = 4
FEATURE [App::DocumentObjectGroupPython] Bi_element002  label="Bi_element : 1"  # scripted group (container) (typed FeaturePython)
  n = 1
  ref = Bi_element
FEATURE [App::DocumentObjectGroupPython] G4_Bi  # scripted group (container) (typed FeaturePython)
  Dunit = g/cm3
  Dvalue = 9.747
  Group = -> [Bi_element002]
  conduct = 2
  density = 1
  expand = 3
  formula = Bi
  name = G4_Bi
  specific = 4
FEATURE [App::DocumentObjectGroupPython] Po_element001  label="Po_element : 1"  # scripted group (container) (typed FeaturePython)
  n = 1
  ref = Po_element
FEATURE [App::DocumentObjectGroupPython] G4_Po  # scripted group (container) (typed FeaturePython)
  Dunit = g/cm3
  Dvalue = 9.32
  Group = -> [Po_element001]
  conduct = 2
  density = 1
  expand = 3
  formula = Po
  name = G4_Po
  specific = 4
FEATURE [App::DocumentObjectGroupPython] At_element001  label="At_element : 1"  # scripted group (container) (typed FeaturePython)
  n = 1
  ref = At_element
FEATURE [App::DocumentObjectGroupPython] G4_At  # scripted group (container) (typed FeaturePython)
  Dunit = g/cm3
  Dvalue = 9.32
  Group = -> [At_element001]
  conduct = 2
  density = 1
  expand = 3
  formula = At
  name = G4_At
  specific = 4
FEATURE [App::DocumentObjectGroupPython] Rn_element001  label="Rn_element : 1"  # scripted group (container) (typed FeaturePython)
  n = 1
  ref = Rn_element
FEATURE [App::DocumentObjectGroupPython] G4_Rn  # scripted group (container) (typed FeaturePython)
  Dunit = g/cm3
  Dvalue = 0.00900662
  Group = -> [Rn_element001]
  conduct = 2
  density = 1
  expand = 3
  formula = Rn
  name = G4_Rn
  specific = 4
FEATURE [App::DocumentObjectGroupPython] Fr_element001  label="Fr_element : 1"  # scripted group (container) (typed FeaturePython)
  n = 1
  ref = Fr_element
FEATURE [App::DocumentObjectGroupPython] G4_Fr  # scripted group (container) (typed FeaturePython)
  Dunit = g/cm3
  Dvalue = 1
  Group = -> [Fr_element001]
  conduct = 2
  density = 1
  expand = 3
  formula = Fr
  name = G4_Fr
  specific = 4
FEATURE [App::DocumentObjectGroupPython] Ra_element001  label="Ra_element : 1"  # scripted group (container) (typed FeaturePython)
  n = 1
  ref = Ra_element
FEATURE [App::DocumentObjectGroupPython] G4_Ra  # scripted group (container) (typed FeaturePython)
  Dunit = g/cm3
  Dvalue = 5
  Group = -> [Ra_element001]
  conduct = 2
  density = 1
  expand = 3
  formula = Ra
  name = G4_Ra
  specific = 4
FEATURE [App::DocumentObjectGroupPython] Ac_element001  label="Ac_element : 1"  # scripted group (container) (typed FeaturePython)
  n = 1
  ref = Ac_element
FEATURE [App::DocumentObjectGroupPython] G4_Ac  # scripted group (container) (typed FeaturePython)
  Dunit = g/cm3
  Dvalue = 10.07
  Group = -> [Ac_element001]
  conduct = 2
  density = 1
  expand = 3
  formula = Ac
  name = G4_Ac
  specific = 4
FEATURE [App::DocumentObjectGroupPython] Th_element001  label="Th_element : 1"  # scripted group (container) (typed FeaturePython)
  n = 1
  ref = Th_element
FEATURE [App::DocumentObjectGroupPython] G4_Th  # scripted group (container) (typed FeaturePython)
  Dunit = g/cm3
  Dvalue = 11.72
  Group = -> [Th_element001]
  conduct = 2
  density = 1
  expand = 3
  formula = Th
  name = G4_Th
  specific = 4
FEATURE [App::DocumentObjectGroupPython] Pa_element001  label="Pa_element : 1"  # scripted group (container) (typed FeaturePython)
  n = 1
  ref = Pa_element
FEATURE [App::DocumentObjectGroupPython] G4_Pa  # scripted group (container) (typed FeaturePython)
  Dunit = g/cm3
  Dvalue = 15.37
  Group = -> [Pa_element001]
  conduct = 2
  density = 1
  expand = 3
  formula = Pa
  name = G4_Pa
  specific = 4
FEATURE [App::DocumentObjectGroupPython] U_element004  label="U_element : 004"  # scripted group (container) (typed FeaturePython)
  n = 1
  ref = U_element
FEATURE [App::DocumentObjectGroupPython] G4_U  # scripted group (container) (typed FeaturePython)
  Dunit = g/cm3
  Dvalue = 18.95
  Group = -> [U_element004]
  conduct = 2
  density = 1
  expand = 3
  formula = U
  name = G4_U
  specific = 4
FEATURE [App::DocumentObjectGroupPython] Np_element001  label="Np_element : 1"  # scripted group (container) (typed FeaturePython)
  n = 1
  ref = Np_element
FEATURE [App::DocumentObjectGroupPython] G4_Np  # scripted group (container) (typed FeaturePython)
  Dunit = g/cm3
  Dvalue = 20.25
  Group = -> [Np_element001]
  conduct = 2
  density = 1
  expand = 3
  formula = Np
  name = G4_Np
  specific = 4
FEATURE [App::DocumentObjectGroupPython] Pu_element002  label="Pu_element : 002"  # scripted group (container) (typed FeaturePython)
  n = 1
  ref = Pu_element
FEATURE [App::DocumentObjectGroupPython] G4_Pu  # scripted group (container) (typed FeaturePython)
  Dunit = g/cm3
  Dvalue = 19.84
  Group = -> [Pu_element002]
  conduct = 2
  density = 1
  expand = 3
  formula = Pu
  name = G4_Pu
  specific = 4
FEATURE [App::DocumentObjectGroupPython] Am_element001  label="Am_element : 1"  # scripted group (container) (typed FeaturePython)
  n = 1
  ref = Am_element
FEATURE [App::DocumentObjectGroupPython] G4_Am  # scripted group (container) (typed FeaturePython)
  Dunit = g/cm3
  Dvalue = 13.67
  Group = -> [Am_element001]
  conduct = 2
  density = 1
  expand = 3
  formula = Am
  name = G4_Am
  specific = 4
FEATURE [App::DocumentObjectGroupPython] Cm_element001  label="Cm_element : 1"  # scripted group (container) (typed FeaturePython)
  n = 1
  ref = Cm_element
FEATURE [App::DocumentObjectGroupPython] G4_Cm  # scripted group (container) (typed FeaturePython)
  Dunit = g/cm3
  Dvalue = 13.51
  Group = -> [Cm_element001]
  conduct = 2
  density = 1
  expand = 3
  formula = Cm
  name = G4_Cm
  specific = 4
FEATURE [App::DocumentObjectGroupPython] Bk_element001  label="Bk_element : 1"  # scripted group (container) (typed FeaturePython)
  n = 1
  ref = Bk_element
FEATURE [App::DocumentObjectGroupPython] G4_Bk  # scripted group (container) (typed FeaturePython)
  Dunit = g/cm3
  Dvalue = 14
  Group = -> [Bk_element001]
  conduct = 2
  density = 1
  expand = 3
  formula = Bk
  name = G4_Bk
  specific = 4
FEATURE [App::DocumentObjectGroupPython] Cf_element001  label="Cf_element : 1"  # scripted group (container) (typed FeaturePython)
  n = 1
  ref = Cf_element
FEATURE [App::DocumentObjectGroupPython] G4_Cf  # scripted group (container) (typed FeaturePython)
  Dunit = g/cm3
  Dvalue = 10
  Group = -> [Cf_element001]
  conduct = 2
  density = 1
  expand = 3
  formula = Cf
  name = G4_Cf
  specific = 4
FEATURE [App::DocumentObjectGroupPython] Element  # scripted group (container) (typed FeaturePython)
  Group = -> [G4_H,G4_He,G4_Li,G4_Be,G4_B,G4_C,G4_N,G4_O,G4_F,G4_Ne,G4_Na,G4_Mg,G4_Al,G4_Si,G4_P,G4_S,G4_Cl,G4_Ar,G4_K,G4_Ca,G4_Sc,G4_Ti,G4_V,G4_Cr,G4_Mn,G4_Fe,G4_Co,G4_Ni,G4_Cu,G4_Zn,G4_Ga,G4_Ge,G4_As,G4_Se,G4_Br,G4_Kr,G4_Rb,G4_Sr,G4_Y,G4_Zr,G4_Nb,G4_Mo,G4_Tc,G4_Ru,G4_Rh,G4_Pd,G4_Ag,G4_Cd,G4_In,G4_Sn,G4_Sb,G4_Te,G4_I,G4_Xe,G4_Cs,G4_Ba,G4_La,G4_Ce,G4_Pr,G4_Nd,G4_Pm,G4_Sm,G4_Eu,G4_Gd,G4_Tb,G4_Dy,G4_Ho,G4_Er,+30 more]
FEATURE [App::DocumentObjectGroupPython] H_element114  label="H_element : 063"  # scripted group (container) (typed FeaturePython)
  n = 2
  ref = H_element
FEATURE [App::DocumentObjectGroupPython] G4_lH2  # scripted group (container) (typed FeaturePython)
  Dunit = g/cm3
  Dvalue = 0.0708
  Group = -> [H_element114]
  conduct = 2
  density = 1
  expand = 3
  formula = G4_lH2
  name = G4_lH2
  specific = 4
FEATURE [App::DocumentObjectGroupPython] N_element049  label="N_element : 022"  # scripted group (container) (typed FeaturePython)
  n = 2
  ref = N_element
FEATURE [App::DocumentObjectGroupPython] G4_lN2  # scripted group (container) (typed FeaturePython)
  Dunit = g/cm3
  Dvalue = 0.807
  Group = -> [N_element049]
  conduct = 2
  density = 1
  expand = 3
  formula = G4_lN2
  name = G4_lN2
  specific = 4
FEATURE [App::DocumentObjectGroupPython] O_element106  label="O_element : 060"  # scripted group (container) (typed FeaturePython)
  n = 2
  ref = O_element
FEATURE [App::DocumentObjectGroupPython] G4_lO2  # scripted group (container) (typed FeaturePython)
  Dunit = g/cm3
  Dvalue = 1.141
  Group = -> [O_element106]
  conduct = 2
  density = 1
  expand = 3
  formula = G4_lO2
  name = G4_lO2
  specific = 4
FEATURE [App::DocumentObjectGroupPython] Ar  label="Ar : 1"  # scripted group (container) (typed FeaturePython)
  n = 1
  ref = Ar
FEATURE [App::DocumentObjectGroupPython] G4_lAr  # scripted group (container) (typed FeaturePython)
  Dunit = g/cm3
  Dvalue = 1.396
  Group = -> [Ar]
  conduct = 2
  density = 1
  expand = 3
  formula = G4_lAr
  name = G4_lAr
  specific = 4
FEATURE [App::DocumentObjectGroupPython] Br  label="Br : 1"  # scripted group (container) (typed FeaturePython)
  n = 1
  ref = Br
FEATURE [App::DocumentObjectGroupPython] G4_lBr  # scripted group (container) (typed FeaturePython)
  Dunit = g/cm3
  Dvalue = 3.1028
  Group = -> [Br]
  conduct = 2
  density = 1
  expand = 3
  formula = G4_lBr
  name = G4_lBr
  specific = 4
FEATURE [App::DocumentObjectGroupPython] Kr  label="Kr : 1"  # scripted group (container) (typed FeaturePython)
  n = 1
  ref = Kr
FEATURE [App::DocumentObjectGroupPython] G4_lKr  # scripted group (container) (typed FeaturePython)
  Dunit = g/cm3
  Dvalue = 2.418
  Group = -> [Kr]
  conduct = 2
  density = 1
  expand = 3
  formula = G4_lKr
  name = G4_lKr
  specific = 4
FEATURE [App::DocumentObjectGroupPython] Xe  label="Xe : 1"  # scripted group (container) (typed FeaturePython)
  n = 1
  ref = Xe
FEATURE [App::DocumentObjectGroupPython] G4_lXe  # scripted group (container) (typed FeaturePython)
  Dunit = g/cm3
  Dvalue = 2.953
  Group = -> [Xe]
  conduct = 2
  density = 1
  expand = 3
  formula = G4_lXe
  name = G4_lXe
  specific = 4
FEATURE [App::DocumentObjectGroupPython] O_element107  label="O_element : 061"  # scripted group (container) (typed FeaturePython)
  n = 4
  ref = O_element
FEATURE [App::DocumentObjectGroupPython] Pb_element004  label="Pb_element : 002"  # scripted group (container) (typed FeaturePython)
  n = 1
  ref = Pb_element
FEATURE [App::DocumentObjectGroupPython] W_element005  label="W_element : 005"  # scripted group (container) (typed FeaturePython)
  n = 1
  ref = W_element
FEATURE [App::DocumentObjectGroupPython] G4_PbWO4  # scripted group (container) (typed FeaturePython)
  Dunit = g/cm3
  Dvalue = 8.28
  Group = -> [O_element107,Pb_element004,W_element005]
  conduct = 2
  density = 1
  expand = 3
  formula = G4_PbWO4
  name = G4_PbWO4
  specific = 4
FEATURE [App::DocumentObjectGroupPython] alactic  label="alactic : 1"  # scripted group (container) (typed FeaturePython)
  n = 1
  ref = alactic
FEATURE [App::DocumentObjectGroupPython] G4_Galactic  # scripted group (container) (typed FeaturePython)
  Dunit = g/cm3
  Dvalue = 0
  Group = -> [alactic]
  conduct = 2
  density = 1
  expand = 3
  formula = G4_Galactic
  name = G4_Galactic
  specific = 4
FEATURE [App::DocumentObjectGroupPython] RAPHITE_POROUS  label="RAPHITE_POROUS : 1"  # scripted group (container) (typed FeaturePython)
  n = 1
  ref = RAPHITE_POROUS
FEATURE [App::DocumentObjectGroupPython] G4_GRAPHITE_POROUS  # scripted group (container) (typed FeaturePython)
  Dunit = g/cm3
  Dvalue = 1.7
  Group = -> [RAPHITE_POROUS]
  conduct = 2
  density = 1
  expand = 3
  formula = G4_GRAPHITE_POROUS
  name = G4_GRAPHITE_POROUS
  specific = 4
FEATURE [App::DocumentObjectGroupPython] H_element115  label="H_element : 0.150"  # scripted group (container) (typed FeaturePython)
  n = 0.080538
FEATURE [App::DocumentObjectGroupPython] C_element125  label="C_element : 0.600"  # scripted group (container) (typed FeaturePython)
  n = 0.599848
FEATURE [App::DocumentObjectGroupPython] O_element108  label="O_element : 0.320"  # scripted group (container) (typed FeaturePython)
  n = 0.319614
FEATURE [App::DocumentObjectGroupPython] G4_LUCITE  # scripted group (container) (typed FeaturePython)
  Dunit = g/cm3
  Dvalue = 1.19
  Group = -> [H_element115,C_element125,O_element108]
  conduct = 2
  density = 1
  expand = 3
  formula = G4_LUCITE
  name = G4_LUCITE
  specific = 4
FEATURE [App::DocumentObjectGroupPython] Cu_element002  label="Cu_element : 62"  # scripted group (container) (typed FeaturePython)
  n = 62
  ref = Cu_element
FEATURE [App::DocumentObjectGroupPython] Zn_element002  label="Zn_element : 35"  # scripted group (container) (typed FeaturePython)
  n = 35
  ref = Zn_element
FEATURE [App::DocumentObjectGroupPython] Pb_element005  label="Pb_element : 3"  # scripted group (container) (typed FeaturePython)
  n = 3
  ref = Pb_element
FEATURE [App::DocumentObjectGroupPython] G4_BRASS  # scripted group (container) (typed FeaturePython)
  Dunit = g/cm3
  Dvalue = 8.52
  Group = -> [Cu_element002,Zn_element002,Pb_element005]
  conduct = 2
  density = 1
  expand = 3
  formula = G4_BRASS
  name = G4_BRASS
  specific = 4
FEATURE [App::DocumentObjectGroupPython] Cu_element003  label="Cu_element : 89"  # scripted group (container) (typed FeaturePython)
  n = 89
  ref = Cu_element
FEATURE [App::DocumentObjectGroupPython] Zn_element003  label="Zn_element : 9"  # scripted group (container) (typed FeaturePython)
  n = 9
  ref = Zn_element
FEATURE [App::DocumentObjectGroupPython] Pb_element006  label="Pb_element : 2"  # scripted group (container) (typed FeaturePython)
  n = 2
  ref = Pb_element
FEATURE [App::DocumentObjectGroupPython] G4_BRONZE  # scripted group (container) (typed FeaturePython)
  Dunit = g/cm3
  Dvalue = 8.82
  Group = -> [Cu_element003,Zn_element003,Pb_element006]
  conduct = 2
  density = 1
  expand = 3
  formula = G4_BRONZE
  name = G4_BRONZE
  specific = 4
FEATURE [App::DocumentObjectGroupPython] Fe_element008  label="Fe_element : 74"  # scripted group (container) (typed FeaturePython)
  n = 74
  ref = Fe_element
FEATURE [App::DocumentObjectGroupPython] Cr_element002  label="Cr_element : 18"  # scripted group (container) (typed FeaturePython)
  n = 18
  ref = Cr_element
FEATURE [App::DocumentObjectGroupPython] Ni_element002  label="Ni_element : 8"  # scripted group (container) (typed FeaturePython)
  n = 8
  ref = Ni_element
FEATURE [App::DocumentObjectGroupPython] G4_STAINLESS_STEEL  label="G4_STAINLESS-STEEL"  # scripted group (container) (typed FeaturePython)
  Dunit = g/cm3
  Dvalue = 8
  Group = -> [Fe_element008,Cr_element002,Ni_element002]
  conduct = 2
  density = 1
  expand = 3
  formula = G4_STAINLESS-STEEL
  name = G4_STAINLESS-STEEL
  specific = 4
FEATURE [App::DocumentObjectGroupPython] H_element116  label="H_element : 064"  # scripted group (container) (typed FeaturePython)
  n = 18
  ref = H_element
FEATURE [App::DocumentObjectGroupPython] C_element126  label="C_element : 071"  # scripted group (container) (typed FeaturePython)
  n = 12
  ref = C_element
FEATURE [App::DocumentObjectGroupPython] O_element109  label="O_element : 062"  # scripted group (container) (typed FeaturePython)
  n = 7
  ref = O_element
FEATURE [App::DocumentObjectGroupPython] G4_CR39  # scripted group (container) (typed FeaturePython)
  Dunit = g/cm3
  Dvalue = 1.32
  Group = -> [H_element116,C_element126,O_element109]
  conduct = 2
  density = 1
  expand = 3
  formula = G4_CR39
  name = G4_CR39
  specific = 4
FEATURE [App::DocumentObjectGroupPython] H_element117  label="H_element : 38"  # scripted group (container) (typed FeaturePython)
  n = 38
  ref = H_element
FEATURE [App::DocumentObjectGroupPython] C_element127  label="C_element : 072"  # scripted group (container) (typed FeaturePython)
  n = 18
  ref = C_element
FEATURE [App::DocumentObjectGroupPython] O_element110  label="O_element : 063"  # scripted group (container) (typed FeaturePython)
  n = 1
  ref = O_element
FEATURE [App::DocumentObjectGroupPython] G4_OCTADECANOL  # scripted group (container) (typed FeaturePython)
  Dunit = g/cm3
  Dvalue = 0.812
  Group = -> [H_element117,C_element127,O_element110]
  conduct = 2
  density = 1
  expand = 3
  formula = G4_OCTADECANOL
  name = G4_OCTADECANOL
  specific = 4
FEATURE [App::DocumentObjectGroupPython] HEP  # scripted group (container) (typed FeaturePython)
  Group = -> [G4_lH2,G4_lN2,G4_lO2,G4_lAr,G4_lBr,G4_lKr,G4_lXe,G4_PbWO4,G4_Galactic,G4_GRAPHITE_POROUS,G4_LUCITE,G4_BRASS,G4_BRONZE,G4_STAINLESS_STEEL,G4_CR39,G4_OCTADECANOL]
FEATURE [App::DocumentObjectGroupPython] C_element128  label="C_element : 073"  # scripted group (container) (typed FeaturePython)
  n = 14
  ref = C_element
FEATURE [App::DocumentObjectGroupPython] H_element118  label="H_element : 065"  # scripted group (container) (typed FeaturePython)
  n = 10
  ref = H_element
FEATURE [App::DocumentObjectGroupPython] O_element111  label="O_element : 064"  # scripted group (container) (typed FeaturePython)
  n = 2
  ref = O_element
FEATURE [App::DocumentObjectGroupPython] N_element050  label="N_element : 023"  # scripted group (container) (typed FeaturePython)
  n = 2
  ref = N_element
FEATURE [App::DocumentObjectGroupPython] G4_KEVLAR  # scripted group (container) (typed FeaturePython)
  Dunit = g/cm3
  Dvalue = 1.44
  Group = -> [C_element128,H_element118,O_element111,N_element050]
  conduct = 2
  density = 1
  expand = 3
  formula = G4_KEVLAR
  name = G4_KEVLAR
  specific = 4
FEATURE [App::DocumentObjectGroupPython] C_element129  label="C_element : 074"  # scripted group (container) (typed FeaturePython)
  n = 10
  ref = C_element
FEATURE [App::DocumentObjectGroupPython] H_element119  label="H_element : 066"  # scripted group (container) (typed FeaturePython)
  n = 8
  ref = H_element
FEATURE [App::DocumentObjectGroupPython] O_element112  label="O_element : 065"  # scripted group (container) (typed FeaturePython)
  n = 4
  ref = O_element
FEATURE [App::DocumentObjectGroupPython] G4_DACRON  # scripted group (container) (typed FeaturePython)
  Dunit = g/cm3
  Dvalue = 1.4
  Group = -> [C_element129,H_element119,O_element112]
  conduct = 2
  density = 1
  expand = 3
  formula = G4_DACRON
  name = G4_DACRON
  specific = 4
FEATURE [App::DocumentObjectGroupPython] C_element130  label="C_element : 075"  # scripted group (container) (typed FeaturePython)
  n = 4
  ref = C_element
FEATURE [App::DocumentObjectGroupPython] H_element120  label="H_element : 067"  # scripted group (container) (typed FeaturePython)
  n = 5
  ref = H_element
FEATURE [App::DocumentObjectGroupPython] Cl_element030  label="Cl_element : 016"  # scripted group (container) (typed FeaturePython)
  n = 1
  ref = Cl_element
FEATURE [App::DocumentObjectGroupPython] G4_NEOPRENE  # scripted group (container) (typed FeaturePython)
  Dunit = g/cm3
  Dvalue = 1.23
  Group = -> [C_element130,H_element120,Cl_element030]
  conduct = 2
  density = 1
  expand = 3
  formula = G4_NEOPRENE
  name = G4_NEOPRENE
  specific = 4
FEATURE [App::DocumentObjectGroupPython] Space  # scripted group (container) (typed FeaturePython)
  Group = -> [G4_KEVLAR,G4_DACRON,G4_NEOPRENE]
FEATURE [App::DocumentObjectGroupPython] H_element121  label="H_element : 068"  # scripted group (container) (typed FeaturePython)
  n = 5
  ref = H_element
FEATURE [App::DocumentObjectGroupPython] C_element131  label="C_element : 076"  # scripted group (container) (typed FeaturePython)
  n = 4
  ref = C_element
FEATURE [App::DocumentObjectGroupPython] N_element051  label="N_element : 3"  # scripted group (container) (typed FeaturePython)
  n = 3
  ref = N_element
FEATURE [App::DocumentObjectGroupPython] O_element113  label="O_element : 066"  # scripted group (container) (typed FeaturePython)
  n = 1
  ref = O_element
FEATURE [App::DocumentObjectGroupPython] G4_CYTOSINE  # scripted group (container) (typed FeaturePython)
  Dunit = g/cm3
  Dvalue = 1.55
  Group = -> [H_element121,C_element131,N_element051,O_element113]
  conduct = 2
  density = 1
  expand = 3
  formula = G4_CYTOSINE
  name = G4_CYTOSINE
  specific = 4
FEATURE [App::DocumentObjectGroupPython] H_element122  label="H_element : 069"  # scripted group (container) (typed FeaturePython)
  n = 6
  ref = H_element
FEATURE [App::DocumentObjectGroupPython] C_element132  label="C_element : 077"  # scripted group (container) (typed FeaturePython)
  n = 5
  ref = C_element
FEATURE [App::DocumentObjectGroupPython] N_element052  label="N_element : 024"  # scripted group (container) (typed FeaturePython)
  n = 2
  ref = N_element
FEATURE [App::DocumentObjectGroupPython] O_element114  label="O_element : 067"  # scripted group (container) (typed FeaturePython)
  n = 2
  ref = O_element
FEATURE [App::DocumentObjectGroupPython] G4_THYMINE  # scripted group (container) (typed FeaturePython)
  Dunit = g/cm3
  Dvalue = 1.23
  Group = -> [H_element122,C_element132,N_element052,O_element114]
  conduct = 2
  density = 1
  expand = 3
  formula = G4_THYMINE
  name = G4_THYMINE
  specific = 4
FEATURE [App::DocumentObjectGroupPython] H_element123  label="H_element : 070"  # scripted group (container) (typed FeaturePython)
  n = 4
  ref = H_element
FEATURE [App::DocumentObjectGroupPython] C_element133  label="C_element : 078"  # scripted group (container) (typed FeaturePython)
  n = 4
  ref = C_element
FEATURE [App::DocumentObjectGroupPython] N_element053  label="N_element : 025"  # scripted group (container) (typed FeaturePython)
  n = 2
  ref = N_element
FEATURE [App::DocumentObjectGroupPython] O_element115  label="O_element : 068"  # scripted group (container) (typed FeaturePython)
  n = 2
  ref = O_element
FEATURE [App::DocumentObjectGroupPython] G4_URACIL  # scripted group (container) (typed FeaturePython)
  Dunit = g/cm3
  Dvalue = 1.32
  Group = -> [H_element123,C_element133,N_element053,O_element115]
  conduct = 2
  density = 1
  expand = 3
  formula = G4_URACIL
  name = G4_URACIL
  specific = 4
FEATURE [App::DocumentObjectGroupPython] H_element124  label="H_element : 071"  # scripted group (container) (typed FeaturePython)
  n = 4
  ref = H_element
FEATURE [App::DocumentObjectGroupPython] C_element134  label="C_element : 079"  # scripted group (container) (typed FeaturePython)
  n = 5
  ref = C_element
FEATURE [App::DocumentObjectGroupPython] N_element054  label="N_element : 026"  # scripted group (container) (typed FeaturePython)
  n = 5
  ref = N_element
FEATURE [App::DocumentObjectGroupPython] G4_DNA_ADENINE  # scripted group (container) (typed FeaturePython)
  Dunit = g/cm3
  Dvalue = 1
  Group = -> [H_element124,C_element134,N_element054]
  conduct = 2
  density = 1
  expand = 3
  formula = G4_DNA_ADENINE
  name = G4_DNA_ADENINE
  specific = 4
FEATURE [App::DocumentObjectGroupPython] H_element125  label="H_element : 072"  # scripted group (container) (typed FeaturePython)
  n = 4
  ref = H_element
FEATURE [App::DocumentObjectGroupPython] C_element135  label="C_element : 080"  # scripted group (container) (typed FeaturePython)
  n = 5
  ref = C_element
FEATURE [App::DocumentObjectGroupPython] N_element055  label="N_element : 027"  # scripted group (container) (typed FeaturePython)
  n = 5
  ref = N_element
FEATURE [App::DocumentObjectGroupPython] O_element116  label="O_element : 069"  # scripted group (container) (typed FeaturePython)
  n = 1
  ref = O_element
FEATURE [App::DocumentObjectGroupPython] G4_DNA_GUANINE  # scripted group (container) (typed FeaturePython)
  Dunit = g/cm3
  Dvalue = 1
  Group = -> [H_element125,C_element135,N_element055,O_element116]
  conduct = 2
  density = 1
  expand = 3
  formula = G4_DNA_GUANINE
  name = G4_DNA_GUANINE
  specific = 4
FEATURE [App::DocumentObjectGroupPython] H_element126  label="H_element : 073"  # scripted group (container) (typed FeaturePython)
  n = 4
  ref = H_element
FEATURE [App::DocumentObjectGroupPython] C_element136  label="C_element : 081"  # scripted group (container) (typed FeaturePython)
  n = 4
  ref = C_element
FEATURE [App::DocumentObjectGroupPython] N_element056  label="N_element : 028"  # scripted group (container) (typed FeaturePython)
  n = 3
  ref = N_element
FEATURE [App::DocumentObjectGroupPython] O_element117  label="O_element : 070"  # scripted group (container) (typed FeaturePython)
  n = 1
  ref = O_element
FEATURE [App::DocumentObjectGroupPython] G4_DNA_CYTOSINE  # scripted group (container) (typed FeaturePython)
  Dunit = g/cm3
  Dvalue = 1
  Group = -> [H_element126,C_element136,N_element056,O_element117]
  conduct = 2
  density = 1
  expand = 3
  formula = G4_DNA_CYTOSINE
  name = G4_DNA_CYTOSINE
  specific = 4
FEATURE [App::DocumentObjectGroupPython] H_element127  label="H_element : 074"  # scripted group (container) (typed FeaturePython)
  n = 5
  ref = H_element
FEATURE [App::DocumentObjectGroupPython] C_element137  label="C_element : 082"  # scripted group (container) (typed FeaturePython)
  n = 5
  ref = C_element
FEATURE [App::DocumentObjectGroupPython] N_element057  label="N_element : 029"  # scripted group (container) (typed FeaturePython)
  n = 2
  ref = N_element
FEATURE [App::DocumentObjectGroupPython] O_element118  label="O_element : 071"  # scripted group (container) (typed FeaturePython)
  n = 2
  ref = O_element
FEATURE [App::DocumentObjectGroupPython] G4_DNA_THYMINE  # scripted group (container) (typed FeaturePython)
  Dunit = g/cm3
  Dvalue = 1
  Group = -> [H_element127,C_element137,N_element057,O_element118]
  conduct = 2
  density = 1
  expand = 3
  formula = G4_DNA_THYMINE
  name = G4_DNA_THYMINE
  specific = 4
FEATURE [App::DocumentObjectGroupPython] H_element128  label="H_element : 075"  # scripted group (container) (typed FeaturePython)
  n = 3
  ref = H_element
FEATURE [App::DocumentObjectGroupPython] C_element138  label="C_element : 083"  # scripted group (container) (typed FeaturePython)
  n = 4
  ref = C_element
FEATURE [App::DocumentObjectGroupPython] N_element058  label="N_element : 030"  # scripted group (container) (typed FeaturePython)
  n = 2
  ref = N_element
FEATURE [App::DocumentObjectGroupPython] O_element119  label="O_element : 072"  # scripted group (container) (typed FeaturePython)
  n = 2
  ref = O_element
FEATURE [App::DocumentObjectGroupPython] G4_DNA_URACIL  # scripted group (container) (typed FeaturePython)
  Dunit = g/cm3
  Dvalue = 1
  Group = -> [H_element128,C_element138,N_element058,O_element119]
  conduct = 2
  density = 1
  expand = 3
  formula = G4_DNA_URACIL
  name = G4_DNA_URACIL
  specific = 4
FEATURE [App::DocumentObjectGroupPython] H_element129  label="H_element : 076"  # scripted group (container) (typed FeaturePython)
  n = 10
  ref = H_element
FEATURE [App::DocumentObjectGroupPython] C_element139  label="C_element : 084"  # scripted group (container) (typed FeaturePython)
  n = 10
  ref = C_element
FEATURE [App::DocumentObjectGroupPython] N_element059  label="N_element : 031"  # scripted group (container) (typed FeaturePython)
  n = 5
  ref = N_element
FEATURE [App::DocumentObjectGroupPython] O_element120  label="O_element : 073"  # scripted group (container) (typed FeaturePython)
  n = 4
  ref = O_element
FEATURE [App::DocumentObjectGroupPython] G4_DNA_ADENOSINE  # scripted group (container) (typed FeaturePython)
  Dunit = g/cm3
  Dvalue = 1
  Group = -> [H_element129,C_element139,N_element059,O_element120]
  conduct = 2
  density = 1
  expand = 3
  formula = G4_DNA_ADENOSINE
  name = G4_DNA_ADENOSINE
  specific = 4
FEATURE [App::DocumentObjectGroupPython] H_element130  label="H_element : 077"  # scripted group (container) (typed FeaturePython)
  n = 10
  ref = H_element
FEATURE [App::DocumentObjectGroupPython] C_element140  label="C_element : 085"  # scripted group (container) (typed FeaturePython)
  n = 10
  ref = C_element
FEATURE [App::DocumentObjectGroupPython] N_element060  label="N_element : 032"  # scripted group (container) (typed FeaturePython)
  n = 5
  ref = N_element
FEATURE [App::DocumentObjectGroupPython] O_element121  label="O_element : 074"  # scripted group (container) (typed FeaturePython)
  n = 5
  ref = O_element
FEATURE [App::DocumentObjectGroupPython] G4_DNA_GUANOSINE  # scripted group (container) (typed FeaturePython)
  Dunit = g/cm3
  Dvalue = 1
  Group = -> [H_element130,C_element140,N_element060,O_element121]
  conduct = 2
  density = 1
  expand = 3
  formula = G4_DNA_GUANOSINE
  name = G4_DNA_GUANOSINE
  specific = 4
FEATURE [App::DocumentObjectGroupPython] H_element131  label="H_element : 078"  # scripted group (container) (typed FeaturePython)
  n = 10
  ref = H_element
FEATURE [App::DocumentObjectGroupPython] C_element141  label="C_element : 086"  # scripted group (container) (typed FeaturePython)
  n = 9
  ref = C_element
FEATURE [App::DocumentObjectGroupPython] N_element061  label="N_element : 033"  # scripted group (container) (typed FeaturePython)
  n = 3
  ref = N_element
FEATURE [App::DocumentObjectGroupPython] O_element122  label="O_element : 075"  # scripted group (container) (typed FeaturePython)
  n = 5
  ref = O_element
FEATURE [App::DocumentObjectGroupPython] G4_DNA_CYTIDINE  # scripted group (container) (typed FeaturePython)
  Dunit = g/cm3
  Dvalue = 1
  Group = -> [H_element131,C_element141,N_element061,O_element122]
  conduct = 2
  density = 1
  expand = 3
  formula = G4_DNA_CYTIDINE
  name = G4_DNA_CYTIDINE
  specific = 4
FEATURE [App::DocumentObjectGroupPython] H_element132  label="H_element : 079"  # scripted group (container) (typed FeaturePython)
  n = 9
  ref = H_element
FEATURE [App::DocumentObjectGroupPython] C_element142  label="C_element : 087"  # scripted group (container) (typed FeaturePython)
  n = 9
  ref = C_element
FEATURE [App::DocumentObjectGroupPython] N_element062  label="N_element : 034"  # scripted group (container) (typed FeaturePython)
  n = 2
  ref = N_element
FEATURE [App::DocumentObjectGroupPython] O_element123  label="O_element : 076"  # scripted group (container) (typed FeaturePython)
  n = 6
  ref = O_element
FEATURE [App::DocumentObjectGroupPython] G4_DNA_URIDINE  # scripted group (container) (typed FeaturePython)
  Dunit = g/cm3
  Dvalue = 1
  Group = -> [H_element132,C_element142,N_element062,O_element123]
  conduct = 2
  density = 1
  expand = 3
  formula = G4_DNA_URIDINE
  name = G4_DNA_URIDINE
  specific = 4
FEATURE [App::DocumentObjectGroupPython] H_element133  label="H_element : 080"  # scripted group (container) (typed FeaturePython)
  n = 11
  ref = H_element
FEATURE [App::DocumentObjectGroupPython] C_element143  label="C_element : 088"  # scripted group (container) (typed FeaturePython)
  n = 10
  ref = C_element
FEATURE [App::DocumentObjectGroupPython] N_element063  label="N_element : 035"  # scripted group (container) (typed FeaturePython)
  n = 2
  ref = N_element
FEATURE [App::DocumentObjectGroupPython] O_element124  label="O_element : 077"  # scripted group (container) (typed FeaturePython)
  n = 6
  ref = O_element
FEATURE [App::DocumentObjectGroupPython] G4_DNA_METHYLURIDINE  # scripted group (container) (typed FeaturePython)
  Dunit = g/cm3
  Dvalue = 1
  Group = -> [H_element133,C_element143,N_element063,O_element124]
  conduct = 2
  density = 1
  expand = 3
  formula = G4_DNA_METHYLURIDINE
  name = G4_DNA_METHYLURIDINE
  specific = 4
FEATURE [App::DocumentObjectGroupPython] P_element014  label="P_element : 003"  # scripted group (container) (typed FeaturePython)
  n = 1
  ref = P_element
FEATURE [App::DocumentObjectGroupPython] O_element125  label="O_element : 078"  # scripted group (container) (typed FeaturePython)
  n = 3
  ref = O_element
FEATURE [App::DocumentObjectGroupPython] G4_DNA_MONOPHOSPHATE  # scripted group (container) (typed FeaturePython)
  Dunit = g/cm3
  Dvalue = 1
  Group = -> [P_element014,O_element125]
  conduct = 2
  density = 1
  expand = 3
  formula = G4_DNA_MONOPHOSPHATE
  name = G4_DNA_MONOPHOSPHATE
  specific = 4
FEATURE [App::DocumentObjectGroupPython] H_element134  label="H_element : 081"  # scripted group (container) (typed FeaturePython)
  n = 10
  ref = H_element
FEATURE [App::DocumentObjectGroupPython] C_element144  label="C_element : 089"  # scripted group (container) (typed FeaturePython)
  n = 10
  ref = C_element
FEATURE [App::DocumentObjectGroupPython] N_element064  label="N_element : 036"  # scripted group (container) (typed FeaturePython)
  n = 5
  ref = N_element
FEATURE [App::DocumentObjectGroupPython] O_element126  label="O_element : 079"  # scripted group (container) (typed FeaturePython)
  n = 7
  ref = O_element
FEATURE [App::DocumentObjectGroupPython] P_element015  label="P_element : 004"  # scripted group (container) (typed FeaturePython)
  n = 1
  ref = P_element
FEATURE [App::DocumentObjectGroupPython] G4_DNA_A  # scripted group (container) (typed FeaturePython)
  Dunit = g/cm3
  Dvalue = 1
  Group = -> [H_element134,C_element144,N_element064,O_element126,P_element015]
  conduct = 2
  density = 1
  expand = 3
  formula = G4_DNA_A
  name = G4_DNA_A
  specific = 4
FEATURE [App::DocumentObjectGroupPython] H_element135  label="H_element : 082"  # scripted group (container) (typed FeaturePython)
  n = 10
  ref = H_element
FEATURE [App::DocumentObjectGroupPython] C_element145  label="C_element : 090"  # scripted group (container) (typed FeaturePython)
  n = 10
  ref = C_element
FEATURE [App::DocumentObjectGroupPython] N_element065  label="N_element : 037"  # scripted group (container) (typed FeaturePython)
  n = 5
  ref = N_element
FEATURE [App::DocumentObjectGroupPython] O_element127  label="O_element : 8"  # scripted group (container) (typed FeaturePython)
  n = 8
  ref = O_element
FEATURE [App::DocumentObjectGroupPython] P_element016  label="P_element : 005"  # scripted group (container) (typed FeaturePython)
  n = 1
  ref = P_element
FEATURE [App::DocumentObjectGroupPython] G4_DNA_G  # scripted group (container) (typed FeaturePython)
  Dunit = g/cm3
  Dvalue = 1
  Group = -> [H_element135,C_element145,N_element065,O_element127,P_element016]
  conduct = 2
  density = 1
  expand = 3
  formula = G4_DNA_G
  name = G4_DNA_G
  specific = 4
FEATURE [App::DocumentObjectGroupPython] H_element136  label="H_element : 083"  # scripted group (container) (typed FeaturePython)
  n = 10
  ref = H_element
FEATURE [App::DocumentObjectGroupPython] C_element146  label="C_element : 091"  # scripted group (container) (typed FeaturePython)
  n = 9
  ref = C_element
FEATURE [App::DocumentObjectGroupPython] N_element066  label="N_element : 038"  # scripted group (container) (typed FeaturePython)
  n = 3
  ref = N_element
FEATURE [App::DocumentObjectGroupPython] O_element128  label="O_element : 080"  # scripted group (container) (typed FeaturePython)
  n = 8
  ref = O_element
FEATURE [App::DocumentObjectGroupPython] P_element017  label="P_element : 006"  # scripted group (container) (typed FeaturePython)
  n = 1
  ref = P_element
FEATURE [App::DocumentObjectGroupPython] G4_DNA_C  # scripted group (container) (typed FeaturePython)
  Dunit = g/cm3
  Dvalue = 1
  Group = -> [H_element136,C_element146,N_element066,O_element128,P_element017]
  conduct = 2
  density = 1
  expand = 3
  formula = G4_DNA_C
  name = G4_DNA_C
  specific = 4
FEATURE [App::DocumentObjectGroupPython] H_element137  label="H_element : 084"  # scripted group (container) (typed FeaturePython)
  n = 9
  ref = H_element
FEATURE [App::DocumentObjectGroupPython] C_element147  label="C_element : 092"  # scripted group (container) (typed FeaturePython)
  n = 9
  ref = C_element
FEATURE [App::DocumentObjectGroupPython] N_element067  label="N_element : 039"  # scripted group (container) (typed FeaturePython)
  n = 2
  ref = N_element
FEATURE [App::DocumentObjectGroupPython] O_element129  label="O_element : 9"  # scripted group (container) (typed FeaturePython)
  n = 9
  ref = O_element
FEATURE [App::DocumentObjectGroupPython] P_element018  label="P_element : 007"  # scripted group (container) (typed FeaturePython)
  n = 1
  ref = P_element
FEATURE [App::DocumentObjectGroupPython] G4_DNA_U  # scripted group (container) (typed FeaturePython)
  Dunit = g/cm3
  Dvalue = 1
  Group = -> [H_element137,C_element147,N_element067,O_element129,P_element018]
  conduct = 2
  density = 1
  expand = 3
  formula = G4_DNA_U
  name = G4_DNA_U
  specific = 4
FEATURE [App::DocumentObjectGroupPython] H_element138  label="H_element : 085"  # scripted group (container) (typed FeaturePython)
  n = 11
  ref = H_element
FEATURE [App::DocumentObjectGroupPython] C_element148  label="C_element : 093"  # scripted group (container) (typed FeaturePython)
  n = 10
  ref = C_element
FEATURE [App::DocumentObjectGroupPython] N_element068  label="N_element : 040"  # scripted group (container) (typed FeaturePython)
  n = 2
  ref = N_element
FEATURE [App::DocumentObjectGroupPython] O_element130  label="O_element : 081"  # scripted group (container) (typed FeaturePython)
  n = 9
  ref = O_element
FEATURE [App::DocumentObjectGroupPython] P_element019  label="P_element : 008"  # scripted group (container) (typed FeaturePython)
  n = 1
  ref = P_element
FEATURE [App::DocumentObjectGroupPython] G4_DNA_MU  # scripted group (container) (typed FeaturePython)
  Dunit = g/cm3
  Dvalue = 1
  Group = -> [H_element138,C_element148,N_element068,O_element130,P_element019]
  conduct = 2
  density = 1
  expand = 3
  formula = G4_DNA_MU
  name = G4_DNA_MU
  specific = 4
FEATURE [App::DocumentObjectGroupPython] BioChemical  # scripted group (container) (typed FeaturePython)
  Group = -> [G4_CYTOSINE,G4_THYMINE,G4_URACIL,G4_DNA_ADENINE,G4_DNA_GUANINE,G4_DNA_CYTOSINE,G4_DNA_THYMINE,G4_DNA_URACIL,G4_DNA_ADENOSINE,G4_DNA_GUANOSINE,G4_DNA_CYTIDINE,G4_DNA_URIDINE,G4_DNA_METHYLURIDINE,G4_DNA_MONOPHOSPHATE,G4_DNA_A,G4_DNA_G,G4_DNA_C,G4_DNA_U,G4_DNA_MU]
FEATURE [App::DocumentObjectGroupPython] G4Materials  # scripted group (container) (typed FeaturePython)
  Group = -> [NIST,Element,HEP,Space,BioChemical]
  version = 1
FEATURE [App::DocumentObjectGroupPython] Geant4  # scripted group (container) (typed FeaturePython)
  Group = -> [G4Isotopes,G4Elements,G4Materials]
FEATURE [App::DocumentObjectGroupPython] Materials  # scripted group (container) (typed FeaturePython)
  Group = -> [Geant4]
FEATURE [Part::FeaturePython] GDMLBox_WorldBox  # WARN: FeaturePython — macro-defined, semantics opaque (R4)
  lunit = 2
  material = 7
  x = 26
  y = 26
  z = 31.2
FEATURE [Part::Cone] Cone
  Angle = 360
  AttacherType = Attacher::AttachEngine3D
  Height = 2
  Radius1 = 0
  Radius2 = 1
FEATURE [Part::Helix] Helix
  Angle = 0
  AttacherType = Attacher::AttachEngine3D
  Height = 20
  Length = 158.348
  LocalCoord = 0
  Pitch = 8
  Radius = 10
  SegmentLength = 0
  Style = 1
FEATURE [Part::FeaturePython] PathArray  # WARN: FeaturePython — macro-defined, semantics opaque (R4)
  Align = false
  AlignMode = 0
  Base = -> Cone
  Count = 40
  EndOffset = 0
  ExtraTranslation = (0,0,0)
  ForceVertical = false
  Fuse = false
  PathObject = -> Helix
  StartOffset = 0
  TangentVector = (1,0,0)
  VerticalVector = (0,0,1)
FEATURE [App::Part] Part
  Group = -> [PathArray]
  Origin = -> Origin001
FEATURE [App::Part] worldVOL
  Group = -> [GDMLBox_WorldBox,Part]
  Origin = -> Origin
